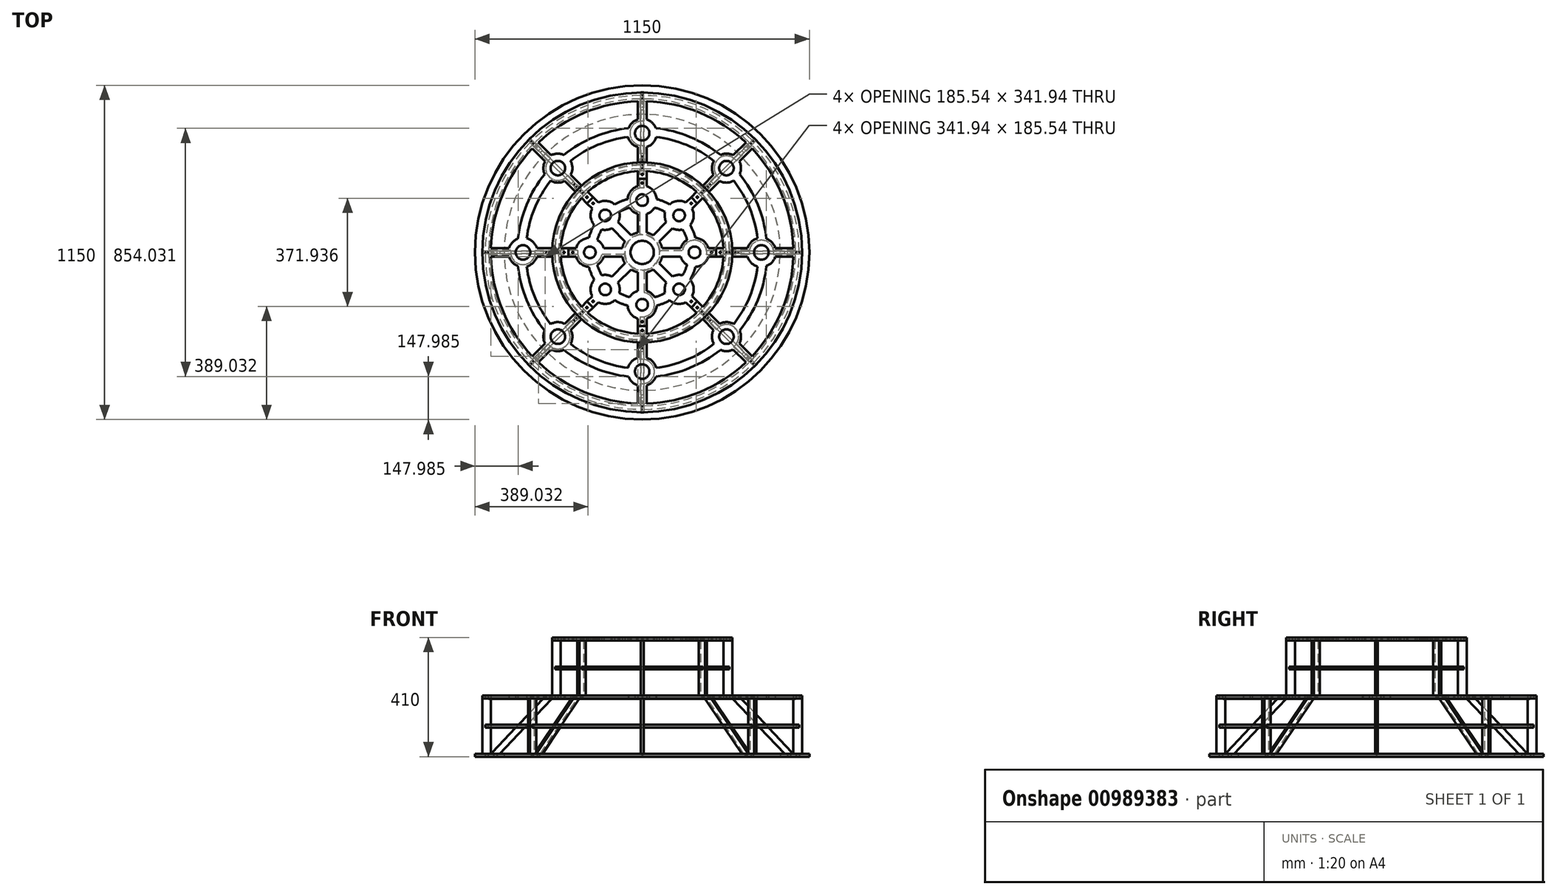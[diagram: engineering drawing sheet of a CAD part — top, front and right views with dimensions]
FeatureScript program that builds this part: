
annotation { "Feature Type Name" : "Feature", "Feature Type Description" : "" }
export const myFeature = defineFeature(function(context is Context, id is Id, definition is map)
    precondition{}
    {
        {
            var Q0;
            Q0=qCreatedBy(makeId("Top.planeOp"),FACE);
            cPlane(context, id + "F0", {"entities" : qUnion([Q0]), "cplaneType" : CPlaneType.OFFSET, "offset" : 200 * mm, "width" : 150 * mm, "height" : 150 * mm});
        }
        {
            var Q0;
            Q0=qCreatedBy(makeId("Top.planeOp"),FACE);
            cPlane(context, id + "F1", {"entities" : qUnion([Q0]), "cplaneType" : CPlaneType.OFFSET, "offset" : 200 * mm, "oppositeDirection" : true, "width" : 150 * mm, "height" : 150 * mm});
        }
        {
            var Q0;
            Q0=qCreatedBy(makeId("Top.planeOp"),FACE);
            cPlane(context, id + "F2", {"entities" : qUnion([Q0]), "cplaneType" : CPlaneType.OFFSET, "offset" : 100 * mm, "oppositeDirection" : true, "width" : 150 * mm, "height" : 150 * mm});
        }
        {
            var Q0;
            Q0=qCreatedBy(makeId("Top.planeOp"),FACE);
            cPlane(context, id + "F3", {"entities" : qUnion([Q0]), "cplaneType" : CPlaneType.OFFSET, "offset" : 100 * mm, "width" : 150 * mm, "height" : 150 * mm});
        }
        {
            var Q0;
            Q0=qCreatedBy(makeId("Top.planeOp"),FACE);
            var sketch = newSketch(context, id + "F4", { "sketchPlane" : qUnion([Q0])});
            skCircle(sketch, "E0", {"center": v(0, 0) * mm, "radius": 550 * mm});
            skArc(sketch, "E1", {"start": v(15, -519.78) * mm, "mid": v(199, -480.42) * mm, "end": v(356.94, -378.15) * mm});
            skArc(sketch, "E2", {"start": v(46.86, -427.44) * mm, "mid": v(164.55, -397.27) * mm, "end": v(269.1, -335.38) * mm});
            skArc(sketch, "E3", {"start": v(48.3, -397.07) * mm, "mid": v(153.07, -369.55) * mm, "end": v(246.62, -314.93) * mm});
            skArc(sketch, "E4", {"start": v(15, -309.64) * mm, "mid": v(118.63, -286.4) * mm, "end": v(208.34, -229.55) * mm});
            skCircle(sketch, "E5", {"center": v(0, 0) * mm, "radius": 280 * mm});
            skCircle(sketch, "E6", {"center": v(0, 0) * mm, "radius": 190 * mm, "construction": true});
            skCircle(sketch, "E7", {"center": v(0, 0) * mm, "radius": 160 * mm, "construction": true});
            skCircle(sketch, "E8", {"center": v(0, 0) * mm, "radius": 40 * mm, "construction": true});
            skCircle(sketch, "E9", {"center": v(0, 0) * mm, "radius": 70 * mm, "construction": true});
            skLineSegment(sketch, "E10", {"start": v(0, 725.48) * mm, "end": v(0, -722.46) * mm, "construction": true});
            skLineSegment(sketch, "E11", {"start": v(-695.44, 0) * mm, "end": v(901.66, 0) * mm, "construction": true});
            skArc(sketch, "E12", {"start": v(-15, -362.3) * mm, "mid": v(-36.11, -375.42) * mm, "end": v(-48.3, -397.07) * mm});
            skCircle(sketch, "E13", {"center": v(0, -410) * mm, "radius": 25 * mm});
            skLineSegment(sketch, "E14", {"start": v(15, -519.78) * mm, "end": v(15, -457.7) * mm});
            skLineSegment(sketch, "E15", {"start": v(-15, -457.7) * mm, "end": v(-15, -519.78) * mm});
            skLineSegment(sketch, "E16", {"start": v(-15, -362.3) * mm, "end": v(-15, -309.64) * mm});
            skLineSegment(sketch, "E17", {"start": v(15, -362.3) * mm, "end": v(15, -309.64) * mm});
            skArc(sketch, "E18.trimOffspring", {"start": v(-46.86, -427.44) * mm, "mid": v(-34.43, -446.26) * mm, "end": v(-15, -457.7) * mm});
            skArc(sketch, "E19.trimOffspring", {"start": v(48.3, -397.07) * mm, "mid": v(36.11, -375.42) * mm, "end": v(15, -362.3) * mm});
            skArc(sketch, "E20.trimOffspring", {"start": v(15, -457.7) * mm, "mid": v(34.43, -446.26) * mm, "end": v(46.86, -427.44) * mm});
            skArc(sketch, "E21.1.0", {"start": v(334.25, -313.03) * mm, "mid": v(339.9, -291.2) * mm, "end": v(335.38, -269.1) * mm});
            skCircle(sketch, "E21.1.1", {"center": v(289.91, -289.91) * mm, "radius": 25 * mm});
            skLineSegment(sketch, "E21.1.2", {"start": v(266.8, -245.58) * mm, "end": v(229.55, -208.34) * mm});
            skLineSegment(sketch, "E21.1.3", {"start": v(245.58, -266.8) * mm, "end": v(208.34, -229.55) * mm});
            skArc(sketch, "E21.1.4", {"start": v(245.58, -266.8) * mm, "mid": v(239.93, -291) * mm, "end": v(246.62, -314.93) * mm});
            skArc(sketch, "E21.1.5", {"start": v(269.1, -335.38) * mm, "mid": v(291.2, -339.9) * mm, "end": v(313.03, -334.25) * mm});
            skArc(sketch, "E21.1.6", {"start": v(314.93, -246.62) * mm, "mid": v(291, -239.93) * mm, "end": v(266.8, -245.58) * mm});
            skLineSegment(sketch, "E21.1.7", {"start": v(378.15, -356.94) * mm, "end": v(334.25, -313.03) * mm});
            skLineSegment(sketch, "E21.1.8", {"start": v(313.03, -334.25) * mm, "end": v(356.94, -378.15) * mm});
            skArc(sketch, "E21.2.0", {"start": v(457.7, 15) * mm, "mid": v(446.26, 34.43) * mm, "end": v(427.44, 46.86) * mm});
            skCircle(sketch, "E21.2.1", {"center": v(410, 0) * mm, "radius": 25 * mm});
            skLineSegment(sketch, "E21.2.2", {"start": v(362.3, 15) * mm, "end": v(309.64, 15) * mm});
            skLineSegment(sketch, "E21.2.3", {"start": v(362.3, -15) * mm, "end": v(309.64, -15) * mm});
            skArc(sketch, "E21.2.4", {"start": v(362.3, -15) * mm, "mid": v(375.42, -36.11) * mm, "end": v(397.07, -48.3) * mm});
            skArc(sketch, "E21.2.5", {"start": v(427.44, -46.86) * mm, "mid": v(446.26, -34.43) * mm, "end": v(457.7, -15) * mm});
            skArc(sketch, "E21.2.6", {"start": v(397.07, 48.3) * mm, "mid": v(375.42, 36.11) * mm, "end": v(362.3, 15) * mm});
            skLineSegment(sketch, "E21.2.7", {"start": v(519.78, 15) * mm, "end": v(457.7, 15) * mm});
            skLineSegment(sketch, "E21.2.8", {"start": v(457.7, -15) * mm, "end": v(519.78, -15) * mm});
            skArc(sketch, "E21.3.0", {"start": v(313.03, 334.25) * mm, "mid": v(291.2, 339.9) * mm, "end": v(269.1, 335.38) * mm});
            skCircle(sketch, "E21.3.1", {"center": v(289.91, 289.91) * mm, "radius": 25 * mm});
            skLineSegment(sketch, "E21.3.2", {"start": v(245.58, 266.8) * mm, "end": v(208.34, 229.55) * mm});
            skLineSegment(sketch, "E21.3.3", {"start": v(266.8, 245.58) * mm, "end": v(229.55, 208.34) * mm});
            skArc(sketch, "E21.3.4", {"start": v(266.8, 245.58) * mm, "mid": v(291, 239.93) * mm, "end": v(314.93, 246.62) * mm});
            skArc(sketch, "E21.3.5", {"start": v(335.38, 269.1) * mm, "mid": v(339.9, 291.2) * mm, "end": v(334.25, 313.03) * mm});
            skArc(sketch, "E21.3.6", {"start": v(246.62, 314.93) * mm, "mid": v(239.93, 291) * mm, "end": v(245.58, 266.8) * mm});
            skLineSegment(sketch, "E21.3.7", {"start": v(356.94, 378.15) * mm, "end": v(313.03, 334.25) * mm});
            skLineSegment(sketch, "E21.3.8", {"start": v(334.25, 313.03) * mm, "end": v(378.15, 356.94) * mm});
            skArc(sketch, "E21.4.0", {"start": v(-15, 457.7) * mm, "mid": v(-34.43, 446.26) * mm, "end": v(-46.86, 427.44) * mm});
            skCircle(sketch, "E21.4.1", {"center": v(0, 410) * mm, "radius": 25 * mm});
            skLineSegment(sketch, "E21.4.2", {"start": v(-15, 362.3) * mm, "end": v(-15, 309.64) * mm});
            skLineSegment(sketch, "E21.4.3", {"start": v(15, 362.3) * mm, "end": v(15, 309.64) * mm});
            skArc(sketch, "E21.4.4", {"start": v(15, 362.3) * mm, "mid": v(36.11, 375.42) * mm, "end": v(48.3, 397.07) * mm});
            skArc(sketch, "E21.4.5", {"start": v(46.86, 427.44) * mm, "mid": v(34.43, 446.26) * mm, "end": v(15, 457.7) * mm});
            skArc(sketch, "E21.4.6", {"start": v(-48.3, 397.07) * mm, "mid": v(-36.11, 375.42) * mm, "end": v(-15, 362.3) * mm});
            skLineSegment(sketch, "E21.4.7", {"start": v(-15, 519.78) * mm, "end": v(-15, 457.7) * mm});
            skLineSegment(sketch, "E21.4.8", {"start": v(15, 457.7) * mm, "end": v(15, 519.78) * mm});
            skArc(sketch, "E21.5.0", {"start": v(-334.25, 313.03) * mm, "mid": v(-339.9, 291.2) * mm, "end": v(-335.38, 269.1) * mm});
            skCircle(sketch, "E21.5.1", {"center": v(-289.91, 289.91) * mm, "radius": 25 * mm});
            skLineSegment(sketch, "E21.5.2", {"start": v(-266.8, 245.58) * mm, "end": v(-229.55, 208.34) * mm});
            skLineSegment(sketch, "E21.5.3", {"start": v(-245.58, 266.8) * mm, "end": v(-208.34, 229.55) * mm});
            skArc(sketch, "E21.5.4", {"start": v(-245.58, 266.8) * mm, "mid": v(-239.93, 291) * mm, "end": v(-246.62, 314.93) * mm});
            skArc(sketch, "E21.5.5", {"start": v(-269.1, 335.38) * mm, "mid": v(-291.2, 339.9) * mm, "end": v(-313.03, 334.25) * mm});
            skArc(sketch, "E21.5.6", {"start": v(-314.93, 246.62) * mm, "mid": v(-291, 239.93) * mm, "end": v(-266.8, 245.58) * mm});
            skLineSegment(sketch, "E21.5.7", {"start": v(-378.15, 356.94) * mm, "end": v(-334.25, 313.03) * mm});
            skLineSegment(sketch, "E21.5.8", {"start": v(-313.03, 334.25) * mm, "end": v(-356.94, 378.15) * mm});
            skArc(sketch, "E21.6.0", {"start": v(-457.7, -15) * mm, "mid": v(-446.26, -34.43) * mm, "end": v(-427.44, -46.86) * mm});
            skCircle(sketch, "E21.6.1", {"center": v(-410, 0) * mm, "radius": 25 * mm});
            skLineSegment(sketch, "E21.6.2", {"start": v(-362.3, -15) * mm, "end": v(-309.64, -15) * mm});
            skLineSegment(sketch, "E21.6.3", {"start": v(-362.3, 15) * mm, "end": v(-309.64, 15) * mm});
            skArc(sketch, "E21.6.4", {"start": v(-362.3, 15) * mm, "mid": v(-375.42, 36.11) * mm, "end": v(-397.07, 48.3) * mm});
            skArc(sketch, "E21.6.5", {"start": v(-427.44, 46.86) * mm, "mid": v(-446.26, 34.43) * mm, "end": v(-457.7, 15) * mm});
            skArc(sketch, "E21.6.6", {"start": v(-397.07, -48.3) * mm, "mid": v(-375.42, -36.11) * mm, "end": v(-362.3, -15) * mm});
            skLineSegment(sketch, "E21.6.7", {"start": v(-519.78, -15) * mm, "end": v(-457.7, -15) * mm});
            skLineSegment(sketch, "E21.6.8", {"start": v(-457.7, 15) * mm, "end": v(-519.78, 15) * mm});
            skArc(sketch, "E21.7.0", {"start": v(-313.03, -334.25) * mm, "mid": v(-291.2, -339.9) * mm, "end": v(-269.1, -335.38) * mm});
            skCircle(sketch, "E21.7.1", {"center": v(-289.91, -289.91) * mm, "radius": 25 * mm});
            skLineSegment(sketch, "E21.7.2", {"start": v(-245.58, -266.8) * mm, "end": v(-208.34, -229.55) * mm});
            skLineSegment(sketch, "E21.7.3", {"start": v(-266.8, -245.58) * mm, "end": v(-229.55, -208.34) * mm});
            skArc(sketch, "E21.7.4", {"start": v(-266.8, -245.58) * mm, "mid": v(-291, -239.93) * mm, "end": v(-314.93, -246.62) * mm});
            skArc(sketch, "E21.7.5", {"start": v(-335.38, -269.1) * mm, "mid": v(-339.9, -291.2) * mm, "end": v(-334.25, -313.03) * mm});
            skArc(sketch, "E21.7.6", {"start": v(-246.62, -314.93) * mm, "mid": v(-239.93, -291) * mm, "end": v(-245.58, -266.8) * mm});
            skLineSegment(sketch, "E21.7.7", {"start": v(-356.94, -378.15) * mm, "end": v(-313.03, -334.25) * mm});
            skLineSegment(sketch, "E21.7.8", {"start": v(-334.25, -313.03) * mm, "end": v(-378.15, -356.94) * mm});
            skArc(sketch, "E22.trimOffspring", {"start": v(-246.62, -314.93) * mm, "mid": v(-153.07, -369.55) * mm, "end": v(-48.3, -397.07) * mm});
            skArc(sketch, "E23.trimOffspring", {"start": v(-269.1, -335.38) * mm, "mid": v(-164.55, -397.27) * mm, "end": v(-46.86, -427.44) * mm});
            skArc(sketch, "E24.trimOffspring", {"start": v(-356.94, -378.15) * mm, "mid": v(-199, -480.42) * mm, "end": v(-15, -519.78) * mm});
            skArc(sketch, "E25.trimOffspring", {"start": v(-208.34, -229.55) * mm, "mid": v(-118.63, -286.4) * mm, "end": v(-15, -309.64) * mm});
            skArc(sketch, "E26.trimOffspring", {"start": v(-397.07, -48.3) * mm, "mid": v(-369.55, -153.07) * mm, "end": v(-314.93, -246.62) * mm});
            skArc(sketch, "E27.trimOffspring", {"start": v(-427.44, -46.86) * mm, "mid": v(-397.27, -164.55) * mm, "end": v(-335.38, -269.1) * mm});
            skArc(sketch, "E28.trimOffspring", {"start": v(-309.64, -15) * mm, "mid": v(-286.4, -118.63) * mm, "end": v(-229.55, -208.34) * mm});
            skArc(sketch, "E29.trimOffspring", {"start": v(-519.78, -15) * mm, "mid": v(-480.42, -199) * mm, "end": v(-378.15, -356.94) * mm});
            skArc(sketch, "E30.trimOffspring", {"start": v(-314.93, 246.62) * mm, "mid": v(-369.55, 153.07) * mm, "end": v(-397.07, 48.3) * mm});
            skArc(sketch, "E31.trimOffspring", {"start": v(-335.38, 269.1) * mm, "mid": v(-397.27, 164.55) * mm, "end": v(-427.44, 46.86) * mm});
            skArc(sketch, "E32.trimOffspring", {"start": v(-378.15, 356.94) * mm, "mid": v(-480.42, 199) * mm, "end": v(-519.78, 15) * mm});
            skArc(sketch, "E33.trimOffspring", {"start": v(-229.55, 208.34) * mm, "mid": v(-286.4, 118.63) * mm, "end": v(-309.64, 15) * mm});
            skArc(sketch, "E34.trimOffspring", {"start": v(-15, 309.64) * mm, "mid": v(-118.63, 286.4) * mm, "end": v(-208.34, 229.55) * mm});
            skArc(sketch, "E35.trimOffspring", {"start": v(-48.3, 397.07) * mm, "mid": v(-153.07, 369.55) * mm, "end": v(-246.62, 314.93) * mm});
            skArc(sketch, "E36.trimOffspring", {"start": v(-46.86, 427.44) * mm, "mid": v(-164.55, 397.27) * mm, "end": v(-269.1, 335.38) * mm});
            skArc(sketch, "E37.trimOffspring", {"start": v(-15, 519.78) * mm, "mid": v(-199, 480.42) * mm, "end": v(-356.94, 378.15) * mm});
            skArc(sketch, "E38.trimOffspring", {"start": v(269.1, 335.38) * mm, "mid": v(164.55, 397.27) * mm, "end": v(46.86, 427.44) * mm});
            skArc(sketch, "E39.trimOffspring", {"start": v(246.62, 314.93) * mm, "mid": v(153.07, 369.55) * mm, "end": v(48.3, 397.07) * mm});
            skArc(sketch, "E40.trimOffspring", {"start": v(208.34, 229.55) * mm, "mid": v(118.63, 286.4) * mm, "end": v(15, 309.64) * mm});
            skArc(sketch, "E41.trimOffspring", {"start": v(356.94, 378.15) * mm, "mid": v(199, 480.42) * mm, "end": v(15, 519.78) * mm});
            skArc(sketch, "E42.trimOffspring", {"start": v(309.64, 15) * mm, "mid": v(286.4, 118.63) * mm, "end": v(229.55, 208.34) * mm});
            skArc(sketch, "E43.trimOffspring", {"start": v(397.07, 48.3) * mm, "mid": v(369.55, 153.07) * mm, "end": v(314.93, 246.62) * mm});
            skArc(sketch, "E44.trimOffspring", {"start": v(427.44, 46.86) * mm, "mid": v(397.27, 164.55) * mm, "end": v(335.38, 269.1) * mm});
            skArc(sketch, "E45.trimOffspring", {"start": v(519.78, 15) * mm, "mid": v(480.42, 199) * mm, "end": v(378.15, 356.94) * mm});
            skArc(sketch, "E46.trimOffspring", {"start": v(335.38, -269.1) * mm, "mid": v(397.27, -164.55) * mm, "end": v(427.44, -46.86) * mm});
            skArc(sketch, "E47.trimOffspring", {"start": v(314.93, -246.62) * mm, "mid": v(369.55, -153.07) * mm, "end": v(397.07, -48.3) * mm});
            skArc(sketch, "E48.trimOffspring", {"start": v(378.15, -356.94) * mm, "mid": v(480.42, -199) * mm, "end": v(519.78, -15) * mm});
            skArc(sketch, "E49.trimOffspring", {"start": v(229.55, -208.34) * mm, "mid": v(286.4, -118.63) * mm, "end": v(309.64, -15) * mm});
            skLineSegment(sketch, "E50.bottom", {"start": v(4.9, 530) * mm, "end": v(1, 530) * mm});
            skLineSegment(sketch, "E50.top", {"start": v(4.9, 540) * mm, "end": v(1, 540) * mm});
            skLineSegment(sketch, "E50.left", {"start": v(4.9, 530) * mm, "end": v(4.9, 540) * mm});
            skLineSegment(sketch, "E50.right", {"start": v(-4.9, 530) * mm, "end": v(-4.9, 540) * mm});
            skPoint(sketch, "E50.middle", {"position": v(0, 535) * mm});
            skLineSegment(sketch, "E51", {"start": v(0, 541) * mm, "end": v(-1, 540) * mm});
            skLineSegment(sketch, "E52", {"start": v(0, 541) * mm, "end": v(1, 540) * mm});
            skLineSegment(sketch, "E53.trimOffspring", {"start": v(-1, 540) * mm, "end": v(-4.9, 540) * mm});
            skLineSegment(sketch, "E54", {"start": v(0, 529) * mm, "end": v(-1, 530) * mm});
            skLineSegment(sketch, "E55", {"start": v(0, 529) * mm, "end": v(1, 530) * mm});
            skLineSegment(sketch, "E56.trimOffspring", {"start": v(-1, 530) * mm, "end": v(-4.9, 530) * mm});
            skPoint(sketch, "E57.1.0", {"position": v(-378.3, 378.3) * mm});
            skLineSegment(sketch, "E57.1.1", {"start": v(-378.23, 371.3) * mm, "end": v(-385.3, 378.37) * mm});
            skLineSegment(sketch, "E57.1.2", {"start": v(-371.3, 378.23) * mm, "end": v(-378.37, 385.3) * mm});
            skLineSegment(sketch, "E57.1.3", {"start": v(-371.3, 378.23) * mm, "end": v(-374.06, 375.47) * mm});
            skLineSegment(sketch, "E57.1.4", {"start": v(-374.06, 374.06) * mm, "end": v(-374.06, 375.47) * mm});
            skLineSegment(sketch, "E57.1.5", {"start": v(-374.06, 374.06) * mm, "end": v(-375.47, 374.06) * mm});
            skLineSegment(sketch, "E57.1.6", {"start": v(-375.47, 374.06) * mm, "end": v(-378.23, 371.3) * mm});
            skLineSegment(sketch, "E57.1.7", {"start": v(-378.37, 385.3) * mm, "end": v(-381.13, 382.54) * mm});
            skLineSegment(sketch, "E57.1.8", {"start": v(-382.54, 381.13) * mm, "end": v(-385.3, 378.37) * mm});
            skLineSegment(sketch, "E57.1.9", {"start": v(-382.54, 382.54) * mm, "end": v(-381.13, 382.54) * mm});
            skLineSegment(sketch, "E57.1.10", {"start": v(-382.54, 382.54) * mm, "end": v(-382.54, 381.13) * mm});
            skPoint(sketch, "E57.2.0", {"position": v(-535, 0) * mm});
            skLineSegment(sketch, "E57.2.1", {"start": v(-530, -4.9) * mm, "end": v(-540, -4.9) * mm});
            skLineSegment(sketch, "E57.2.2", {"start": v(-530, 4.9) * mm, "end": v(-540, 4.9) * mm});
            skLineSegment(sketch, "E57.2.3", {"start": v(-530, 4.9) * mm, "end": v(-530, 1) * mm});
            skLineSegment(sketch, "E57.2.4", {"start": v(-529, 0) * mm, "end": v(-530, 1) * mm});
            skLineSegment(sketch, "E57.2.5", {"start": v(-529, 0) * mm, "end": v(-530, -1) * mm});
            skLineSegment(sketch, "E57.2.6", {"start": v(-530, -1) * mm, "end": v(-530, -4.9) * mm});
            skLineSegment(sketch, "E57.2.7", {"start": v(-540, 4.9) * mm, "end": v(-540, 1) * mm});
            skLineSegment(sketch, "E57.2.8", {"start": v(-540, -1) * mm, "end": v(-540, -4.9) * mm});
            skLineSegment(sketch, "E57.2.9", {"start": v(-541, 0) * mm, "end": v(-540, 1) * mm});
            skLineSegment(sketch, "E57.2.10", {"start": v(-541, 0) * mm, "end": v(-540, -1) * mm});
            skPoint(sketch, "E57.3.0", {"position": v(-378.3, -378.3) * mm});
            skLineSegment(sketch, "E57.3.1", {"start": v(-371.3, -378.23) * mm, "end": v(-378.37, -385.3) * mm});
            skLineSegment(sketch, "E57.3.2", {"start": v(-378.23, -371.3) * mm, "end": v(-385.3, -378.37) * mm});
            skLineSegment(sketch, "E57.3.3", {"start": v(-378.23, -371.3) * mm, "end": v(-375.47, -374.06) * mm});
            skLineSegment(sketch, "E57.3.4", {"start": v(-374.06, -374.06) * mm, "end": v(-375.47, -374.06) * mm});
            skLineSegment(sketch, "E57.3.5", {"start": v(-374.06, -374.06) * mm, "end": v(-374.06, -375.47) * mm});
            skLineSegment(sketch, "E57.3.6", {"start": v(-374.06, -375.47) * mm, "end": v(-371.3, -378.23) * mm});
            skLineSegment(sketch, "E57.3.7", {"start": v(-385.3, -378.37) * mm, "end": v(-382.54, -381.13) * mm});
            skLineSegment(sketch, "E57.3.8", {"start": v(-381.13, -382.54) * mm, "end": v(-378.37, -385.3) * mm});
            skLineSegment(sketch, "E57.3.9", {"start": v(-382.54, -382.54) * mm, "end": v(-382.54, -381.13) * mm});
            skLineSegment(sketch, "E57.3.10", {"start": v(-382.54, -382.54) * mm, "end": v(-381.13, -382.54) * mm});
            skPoint(sketch, "E57.4.0", {"position": v(0, -535) * mm});
            skLineSegment(sketch, "E57.4.1", {"start": v(4.9, -530) * mm, "end": v(4.9, -540) * mm});
            skLineSegment(sketch, "E57.4.2", {"start": v(-4.9, -530) * mm, "end": v(-4.9, -540) * mm});
            skLineSegment(sketch, "E57.4.3", {"start": v(-4.9, -530) * mm, "end": v(-1, -530) * mm});
            skLineSegment(sketch, "E57.4.4", {"start": v(0, -529) * mm, "end": v(-1, -530) * mm});
            skLineSegment(sketch, "E57.4.5", {"start": v(0, -529) * mm, "end": v(1, -530) * mm});
            skLineSegment(sketch, "E57.4.6", {"start": v(1, -530) * mm, "end": v(4.9, -530) * mm});
            skLineSegment(sketch, "E57.4.7", {"start": v(-4.9, -540) * mm, "end": v(-1, -540) * mm});
            skLineSegment(sketch, "E57.4.8", {"start": v(1, -540) * mm, "end": v(4.9, -540) * mm});
            skLineSegment(sketch, "E57.4.9", {"start": v(0, -541) * mm, "end": v(-1, -540) * mm});
            skLineSegment(sketch, "E57.4.10", {"start": v(0, -541) * mm, "end": v(1, -540) * mm});
            skPoint(sketch, "E57.5.0", {"position": v(378.3, -378.3) * mm});
            skLineSegment(sketch, "E57.5.1", {"start": v(378.23, -371.3) * mm, "end": v(385.3, -378.37) * mm});
            skLineSegment(sketch, "E57.5.2", {"start": v(371.3, -378.23) * mm, "end": v(378.37, -385.3) * mm});
            skLineSegment(sketch, "E57.5.3", {"start": v(371.3, -378.23) * mm, "end": v(374.06, -375.47) * mm});
            skLineSegment(sketch, "E57.5.4", {"start": v(374.06, -374.06) * mm, "end": v(374.06, -375.47) * mm});
            skLineSegment(sketch, "E57.5.5", {"start": v(374.06, -374.06) * mm, "end": v(375.47, -374.06) * mm});
            skLineSegment(sketch, "E57.5.6", {"start": v(375.47, -374.06) * mm, "end": v(378.23, -371.3) * mm});
            skLineSegment(sketch, "E57.5.7", {"start": v(378.37, -385.3) * mm, "end": v(381.13, -382.54) * mm});
            skLineSegment(sketch, "E57.5.8", {"start": v(382.54, -381.13) * mm, "end": v(385.3, -378.37) * mm});
            skLineSegment(sketch, "E57.5.9", {"start": v(382.54, -382.54) * mm, "end": v(381.13, -382.54) * mm});
            skLineSegment(sketch, "E57.5.10", {"start": v(382.54, -382.54) * mm, "end": v(382.54, -381.13) * mm});
            skPoint(sketch, "E57.6.0", {"position": v(535, 0) * mm});
            skLineSegment(sketch, "E57.6.1", {"start": v(530, 4.9) * mm, "end": v(540, 4.9) * mm});
            skLineSegment(sketch, "E57.6.2", {"start": v(530, -4.9) * mm, "end": v(540, -4.9) * mm});
            skLineSegment(sketch, "E57.6.3", {"start": v(530, -4.9) * mm, "end": v(530, -1) * mm});
            skLineSegment(sketch, "E57.6.4", {"start": v(529, 0) * mm, "end": v(530, -1) * mm});
            skLineSegment(sketch, "E57.6.5", {"start": v(529, 0) * mm, "end": v(530, 1) * mm});
            skLineSegment(sketch, "E57.6.6", {"start": v(530, 1) * mm, "end": v(530, 4.9) * mm});
            skLineSegment(sketch, "E57.6.7", {"start": v(540, -4.9) * mm, "end": v(540, -1) * mm});
            skLineSegment(sketch, "E57.6.8", {"start": v(540, 1) * mm, "end": v(540, 4.9) * mm});
            skLineSegment(sketch, "E57.6.9", {"start": v(541, 0) * mm, "end": v(540, -1) * mm});
            skLineSegment(sketch, "E57.6.10", {"start": v(541, 0) * mm, "end": v(540, 1) * mm});
            skPoint(sketch, "E57.7.0", {"position": v(378.3, 378.3) * mm});
            skLineSegment(sketch, "E57.7.1", {"start": v(371.3, 378.23) * mm, "end": v(378.37, 385.3) * mm});
            skLineSegment(sketch, "E57.7.2", {"start": v(378.23, 371.3) * mm, "end": v(385.3, 378.37) * mm});
            skLineSegment(sketch, "E57.7.3", {"start": v(378.23, 371.3) * mm, "end": v(375.47, 374.06) * mm});
            skLineSegment(sketch, "E57.7.4", {"start": v(374.06, 374.06) * mm, "end": v(375.47, 374.06) * mm});
            skLineSegment(sketch, "E57.7.5", {"start": v(374.06, 374.06) * mm, "end": v(374.06, 375.47) * mm});
            skLineSegment(sketch, "E57.7.6", {"start": v(374.06, 375.47) * mm, "end": v(371.3, 378.23) * mm});
            skLineSegment(sketch, "E57.7.7", {"start": v(385.3, 378.37) * mm, "end": v(382.54, 381.13) * mm});
            skLineSegment(sketch, "E57.7.8", {"start": v(381.13, 382.54) * mm, "end": v(378.37, 385.3) * mm});
            skLineSegment(sketch, "E57.7.9", {"start": v(382.54, 382.54) * mm, "end": v(382.54, 381.13) * mm});
            skLineSegment(sketch, "E57.7.10", {"start": v(382.54, 382.54) * mm, "end": v(381.13, 382.54) * mm});
            skLineSegment(sketch, "E58.bottom", {"start": v(4.9, 290) * mm, "end": v(1, 290) * mm});
            skLineSegment(sketch, "E58.top", {"start": v(4.9, 300) * mm, "end": v(1, 300) * mm});
            skLineSegment(sketch, "E58.left", {"start": v(4.9, 290) * mm, "end": v(4.9, 300) * mm});
            skLineSegment(sketch, "E58.right", {"start": v(-4.9, 290) * mm, "end": v(-4.9, 300) * mm});
            skPoint(sketch, "E58.middle", {"position": v(0, 295) * mm});
            skLineSegment(sketch, "E59", {"start": v(0, 301) * mm, "end": v(-1, 300) * mm});
            skLineSegment(sketch, "E60", {"start": v(0, 301) * mm, "end": v(1, 300) * mm});
            skLineSegment(sketch, "E61.trimOffspring", {"start": v(-1, 300) * mm, "end": v(-4.9, 300) * mm});
            skLineSegment(sketch, "E62", {"start": v(0, 289) * mm, "end": v(-1, 290) * mm});
            skLineSegment(sketch, "E63", {"start": v(0, 289) * mm, "end": v(1, 290) * mm});
            skLineSegment(sketch, "E64.trimOffspring", {"start": v(-1, 290) * mm, "end": v(-4.9, 290) * mm});
            skLineSegment(sketch, "E65.1.0", {"start": v(-201.6, 208.53) * mm, "end": v(-208.67, 215.6) * mm});
            skPoint(sketch, "E65.1.1", {"position": v(-208.6, 208.6) * mm});
            skLineSegment(sketch, "E65.1.2", {"start": v(-208.53, 201.6) * mm, "end": v(-215.6, 208.67) * mm});
            skLineSegment(sketch, "E65.1.3", {"start": v(-205.77, 204.35) * mm, "end": v(-208.53, 201.6) * mm});
            skLineSegment(sketch, "E65.1.4", {"start": v(-208.67, 215.6) * mm, "end": v(-211.42, 212.84) * mm});
            skLineSegment(sketch, "E65.1.5", {"start": v(-201.6, 208.53) * mm, "end": v(-204.35, 205.77) * mm});
            skLineSegment(sketch, "E65.1.6", {"start": v(-212.84, 211.42) * mm, "end": v(-215.6, 208.67) * mm});
            skLineSegment(sketch, "E65.1.7", {"start": v(-204.35, 204.35) * mm, "end": v(-205.77, 204.35) * mm});
            skLineSegment(sketch, "E65.1.8", {"start": v(-212.84, 212.84) * mm, "end": v(-211.42, 212.84) * mm});
            skLineSegment(sketch, "E65.1.9", {"start": v(-212.84, 212.84) * mm, "end": v(-212.84, 211.42) * mm});
            skLineSegment(sketch, "E65.1.10", {"start": v(-204.35, 204.35) * mm, "end": v(-204.35, 205.77) * mm});
            skLineSegment(sketch, "E65.2.0", {"start": v(-290, 4.9) * mm, "end": v(-300, 4.9) * mm});
            skPoint(sketch, "E65.2.1", {"position": v(-295, 0) * mm});
            skLineSegment(sketch, "E65.2.2", {"start": v(-290, -4.9) * mm, "end": v(-300, -4.9) * mm});
            skLineSegment(sketch, "E65.2.3", {"start": v(-290, -1) * mm, "end": v(-290, -4.9) * mm});
            skLineSegment(sketch, "E65.2.4", {"start": v(-300, 4.9) * mm, "end": v(-300, 1) * mm});
            skLineSegment(sketch, "E65.2.5", {"start": v(-290, 4.9) * mm, "end": v(-290, 1) * mm});
            skLineSegment(sketch, "E65.2.6", {"start": v(-300, -1) * mm, "end": v(-300, -4.9) * mm});
            skLineSegment(sketch, "E65.2.7", {"start": v(-289, 0) * mm, "end": v(-290, -1) * mm});
            skLineSegment(sketch, "E65.2.8", {"start": v(-301, 0) * mm, "end": v(-300, 1) * mm});
            skLineSegment(sketch, "E65.2.9", {"start": v(-301, 0) * mm, "end": v(-300, -1) * mm});
            skLineSegment(sketch, "E65.2.10", {"start": v(-289, 0) * mm, "end": v(-290, 1) * mm});
            skLineSegment(sketch, "E65.3.0", {"start": v(-208.53, -201.6) * mm, "end": v(-215.6, -208.67) * mm});
            skPoint(sketch, "E65.3.1", {"position": v(-208.6, -208.6) * mm});
            skLineSegment(sketch, "E65.3.2", {"start": v(-201.6, -208.53) * mm, "end": v(-208.67, -215.6) * mm});
            skLineSegment(sketch, "E65.3.3", {"start": v(-204.35, -205.77) * mm, "end": v(-201.6, -208.53) * mm});
            skLineSegment(sketch, "E65.3.4", {"start": v(-215.6, -208.67) * mm, "end": v(-212.84, -211.42) * mm});
            skLineSegment(sketch, "E65.3.5", {"start": v(-208.53, -201.6) * mm, "end": v(-205.77, -204.35) * mm});
            skLineSegment(sketch, "E65.3.6", {"start": v(-211.42, -212.84) * mm, "end": v(-208.67, -215.6) * mm});
            skLineSegment(sketch, "E65.3.7", {"start": v(-204.35, -204.35) * mm, "end": v(-204.35, -205.77) * mm});
            skLineSegment(sketch, "E65.3.8", {"start": v(-212.84, -212.84) * mm, "end": v(-212.84, -211.42) * mm});
            skLineSegment(sketch, "E65.3.9", {"start": v(-212.84, -212.84) * mm, "end": v(-211.42, -212.84) * mm});
            skLineSegment(sketch, "E65.3.10", {"start": v(-204.35, -204.35) * mm, "end": v(-205.77, -204.35) * mm});
            skLineSegment(sketch, "E65.4.0", {"start": v(-4.9, -290) * mm, "end": v(-4.9, -300) * mm});
            skPoint(sketch, "E65.4.1", {"position": v(0, -295) * mm});
            skLineSegment(sketch, "E65.4.2", {"start": v(4.9, -290) * mm, "end": v(4.9, -300) * mm});
            skLineSegment(sketch, "E65.4.3", {"start": v(1, -290) * mm, "end": v(4.9, -290) * mm});
            skLineSegment(sketch, "E65.4.4", {"start": v(-4.9, -300) * mm, "end": v(-1, -300) * mm});
            skLineSegment(sketch, "E65.4.5", {"start": v(-4.9, -290) * mm, "end": v(-1, -290) * mm});
            skLineSegment(sketch, "E65.4.6", {"start": v(1, -300) * mm, "end": v(4.9, -300) * mm});
            skLineSegment(sketch, "E65.4.7", {"start": v(0, -289) * mm, "end": v(1, -290) * mm});
            skLineSegment(sketch, "E65.4.8", {"start": v(0, -301) * mm, "end": v(-1, -300) * mm});
            skLineSegment(sketch, "E65.4.9", {"start": v(0, -301) * mm, "end": v(1, -300) * mm});
            skLineSegment(sketch, "E65.4.10", {"start": v(0, -289) * mm, "end": v(-1, -290) * mm});
            skLineSegment(sketch, "E65.5.0", {"start": v(201.6, -208.53) * mm, "end": v(208.67, -215.6) * mm});
            skPoint(sketch, "E65.5.1", {"position": v(208.6, -208.6) * mm});
            skLineSegment(sketch, "E65.5.2", {"start": v(208.53, -201.6) * mm, "end": v(215.6, -208.67) * mm});
            skLineSegment(sketch, "E65.5.3", {"start": v(205.77, -204.35) * mm, "end": v(208.53, -201.6) * mm});
            skLineSegment(sketch, "E65.5.4", {"start": v(208.67, -215.6) * mm, "end": v(211.42, -212.84) * mm});
            skLineSegment(sketch, "E65.5.5", {"start": v(201.6, -208.53) * mm, "end": v(204.35, -205.77) * mm});
            skLineSegment(sketch, "E65.5.6", {"start": v(212.84, -211.42) * mm, "end": v(215.6, -208.67) * mm});
            skLineSegment(sketch, "E65.5.7", {"start": v(204.35, -204.35) * mm, "end": v(205.77, -204.35) * mm});
            skLineSegment(sketch, "E65.5.8", {"start": v(212.84, -212.84) * mm, "end": v(211.42, -212.84) * mm});
            skLineSegment(sketch, "E65.5.9", {"start": v(212.84, -212.84) * mm, "end": v(212.84, -211.42) * mm});
            skLineSegment(sketch, "E65.5.10", {"start": v(204.35, -204.35) * mm, "end": v(204.35, -205.77) * mm});
            skLineSegment(sketch, "E65.6.0", {"start": v(290, -4.9) * mm, "end": v(300, -4.9) * mm});
            skPoint(sketch, "E65.6.1", {"position": v(295, 0) * mm});
            skLineSegment(sketch, "E65.6.2", {"start": v(290, 4.9) * mm, "end": v(300, 4.9) * mm});
            skLineSegment(sketch, "E65.6.3", {"start": v(290, 1) * mm, "end": v(290, 4.9) * mm});
            skLineSegment(sketch, "E65.6.4", {"start": v(300, -4.9) * mm, "end": v(300, -1) * mm});
            skLineSegment(sketch, "E65.6.5", {"start": v(290, -4.9) * mm, "end": v(290, -1) * mm});
            skLineSegment(sketch, "E65.6.6", {"start": v(300, 1) * mm, "end": v(300, 4.9) * mm});
            skLineSegment(sketch, "E65.6.7", {"start": v(289, 0) * mm, "end": v(290, 1) * mm});
            skLineSegment(sketch, "E65.6.8", {"start": v(301, 0) * mm, "end": v(300, -1) * mm});
            skLineSegment(sketch, "E65.6.9", {"start": v(301, 0) * mm, "end": v(300, 1) * mm});
            skLineSegment(sketch, "E65.6.10", {"start": v(289, 0) * mm, "end": v(290, -1) * mm});
            skLineSegment(sketch, "E65.7.0", {"start": v(208.53, 201.6) * mm, "end": v(215.6, 208.67) * mm});
            skPoint(sketch, "E65.7.1", {"position": v(208.6, 208.6) * mm});
            skLineSegment(sketch, "E65.7.2", {"start": v(201.6, 208.53) * mm, "end": v(208.67, 215.6) * mm});
            skLineSegment(sketch, "E65.7.3", {"start": v(204.35, 205.77) * mm, "end": v(201.6, 208.53) * mm});
            skLineSegment(sketch, "E65.7.4", {"start": v(215.6, 208.67) * mm, "end": v(212.84, 211.42) * mm});
            skLineSegment(sketch, "E65.7.5", {"start": v(208.53, 201.6) * mm, "end": v(205.77, 204.35) * mm});
            skLineSegment(sketch, "E65.7.6", {"start": v(211.42, 212.84) * mm, "end": v(208.67, 215.6) * mm});
            skLineSegment(sketch, "E65.7.7", {"start": v(204.35, 204.35) * mm, "end": v(204.35, 205.77) * mm});
            skLineSegment(sketch, "E65.7.8", {"start": v(212.84, 212.84) * mm, "end": v(212.84, 211.42) * mm});
            skLineSegment(sketch, "E65.7.9", {"start": v(212.84, 212.84) * mm, "end": v(211.42, 212.84) * mm});
            skLineSegment(sketch, "E65.7.10", {"start": v(204.35, 204.35) * mm, "end": v(205.77, 204.35) * mm});
            skLineSegment(sketch, "E66.bottom", {"start": v(4.9, 320) * mm, "end": v(1, 320) * mm});
            skLineSegment(sketch, "E66.top", {"start": v(4.9, 330) * mm, "end": v(1, 330) * mm});
            skLineSegment(sketch, "E66.left", {"start": v(4.9, 320) * mm, "end": v(4.9, 330) * mm});
            skLineSegment(sketch, "E66.right", {"start": v(-4.9, 320) * mm, "end": v(-4.9, 330) * mm});
            skPoint(sketch, "E66.middle", {"position": v(0, 325) * mm});
            skLineSegment(sketch, "E67", {"start": v(0, 331) * mm, "end": v(-1, 330) * mm});
            skLineSegment(sketch, "E68", {"start": v(0, 331) * mm, "end": v(1, 330) * mm});
            skLineSegment(sketch, "E69.trimOffspring", {"start": v(-1, 330) * mm, "end": v(-4.9, 330) * mm});
            skLineSegment(sketch, "E70", {"start": v(0, 319) * mm, "end": v(-1, 320) * mm});
            skLineSegment(sketch, "E71", {"start": v(0, 319) * mm, "end": v(1, 320) * mm});
            skLineSegment(sketch, "E72.trimOffspring", {"start": v(-1, 320) * mm, "end": v(-4.9, 320) * mm});
            skLineSegment(sketch, "E73.1.0", {"start": v(-222.8, 229.74) * mm, "end": v(-225.57, 226.98) * mm});
            skLineSegment(sketch, "E73.1.1", {"start": v(-229.74, 222.8) * mm, "end": v(-236.81, 229.88) * mm});
            skLineSegment(sketch, "E73.1.2", {"start": v(-222.8, 229.74) * mm, "end": v(-229.88, 236.81) * mm});
            skLineSegment(sketch, "E73.1.3", {"start": v(-229.88, 236.81) * mm, "end": v(-232.64, 234.05) * mm});
            skLineSegment(sketch, "E73.1.4", {"start": v(-234.05, 232.64) * mm, "end": v(-236.81, 229.88) * mm});
            skLineSegment(sketch, "E73.1.5", {"start": v(-226.98, 225.57) * mm, "end": v(-229.74, 222.8) * mm});
            skPoint(sketch, "E73.1.6", {"position": v(-229.8, 229.8) * mm});
            skLineSegment(sketch, "E73.1.7", {"start": v(-225.57, 225.57) * mm, "end": v(-225.57, 226.98) * mm});
            skLineSegment(sketch, "E73.1.8", {"start": v(-225.57, 225.57) * mm, "end": v(-226.98, 225.57) * mm});
            skLineSegment(sketch, "E73.1.9", {"start": v(-234.05, 234.05) * mm, "end": v(-234.05, 232.64) * mm});
            skLineSegment(sketch, "E73.1.10", {"start": v(-234.05, 234.05) * mm, "end": v(-232.64, 234.05) * mm});
            skLineSegment(sketch, "E73.2.0", {"start": v(-320, 4.9) * mm, "end": v(-320, 1) * mm});
            skLineSegment(sketch, "E73.2.1", {"start": v(-320, -4.9) * mm, "end": v(-330, -4.9) * mm});
            skLineSegment(sketch, "E73.2.2", {"start": v(-320, 4.9) * mm, "end": v(-330, 4.9) * mm});
            skLineSegment(sketch, "E73.2.3", {"start": v(-330, 4.9) * mm, "end": v(-330, 1) * mm});
            skLineSegment(sketch, "E73.2.4", {"start": v(-330, -1) * mm, "end": v(-330, -4.9) * mm});
            skLineSegment(sketch, "E73.2.5", {"start": v(-320, -1) * mm, "end": v(-320, -4.9) * mm});
            skPoint(sketch, "E73.2.6", {"position": v(-325, 0) * mm});
            skLineSegment(sketch, "E73.2.7", {"start": v(-319, 0) * mm, "end": v(-320, 1) * mm});
            skLineSegment(sketch, "E73.2.8", {"start": v(-319, 0) * mm, "end": v(-320, -1) * mm});
            skLineSegment(sketch, "E73.2.9", {"start": v(-331, 0) * mm, "end": v(-330, -1) * mm});
            skLineSegment(sketch, "E73.2.10", {"start": v(-331, 0) * mm, "end": v(-330, 1) * mm});
            skLineSegment(sketch, "E73.3.0", {"start": v(-229.74, -222.8) * mm, "end": v(-226.98, -225.57) * mm});
            skLineSegment(sketch, "E73.3.1", {"start": v(-222.8, -229.74) * mm, "end": v(-229.88, -236.81) * mm});
            skLineSegment(sketch, "E73.3.2", {"start": v(-229.74, -222.8) * mm, "end": v(-236.81, -229.88) * mm});
            skLineSegment(sketch, "E73.3.3", {"start": v(-236.81, -229.88) * mm, "end": v(-234.05, -232.64) * mm});
            skLineSegment(sketch, "E73.3.4", {"start": v(-232.64, -234.05) * mm, "end": v(-229.88, -236.81) * mm});
            skLineSegment(sketch, "E73.3.5", {"start": v(-225.57, -226.98) * mm, "end": v(-222.8, -229.74) * mm});
            skPoint(sketch, "E73.3.6", {"position": v(-229.8, -229.8) * mm});
            skLineSegment(sketch, "E73.3.7", {"start": v(-225.57, -225.57) * mm, "end": v(-226.98, -225.57) * mm});
            skLineSegment(sketch, "E73.3.8", {"start": v(-225.57, -225.57) * mm, "end": v(-225.57, -226.98) * mm});
            skLineSegment(sketch, "E73.3.9", {"start": v(-234.05, -234.05) * mm, "end": v(-232.64, -234.05) * mm});
            skLineSegment(sketch, "E73.3.10", {"start": v(-234.05, -234.05) * mm, "end": v(-234.05, -232.64) * mm});
            skLineSegment(sketch, "E73.4.0", {"start": v(-4.9, -320) * mm, "end": v(-1, -320) * mm});
            skLineSegment(sketch, "E73.4.1", {"start": v(4.9, -320) * mm, "end": v(4.9, -330) * mm});
            skLineSegment(sketch, "E73.4.2", {"start": v(-4.9, -320) * mm, "end": v(-4.9, -330) * mm});
            skLineSegment(sketch, "E73.4.3", {"start": v(-4.9, -330) * mm, "end": v(-1, -330) * mm});
            skLineSegment(sketch, "E73.4.4", {"start": v(1, -330) * mm, "end": v(4.9, -330) * mm});
            skLineSegment(sketch, "E73.4.5", {"start": v(1, -320) * mm, "end": v(4.9, -320) * mm});
            skPoint(sketch, "E73.4.6", {"position": v(0, -325) * mm});
            skLineSegment(sketch, "E73.4.7", {"start": v(0, -319) * mm, "end": v(-1, -320) * mm});
            skLineSegment(sketch, "E73.4.8", {"start": v(0, -319) * mm, "end": v(1, -320) * mm});
            skLineSegment(sketch, "E73.4.9", {"start": v(0, -331) * mm, "end": v(1, -330) * mm});
            skLineSegment(sketch, "E73.4.10", {"start": v(0, -331) * mm, "end": v(-1, -330) * mm});
            skLineSegment(sketch, "E73.5.0", {"start": v(222.8, -229.74) * mm, "end": v(225.57, -226.98) * mm});
            skLineSegment(sketch, "E73.5.1", {"start": v(229.74, -222.8) * mm, "end": v(236.81, -229.88) * mm});
            skLineSegment(sketch, "E73.5.2", {"start": v(222.8, -229.74) * mm, "end": v(229.88, -236.81) * mm});
            skLineSegment(sketch, "E73.5.3", {"start": v(229.88, -236.81) * mm, "end": v(232.64, -234.05) * mm});
            skLineSegment(sketch, "E73.5.4", {"start": v(234.05, -232.64) * mm, "end": v(236.81, -229.88) * mm});
            skLineSegment(sketch, "E73.5.5", {"start": v(226.98, -225.57) * mm, "end": v(229.74, -222.8) * mm});
            skPoint(sketch, "E73.5.6", {"position": v(229.8, -229.8) * mm});
            skLineSegment(sketch, "E73.5.7", {"start": v(225.57, -225.57) * mm, "end": v(225.57, -226.98) * mm});
            skLineSegment(sketch, "E73.5.8", {"start": v(225.57, -225.57) * mm, "end": v(226.98, -225.57) * mm});
            skLineSegment(sketch, "E73.5.9", {"start": v(234.05, -234.05) * mm, "end": v(234.05, -232.64) * mm});
            skLineSegment(sketch, "E73.5.10", {"start": v(234.05, -234.05) * mm, "end": v(232.64, -234.05) * mm});
            skLineSegment(sketch, "E73.6.0", {"start": v(320, -4.9) * mm, "end": v(320, -1) * mm});
            skLineSegment(sketch, "E73.6.1", {"start": v(320, 4.9) * mm, "end": v(330, 4.9) * mm});
            skLineSegment(sketch, "E73.6.2", {"start": v(320, -4.9) * mm, "end": v(330, -4.9) * mm});
            skLineSegment(sketch, "E73.6.3", {"start": v(330, -4.9) * mm, "end": v(330, -1) * mm});
            skLineSegment(sketch, "E73.6.4", {"start": v(330, 1) * mm, "end": v(330, 4.9) * mm});
            skLineSegment(sketch, "E73.6.5", {"start": v(320, 1) * mm, "end": v(320, 4.9) * mm});
            skPoint(sketch, "E73.6.6", {"position": v(325, 0) * mm});
            skLineSegment(sketch, "E73.6.7", {"start": v(319, 0) * mm, "end": v(320, -1) * mm});
            skLineSegment(sketch, "E73.6.8", {"start": v(319, 0) * mm, "end": v(320, 1) * mm});
            skLineSegment(sketch, "E73.6.9", {"start": v(331, 0) * mm, "end": v(330, 1) * mm});
            skLineSegment(sketch, "E73.6.10", {"start": v(331, 0) * mm, "end": v(330, -1) * mm});
            skLineSegment(sketch, "E73.7.0", {"start": v(229.74, 222.8) * mm, "end": v(226.98, 225.57) * mm});
            skLineSegment(sketch, "E73.7.1", {"start": v(222.8, 229.74) * mm, "end": v(229.88, 236.81) * mm});
            skLineSegment(sketch, "E73.7.2", {"start": v(229.74, 222.8) * mm, "end": v(236.81, 229.88) * mm});
            skLineSegment(sketch, "E73.7.3", {"start": v(236.81, 229.88) * mm, "end": v(234.05, 232.64) * mm});
            skLineSegment(sketch, "E73.7.4", {"start": v(232.64, 234.05) * mm, "end": v(229.88, 236.81) * mm});
            skLineSegment(sketch, "E73.7.5", {"start": v(225.57, 226.98) * mm, "end": v(222.8, 229.74) * mm});
            skPoint(sketch, "E73.7.6", {"position": v(229.8, 229.8) * mm});
            skLineSegment(sketch, "E73.7.7", {"start": v(225.57, 225.57) * mm, "end": v(226.98, 225.57) * mm});
            skLineSegment(sketch, "E73.7.8", {"start": v(225.57, 225.57) * mm, "end": v(225.57, 226.98) * mm});
            skLineSegment(sketch, "E73.7.9", {"start": v(234.05, 234.05) * mm, "end": v(232.64, 234.05) * mm});
            skLineSegment(sketch, "E73.7.10", {"start": v(234.05, 234.05) * mm, "end": v(234.05, 232.64) * mm});
            skSolve(sketch);
        }
        {
            var Q0;
            Q0=qSketchRegion(id+"F4",true);
            extrude(context, id + "F5", {"entities" : qUnion([Q0]), "depth" : 10 * mm, "offsetDistance" : 25 * mm});
        }
        {
            var Q0;
            Q0=qCreatedBy(id+"F0.planeOp",FACE);
            var sketch = newSketch(context, id + "F6", { "sketchPlane" : qUnion([Q0])});
            skArc(sketch, "E74.0", {"start": v(42.8, -154.17) * mm, "mid": v(61.23, -147.82) * mm, "end": v(78.74, -139.28) * mm});
            skArc(sketch, "E75.0", {"start": v(49.89, -183.33) * mm, "mid": v(72.7, -175.54) * mm, "end": v(94.36, -164.91) * mm});
            skArc(sketch, "E76.0", {"start": v(15, -279.6) * mm, "mid": v(107.15, -258.69) * mm, "end": v(187.1, -208.31) * mm});
            skArc(sketch, "E77.0", {"start": v(15, -68.37) * mm, "mid": v(26.79, -64.67) * mm, "end": v(37.74, -58.95) * mm});
            skCircle(sketch, "E78.0", {"center": v(0, 0) * mm, "radius": 40 * mm});
            skPoint(sketch, "E79.0", {"position": v(15, 309.64) * mm});
            skCircle(sketch, "E80", {"center": v(0, 0) * mm, "radius": 310 * mm});
            skArc(sketch, "E81", {"start": v(-15, -132.3) * mm, "mid": v(-30.9, -140.7) * mm, "end": v(-42.8, -154.17) * mm});
            skCircle(sketch, "E82", {"center": v(0, -180) * mm, "radius": 20 * mm});
            skLineSegment(sketch, "E83", {"start": v(-15, -68.37) * mm, "end": v(-15, -132.3) * mm});
            skLineSegment(sketch, "E84", {"start": v(15, -68.37) * mm, "end": v(15, -132.3) * mm});
            skLineSegment(sketch, "E85", {"start": v(-15, -227.7) * mm, "end": v(-15, -279.6) * mm});
            skLineSegment(sketch, "E86", {"start": v(15, -227.7) * mm, "end": v(15, -279.6) * mm});
            skArc(sketch, "E87.trimOffspring", {"start": v(42.8, -154.17) * mm, "mid": v(30.9, -140.7) * mm, "end": v(15, -132.3) * mm});
            skArc(sketch, "E88.trimOffspring", {"start": v(15, -227.7) * mm, "mid": v(39.3, -210.9) * mm, "end": v(49.89, -183.33) * mm});
            skArc(sketch, "E89.trimOffspring", {"start": v(-49.89, -183.33) * mm, "mid": v(-39.3, -210.9) * mm, "end": v(-15, -227.7) * mm});
            skLineSegment(sketch, "E90.1.0", {"start": v(58.95, -37.74) * mm, "end": v(104.16, -82.95) * mm});
            skLineSegment(sketch, "E90.1.1", {"start": v(37.74, -58.95) * mm, "end": v(82.95, -104.16) * mm});
            skArc(sketch, "E90.1.2", {"start": v(82.95, -104.16) * mm, "mid": v(77.63, -121.34) * mm, "end": v(78.74, -139.28) * mm});
            skCircle(sketch, "E90.1.3", {"center": v(127.28, -127.28) * mm, "radius": 20 * mm});
            skArc(sketch, "E90.1.4", {"start": v(94.36, -164.91) * mm, "mid": v(121.34, -176.93) * mm, "end": v(150.4, -171.61) * mm});
            skArc(sketch, "E90.1.5", {"start": v(171.61, -150.4) * mm, "mid": v(176.93, -121.34) * mm, "end": v(164.91, -94.36) * mm});
            skArc(sketch, "E90.1.6", {"start": v(139.28, -78.74) * mm, "mid": v(121.34, -77.63) * mm, "end": v(104.16, -82.95) * mm});
            skLineSegment(sketch, "E90.1.7", {"start": v(171.61, -150.4) * mm, "end": v(208.31, -187.1) * mm});
            skLineSegment(sketch, "E90.1.8", {"start": v(150.4, -171.61) * mm, "end": v(187.1, -208.31) * mm});
            skLineSegment(sketch, "E90.2.0", {"start": v(68.37, 15) * mm, "end": v(132.3, 15) * mm});
            skLineSegment(sketch, "E90.2.1", {"start": v(68.37, -15) * mm, "end": v(132.3, -15) * mm});
            skArc(sketch, "E90.2.2", {"start": v(132.3, -15) * mm, "mid": v(140.7, -30.9) * mm, "end": v(154.17, -42.8) * mm});
            skCircle(sketch, "E90.2.3", {"center": v(180, 0) * mm, "radius": 20 * mm});
            skArc(sketch, "E90.2.4", {"start": v(183.33, -49.89) * mm, "mid": v(210.9, -39.3) * mm, "end": v(227.7, -15) * mm});
            skArc(sketch, "E90.2.5", {"start": v(227.7, 15) * mm, "mid": v(210.9, 39.3) * mm, "end": v(183.33, 49.89) * mm});
            skArc(sketch, "E90.2.6", {"start": v(154.17, 42.8) * mm, "mid": v(140.7, 30.9) * mm, "end": v(132.3, 15) * mm});
            skLineSegment(sketch, "E90.2.7", {"start": v(227.7, 15) * mm, "end": v(279.6, 15) * mm});
            skLineSegment(sketch, "E90.2.8", {"start": v(227.7, -15) * mm, "end": v(279.6, -15) * mm});
            skLineSegment(sketch, "E90.3.0", {"start": v(37.74, 58.95) * mm, "end": v(82.95, 104.16) * mm});
            skLineSegment(sketch, "E90.3.1", {"start": v(58.95, 37.74) * mm, "end": v(104.16, 82.95) * mm});
            skArc(sketch, "E90.3.2", {"start": v(104.16, 82.95) * mm, "mid": v(121.34, 77.63) * mm, "end": v(139.28, 78.74) * mm});
            skCircle(sketch, "E90.3.3", {"center": v(127.28, 127.28) * mm, "radius": 20 * mm});
            skArc(sketch, "E90.3.4", {"start": v(164.91, 94.36) * mm, "mid": v(176.93, 121.34) * mm, "end": v(171.61, 150.4) * mm});
            skArc(sketch, "E90.3.5", {"start": v(150.4, 171.61) * mm, "mid": v(121.34, 176.93) * mm, "end": v(94.36, 164.91) * mm});
            skArc(sketch, "E90.3.6", {"start": v(78.74, 139.28) * mm, "mid": v(77.63, 121.34) * mm, "end": v(82.95, 104.16) * mm});
            skLineSegment(sketch, "E90.3.7", {"start": v(150.4, 171.61) * mm, "end": v(187.1, 208.31) * mm});
            skLineSegment(sketch, "E90.3.8", {"start": v(171.61, 150.4) * mm, "end": v(208.31, 187.1) * mm});
            skLineSegment(sketch, "E90.4.0", {"start": v(-15, 68.37) * mm, "end": v(-15, 132.3) * mm});
            skLineSegment(sketch, "E90.4.1", {"start": v(15, 68.37) * mm, "end": v(15, 132.3) * mm});
            skArc(sketch, "E90.4.2", {"start": v(15, 132.3) * mm, "mid": v(30.9, 140.7) * mm, "end": v(42.8, 154.17) * mm});
            skCircle(sketch, "E90.4.3", {"center": v(0, 180) * mm, "radius": 20 * mm});
            skArc(sketch, "E90.4.4", {"start": v(49.89, 183.33) * mm, "mid": v(39.3, 210.9) * mm, "end": v(15, 227.7) * mm});
            skArc(sketch, "E90.4.5", {"start": v(-15, 227.7) * mm, "mid": v(-39.3, 210.9) * mm, "end": v(-49.89, 183.33) * mm});
            skArc(sketch, "E90.4.6", {"start": v(-42.8, 154.17) * mm, "mid": v(-30.9, 140.7) * mm, "end": v(-15, 132.3) * mm});
            skLineSegment(sketch, "E90.4.7", {"start": v(-15, 227.7) * mm, "end": v(-15, 279.6) * mm});
            skLineSegment(sketch, "E90.4.8", {"start": v(15, 227.7) * mm, "end": v(15, 279.6) * mm});
            skLineSegment(sketch, "E90.5.0", {"start": v(-58.95, 37.74) * mm, "end": v(-104.16, 82.95) * mm});
            skLineSegment(sketch, "E90.5.1", {"start": v(-37.74, 58.95) * mm, "end": v(-82.95, 104.16) * mm});
            skArc(sketch, "E90.5.2", {"start": v(-82.95, 104.16) * mm, "mid": v(-77.63, 121.34) * mm, "end": v(-78.74, 139.28) * mm});
            skCircle(sketch, "E90.5.3", {"center": v(-127.28, 127.28) * mm, "radius": 20 * mm});
            skArc(sketch, "E90.5.4", {"start": v(-94.36, 164.91) * mm, "mid": v(-121.34, 176.93) * mm, "end": v(-150.4, 171.61) * mm});
            skArc(sketch, "E90.5.5", {"start": v(-171.61, 150.4) * mm, "mid": v(-176.93, 121.34) * mm, "end": v(-164.91, 94.36) * mm});
            skArc(sketch, "E90.5.6", {"start": v(-139.28, 78.74) * mm, "mid": v(-121.34, 77.63) * mm, "end": v(-104.16, 82.95) * mm});
            skLineSegment(sketch, "E90.5.7", {"start": v(-171.61, 150.4) * mm, "end": v(-208.31, 187.1) * mm});
            skLineSegment(sketch, "E90.5.8", {"start": v(-150.4, 171.61) * mm, "end": v(-187.1, 208.31) * mm});
            skLineSegment(sketch, "E90.6.0", {"start": v(-68.37, -15) * mm, "end": v(-132.3, -15) * mm});
            skLineSegment(sketch, "E90.6.1", {"start": v(-68.37, 15) * mm, "end": v(-132.3, 15) * mm});
            skArc(sketch, "E90.6.2", {"start": v(-132.3, 15) * mm, "mid": v(-140.7, 30.9) * mm, "end": v(-154.17, 42.8) * mm});
            skCircle(sketch, "E90.6.3", {"center": v(-180, 0) * mm, "radius": 20 * mm});
            skArc(sketch, "E90.6.4", {"start": v(-183.33, 49.89) * mm, "mid": v(-210.9, 39.3) * mm, "end": v(-227.7, 15) * mm});
            skArc(sketch, "E90.6.5", {"start": v(-227.7, -15) * mm, "mid": v(-210.9, -39.3) * mm, "end": v(-183.33, -49.89) * mm});
            skArc(sketch, "E90.6.6", {"start": v(-154.17, -42.8) * mm, "mid": v(-140.7, -30.9) * mm, "end": v(-132.3, -15) * mm});
            skLineSegment(sketch, "E90.6.7", {"start": v(-227.7, -15) * mm, "end": v(-279.6, -15) * mm});
            skLineSegment(sketch, "E90.6.8", {"start": v(-227.7, 15) * mm, "end": v(-279.6, 15) * mm});
            skLineSegment(sketch, "E90.7.0", {"start": v(-37.74, -58.95) * mm, "end": v(-82.95, -104.16) * mm});
            skLineSegment(sketch, "E90.7.1", {"start": v(-58.95, -37.74) * mm, "end": v(-104.16, -82.95) * mm});
            skArc(sketch, "E90.7.2", {"start": v(-104.16, -82.95) * mm, "mid": v(-121.34, -77.63) * mm, "end": v(-139.28, -78.74) * mm});
            skCircle(sketch, "E90.7.3", {"center": v(-127.28, -127.28) * mm, "radius": 20 * mm});
            skArc(sketch, "E90.7.4", {"start": v(-164.91, -94.36) * mm, "mid": v(-176.93, -121.34) * mm, "end": v(-171.61, -150.4) * mm});
            skArc(sketch, "E90.7.5", {"start": v(-150.4, -171.61) * mm, "mid": v(-121.34, -176.93) * mm, "end": v(-94.36, -164.91) * mm});
            skArc(sketch, "E90.7.6", {"start": v(-78.74, -139.28) * mm, "mid": v(-77.63, -121.34) * mm, "end": v(-82.95, -104.16) * mm});
            skLineSegment(sketch, "E90.7.7", {"start": v(-150.4, -171.61) * mm, "end": v(-187.1, -208.31) * mm});
            skLineSegment(sketch, "E90.7.8", {"start": v(-171.61, -150.4) * mm, "end": v(-208.31, -187.1) * mm});
            skArc(sketch, "E91.trimOffspring", {"start": v(-94.36, -164.91) * mm, "mid": v(-72.7, -175.54) * mm, "end": v(-49.89, -183.33) * mm});
            skArc(sketch, "E92.trimOffspring", {"start": v(-78.74, -139.28) * mm, "mid": v(-61.23, -147.82) * mm, "end": v(-42.8, -154.17) * mm});
            skArc(sketch, "E93.trimOffspring", {"start": v(-187.1, -208.31) * mm, "mid": v(-107.15, -258.69) * mm, "end": v(-15, -279.6) * mm});
            skArc(sketch, "E94.trimOffspring", {"start": v(-37.74, -58.95) * mm, "mid": v(-26.79, -64.67) * mm, "end": v(-15, -68.37) * mm});
            skArc(sketch, "E95.trimOffspring", {"start": v(-68.37, -15) * mm, "mid": v(-64.67, -26.79) * mm, "end": v(-58.95, -37.74) * mm});
            skArc(sketch, "E96.trimOffspring", {"start": v(-154.17, -42.8) * mm, "mid": v(-147.82, -61.23) * mm, "end": v(-139.28, -78.74) * mm});
            skArc(sketch, "E97.trimOffspring", {"start": v(-183.33, -49.89) * mm, "mid": v(-175.54, -72.7) * mm, "end": v(-164.91, -94.36) * mm});
            skArc(sketch, "E98.trimOffspring", {"start": v(-279.6, -15) * mm, "mid": v(-258.69, -107.15) * mm, "end": v(-208.31, -187.1) * mm});
            skArc(sketch, "E99.trimOffspring", {"start": v(-164.91, 94.36) * mm, "mid": v(-175.54, 72.7) * mm, "end": v(-183.33, 49.89) * mm});
            skArc(sketch, "E100.trimOffspring", {"start": v(-139.28, 78.74) * mm, "mid": v(-147.82, 61.23) * mm, "end": v(-154.17, 42.8) * mm});
            skArc(sketch, "E101.trimOffspring", {"start": v(-208.31, 187.1) * mm, "mid": v(-258.69, 107.15) * mm, "end": v(-279.6, 15) * mm});
            skArc(sketch, "E102.trimOffspring", {"start": v(-58.95, 37.74) * mm, "mid": v(-64.67, 26.79) * mm, "end": v(-68.37, 15) * mm});
            skArc(sketch, "E103.trimOffspring", {"start": v(-15, 68.37) * mm, "mid": v(-26.79, 64.67) * mm, "end": v(-37.74, 58.95) * mm});
            skArc(sketch, "E104.trimOffspring", {"start": v(-42.8, 154.17) * mm, "mid": v(-61.23, 147.82) * mm, "end": v(-78.74, 139.28) * mm});
            skArc(sketch, "E105.trimOffspring", {"start": v(-49.89, 183.33) * mm, "mid": v(-72.7, 175.54) * mm, "end": v(-94.36, 164.91) * mm});
            skArc(sketch, "E106.trimOffspring", {"start": v(78.74, 139.28) * mm, "mid": v(61.23, 147.82) * mm, "end": v(42.8, 154.17) * mm});
            skArc(sketch, "E107.trimOffspring", {"start": v(94.36, 164.91) * mm, "mid": v(72.7, 175.54) * mm, "end": v(49.89, 183.33) * mm});
            skArc(sketch, "E108.trimOffspring", {"start": v(183.33, 49.89) * mm, "mid": v(175.54, 72.7) * mm, "end": v(164.91, 94.36) * mm});
            skArc(sketch, "E109.trimOffspring", {"start": v(154.17, 42.8) * mm, "mid": v(147.82, 61.23) * mm, "end": v(139.28, 78.74) * mm});
            skArc(sketch, "E110.trimOffspring", {"start": v(68.37, 15) * mm, "mid": v(64.67, 26.79) * mm, "end": v(58.95, 37.74) * mm});
            skArc(sketch, "E111.trimOffspring", {"start": v(279.6, 15) * mm, "mid": v(258.69, 107.15) * mm, "end": v(208.31, 187.1) * mm});
            skArc(sketch, "E112.trimOffspring", {"start": v(58.95, -37.74) * mm, "mid": v(64.67, -26.79) * mm, "end": v(68.37, -15) * mm});
            skArc(sketch, "E113.trimOffspring", {"start": v(139.28, -78.74) * mm, "mid": v(147.82, -61.23) * mm, "end": v(154.17, -42.8) * mm});
            skArc(sketch, "E114.trimOffspring", {"start": v(164.91, -94.36) * mm, "mid": v(175.54, -72.7) * mm, "end": v(183.33, -49.89) * mm});
            skArc(sketch, "E115.trimOffspring", {"start": v(208.31, -187.1) * mm, "mid": v(258.69, -107.15) * mm, "end": v(279.6, -15) * mm});
            skArc(sketch, "E116.trimOffspring", {"start": v(37.74, 58.95) * mm, "mid": v(26.79, 64.67) * mm, "end": v(15, 68.37) * mm});
            skLineSegment(sketch, "E117.0", {"start": v(-4.9, 290) * mm, "end": v(-4.9, 300) * mm});
            skLineSegment(sketch, "E118.0", {"start": v(-1, 300) * mm, "end": v(-4.9, 300) * mm});
            skLineSegment(sketch, "E119.0", {"start": v(0, 301) * mm, "end": v(-1, 300) * mm});
            skLineSegment(sketch, "E120.0", {"start": v(0, 301) * mm, "end": v(1, 300) * mm});
            skLineSegment(sketch, "E121.0", {"start": v(4.9, 300) * mm, "end": v(1, 300) * mm});
            skLineSegment(sketch, "E122.0", {"start": v(4.9, 290) * mm, "end": v(4.9, 300) * mm});
            skLineSegment(sketch, "E123.0", {"start": v(-1, 290) * mm, "end": v(-4.9, 290) * mm});
            skLineSegment(sketch, "E124.0", {"start": v(0, 289) * mm, "end": v(-1, 290) * mm});
            skLineSegment(sketch, "E125.0", {"start": v(0, 289) * mm, "end": v(1, 290) * mm});
            skLineSegment(sketch, "E126.0", {"start": v(4.9, 290) * mm, "end": v(1, 290) * mm});
            skArc(sketch, "E127.trimOffspring", {"start": v(-15, 279.6) * mm, "mid": v(-107.15, 258.69) * mm, "end": v(-187.1, 208.31) * mm});
            skArc(sketch, "E128.trimOffspring", {"start": v(187.1, 208.31) * mm, "mid": v(107.15, 258.69) * mm, "end": v(15, 279.6) * mm});
            skLineSegment(sketch, "E129.1.0", {"start": v(-205.77, 204.35) * mm, "end": v(-208.53, 201.6) * mm});
            skLineSegment(sketch, "E129.1.1", {"start": v(-208.67, 215.6) * mm, "end": v(-211.42, 212.84) * mm});
            skLineSegment(sketch, "E129.1.2", {"start": v(-201.6, 208.53) * mm, "end": v(-204.35, 205.77) * mm});
            skLineSegment(sketch, "E129.1.3", {"start": v(-212.84, 211.42) * mm, "end": v(-215.6, 208.67) * mm});
            skLineSegment(sketch, "E129.1.4", {"start": v(-208.53, 201.6) * mm, "end": v(-215.6, 208.67) * mm});
            skLineSegment(sketch, "E129.1.5", {"start": v(-201.6, 208.53) * mm, "end": v(-208.67, 215.6) * mm});
            skLineSegment(sketch, "E129.1.6", {"start": v(-212.84, 212.84) * mm, "end": v(-211.42, 212.84) * mm});
            skLineSegment(sketch, "E129.1.7", {"start": v(-204.35, 204.35) * mm, "end": v(-204.35, 205.77) * mm});
            skLineSegment(sketch, "E129.1.8", {"start": v(-204.35, 204.35) * mm, "end": v(-205.77, 204.35) * mm});
            skLineSegment(sketch, "E129.1.9", {"start": v(-212.84, 212.84) * mm, "end": v(-212.84, 211.42) * mm});
            skLineSegment(sketch, "E129.2.0", {"start": v(-290, -1) * mm, "end": v(-290, -4.9) * mm});
            skLineSegment(sketch, "E129.2.1", {"start": v(-300, 4.9) * mm, "end": v(-300, 1) * mm});
            skLineSegment(sketch, "E129.2.2", {"start": v(-290, 4.9) * mm, "end": v(-290, 1) * mm});
            skLineSegment(sketch, "E129.2.3", {"start": v(-300, -1) * mm, "end": v(-300, -4.9) * mm});
            skLineSegment(sketch, "E129.2.4", {"start": v(-290, -4.9) * mm, "end": v(-300, -4.9) * mm});
            skLineSegment(sketch, "E129.2.5", {"start": v(-290, 4.9) * mm, "end": v(-300, 4.9) * mm});
            skLineSegment(sketch, "E129.2.6", {"start": v(-301, 0) * mm, "end": v(-300, 1) * mm});
            skLineSegment(sketch, "E129.2.7", {"start": v(-289, 0) * mm, "end": v(-290, 1) * mm});
            skLineSegment(sketch, "E129.2.8", {"start": v(-289, 0) * mm, "end": v(-290, -1) * mm});
            skLineSegment(sketch, "E129.2.9", {"start": v(-301, 0) * mm, "end": v(-300, -1) * mm});
            skLineSegment(sketch, "E129.3.0", {"start": v(-204.35, -205.77) * mm, "end": v(-201.6, -208.53) * mm});
            skLineSegment(sketch, "E129.3.1", {"start": v(-215.6, -208.67) * mm, "end": v(-212.84, -211.42) * mm});
            skLineSegment(sketch, "E129.3.2", {"start": v(-208.53, -201.6) * mm, "end": v(-205.77, -204.35) * mm});
            skLineSegment(sketch, "E129.3.3", {"start": v(-211.42, -212.84) * mm, "end": v(-208.67, -215.6) * mm});
            skLineSegment(sketch, "E129.3.4", {"start": v(-201.6, -208.53) * mm, "end": v(-208.67, -215.6) * mm});
            skLineSegment(sketch, "E129.3.5", {"start": v(-208.53, -201.6) * mm, "end": v(-215.6, -208.67) * mm});
            skLineSegment(sketch, "E129.3.6", {"start": v(-212.84, -212.84) * mm, "end": v(-212.84, -211.42) * mm});
            skLineSegment(sketch, "E129.3.7", {"start": v(-204.35, -204.35) * mm, "end": v(-205.77, -204.35) * mm});
            skLineSegment(sketch, "E129.3.8", {"start": v(-204.35, -204.35) * mm, "end": v(-204.35, -205.77) * mm});
            skLineSegment(sketch, "E129.3.9", {"start": v(-212.84, -212.84) * mm, "end": v(-211.42, -212.84) * mm});
            skLineSegment(sketch, "E129.4.0", {"start": v(1, -290) * mm, "end": v(4.9, -290) * mm});
            skLineSegment(sketch, "E129.4.1", {"start": v(-4.9, -300) * mm, "end": v(-1, -300) * mm});
            skLineSegment(sketch, "E129.4.2", {"start": v(-4.9, -290) * mm, "end": v(-1, -290) * mm});
            skLineSegment(sketch, "E129.4.3", {"start": v(1, -300) * mm, "end": v(4.9, -300) * mm});
            skLineSegment(sketch, "E129.4.4", {"start": v(4.9, -290) * mm, "end": v(4.9, -300) * mm});
            skLineSegment(sketch, "E129.4.5", {"start": v(-4.9, -290) * mm, "end": v(-4.9, -300) * mm});
            skLineSegment(sketch, "E129.4.6", {"start": v(0, -301) * mm, "end": v(-1, -300) * mm});
            skLineSegment(sketch, "E129.4.7", {"start": v(0, -289) * mm, "end": v(-1, -290) * mm});
            skLineSegment(sketch, "E129.4.8", {"start": v(0, -289) * mm, "end": v(1, -290) * mm});
            skLineSegment(sketch, "E129.4.9", {"start": v(0, -301) * mm, "end": v(1, -300) * mm});
            skLineSegment(sketch, "E129.5.0", {"start": v(205.77, -204.35) * mm, "end": v(208.53, -201.6) * mm});
            skLineSegment(sketch, "E129.5.1", {"start": v(208.67, -215.6) * mm, "end": v(211.42, -212.84) * mm});
            skLineSegment(sketch, "E129.5.2", {"start": v(201.6, -208.53) * mm, "end": v(204.35, -205.77) * mm});
            skLineSegment(sketch, "E129.5.3", {"start": v(212.84, -211.42) * mm, "end": v(215.6, -208.67) * mm});
            skLineSegment(sketch, "E129.5.4", {"start": v(208.53, -201.6) * mm, "end": v(215.6, -208.67) * mm});
            skLineSegment(sketch, "E129.5.5", {"start": v(201.6, -208.53) * mm, "end": v(208.67, -215.6) * mm});
            skLineSegment(sketch, "E129.5.6", {"start": v(212.84, -212.84) * mm, "end": v(211.42, -212.84) * mm});
            skLineSegment(sketch, "E129.5.7", {"start": v(204.35, -204.35) * mm, "end": v(204.35, -205.77) * mm});
            skLineSegment(sketch, "E129.5.8", {"start": v(204.35, -204.35) * mm, "end": v(205.77, -204.35) * mm});
            skLineSegment(sketch, "E129.5.9", {"start": v(212.84, -212.84) * mm, "end": v(212.84, -211.42) * mm});
            skLineSegment(sketch, "E129.6.0", {"start": v(290, 1) * mm, "end": v(290, 4.9) * mm});
            skLineSegment(sketch, "E129.6.1", {"start": v(300, -4.9) * mm, "end": v(300, -1) * mm});
            skLineSegment(sketch, "E129.6.2", {"start": v(290, -4.9) * mm, "end": v(290, -1) * mm});
            skLineSegment(sketch, "E129.6.3", {"start": v(300, 1) * mm, "end": v(300, 4.9) * mm});
            skLineSegment(sketch, "E129.6.4", {"start": v(290, 4.9) * mm, "end": v(300, 4.9) * mm});
            skLineSegment(sketch, "E129.6.5", {"start": v(290, -4.9) * mm, "end": v(300, -4.9) * mm});
            skLineSegment(sketch, "E129.6.6", {"start": v(301, 0) * mm, "end": v(300, -1) * mm});
            skLineSegment(sketch, "E129.6.7", {"start": v(289, 0) * mm, "end": v(290, -1) * mm});
            skLineSegment(sketch, "E129.6.8", {"start": v(289, 0) * mm, "end": v(290, 1) * mm});
            skLineSegment(sketch, "E129.6.9", {"start": v(301, 0) * mm, "end": v(300, 1) * mm});
            skLineSegment(sketch, "E129.7.0", {"start": v(204.35, 205.77) * mm, "end": v(201.6, 208.53) * mm});
            skLineSegment(sketch, "E129.7.1", {"start": v(215.6, 208.67) * mm, "end": v(212.84, 211.42) * mm});
            skLineSegment(sketch, "E129.7.2", {"start": v(208.53, 201.6) * mm, "end": v(205.77, 204.35) * mm});
            skLineSegment(sketch, "E129.7.3", {"start": v(211.42, 212.84) * mm, "end": v(208.67, 215.6) * mm});
            skLineSegment(sketch, "E129.7.4", {"start": v(201.6, 208.53) * mm, "end": v(208.67, 215.6) * mm});
            skLineSegment(sketch, "E129.7.5", {"start": v(208.53, 201.6) * mm, "end": v(215.6, 208.67) * mm});
            skLineSegment(sketch, "E129.7.6", {"start": v(212.84, 212.84) * mm, "end": v(212.84, 211.42) * mm});
            skLineSegment(sketch, "E129.7.7", {"start": v(204.35, 204.35) * mm, "end": v(205.77, 204.35) * mm});
            skLineSegment(sketch, "E129.7.8", {"start": v(204.35, 204.35) * mm, "end": v(204.35, 205.77) * mm});
            skLineSegment(sketch, "E129.7.9", {"start": v(212.84, 212.84) * mm, "end": v(211.42, 212.84) * mm});
            skLineSegment(sketch, "E130", {"start": v(-15, -253.65) * mm, "end": v(15, -253.65) * mm});
            skLineSegment(sketch, "E131", {"start": v(0, -222.27) * mm, "end": v(0, -279.65) * mm, "construction": true});
            skPoint(sketch, "E131.startSnap0", {"position": v(0, -253.65) * mm});
            skCircle(sketch, "E132", {"center": v(0, -268.65) * mm, "radius": 2.5 * mm});
            skCircle(sketch, "E133.MirrorC", {"center": v(0, -238.65) * mm, "radius": 2.5 * mm});
            skCircle(sketch, "E134.1.0", {"center": v(189.96, -189.96) * mm, "radius": 2.5 * mm});
            skLineSegment(sketch, "E134.1.1", {"start": v(168.75, -189.96) * mm, "end": v(189.96, -168.75) * mm});
            skCircle(sketch, "E134.1.2", {"center": v(168.75, -168.75) * mm, "radius": 2.5 * mm});
            skCircle(sketch, "E134.2.0", {"center": v(268.65, 0) * mm, "radius": 2.5 * mm});
            skLineSegment(sketch, "E134.2.1", {"start": v(253.65, -15) * mm, "end": v(253.65, 15) * mm});
            skCircle(sketch, "E134.2.2", {"center": v(238.65, 0) * mm, "radius": 2.5 * mm});
            skCircle(sketch, "E134.3.0", {"center": v(189.96, 189.96) * mm, "radius": 2.5 * mm});
            skLineSegment(sketch, "E134.3.1", {"start": v(189.96, 168.75) * mm, "end": v(168.75, 189.96) * mm});
            skCircle(sketch, "E134.3.2", {"center": v(168.75, 168.75) * mm, "radius": 2.5 * mm});
            skCircle(sketch, "E134.4.0", {"center": v(0, 268.65) * mm, "radius": 2.5 * mm});
            skLineSegment(sketch, "E134.4.1", {"start": v(15, 253.65) * mm, "end": v(-15, 253.65) * mm});
            skCircle(sketch, "E134.4.2", {"center": v(0, 238.65) * mm, "radius": 2.5 * mm});
            skCircle(sketch, "E134.5.0", {"center": v(-189.96, 189.96) * mm, "radius": 2.5 * mm});
            skLineSegment(sketch, "E134.5.1", {"start": v(-168.75, 189.96) * mm, "end": v(-189.96, 168.75) * mm});
            skCircle(sketch, "E134.5.2", {"center": v(-168.75, 168.75) * mm, "radius": 2.5 * mm});
            skCircle(sketch, "E134.6.0", {"center": v(-268.65, 0) * mm, "radius": 2.5 * mm});
            skLineSegment(sketch, "E134.6.1", {"start": v(-253.65, 15) * mm, "end": v(-253.65, -15) * mm});
            skCircle(sketch, "E134.6.2", {"center": v(-238.65, 0) * mm, "radius": 2.5 * mm});
            skCircle(sketch, "E134.7.0", {"center": v(-189.96, -189.96) * mm, "radius": 2.5 * mm});
            skLineSegment(sketch, "E134.7.1", {"start": v(-189.96, -168.75) * mm, "end": v(-168.75, -189.96) * mm});
            skCircle(sketch, "E134.7.2", {"center": v(-168.75, -168.75) * mm, "radius": 2.5 * mm});
            skSolve(sketch);
        }
        {
            var Q0;
            {var subQ12=sQuery(id+"F6.wireOp",EDGE,"E76.0");Q0=makeQuery(id+"F6.imprint","IMPRINT",FACE,{"disambiguationData":[TD([[makeQuery(id+"F6.imprint","IMPRINT",EDGE,{"derivedFrom":subQ12}),-1.0]])]});}
            extrude(context, id + "F7", {"entities" : qUnion([Q0]), "depth" : 10 * mm, "offsetDistance" : 25 * mm});
        }
        {
            var Q0;
            Q0=qCreatedBy(id+"F1.planeOp",FACE);
            var sketch = newSketch(context, id + "F8", { "sketchPlane" : qUnion([Q0])});
            skCircle(sketch, "E135", {"center": v(0, 0) * mm, "radius": 575 * mm});
            skLineSegment(sketch, "E136.bottom", {"start": v(4.9, 530) * mm, "end": v(1, 530) * mm});
            skLineSegment(sketch, "E136.top", {"start": v(4.9, 540) * mm, "end": v(1, 540) * mm});
            skLineSegment(sketch, "E136.left", {"start": v(4.9, 530) * mm, "end": v(4.9, 540) * mm});
            skLineSegment(sketch, "E136.right", {"start": v(-4.9, 530) * mm, "end": v(-4.9, 540) * mm});
            skPoint(sketch, "E136.middle", {"position": v(0, 535) * mm});
            skLineSegment(sketch, "E137", {"start": v(0, 541) * mm, "end": v(-1, 540) * mm});
            skLineSegment(sketch, "E138", {"start": v(0, 541) * mm, "end": v(1, 540) * mm});
            skLineSegment(sketch, "E139.trimOffspring", {"start": v(-1, 540) * mm, "end": v(-4.9, 540) * mm});
            skLineSegment(sketch, "E140", {"start": v(0, 529) * mm, "end": v(-1, 530) * mm});
            skLineSegment(sketch, "E141", {"start": v(0, 529) * mm, "end": v(1, 530) * mm});
            skLineSegment(sketch, "E142.trimOffspring", {"start": v(-1, 530) * mm, "end": v(-4.9, 530) * mm});
            skPoint(sketch, "E143.2.0", {"position": v(-378.3, 378.3) * mm});
            skLineSegment(sketch, "E143.2.1", {"start": v(-378.23, 371.3) * mm, "end": v(-385.3, 378.37) * mm});
            skLineSegment(sketch, "E143.2.2", {"start": v(-371.3, 378.23) * mm, "end": v(-378.37, 385.3) * mm});
            skLineSegment(sketch, "E143.2.3", {"start": v(-371.3, 378.23) * mm, "end": v(-374.06, 375.47) * mm});
            skLineSegment(sketch, "E143.2.4", {"start": v(-374.06, 374.06) * mm, "end": v(-374.06, 375.47) * mm});
            skLineSegment(sketch, "E143.2.5", {"start": v(-374.06, 374.06) * mm, "end": v(-375.47, 374.06) * mm});
            skLineSegment(sketch, "E143.2.6", {"start": v(-375.47, 374.06) * mm, "end": v(-378.23, 371.3) * mm});
            skLineSegment(sketch, "E143.2.7", {"start": v(-378.37, 385.3) * mm, "end": v(-381.13, 382.54) * mm});
            skLineSegment(sketch, "E143.2.8", {"start": v(-382.54, 381.13) * mm, "end": v(-385.3, 378.37) * mm});
            skLineSegment(sketch, "E143.2.9", {"start": v(-382.54, 382.54) * mm, "end": v(-381.13, 382.54) * mm});
            skLineSegment(sketch, "E143.2.10", {"start": v(-382.54, 382.54) * mm, "end": v(-382.54, 381.13) * mm});
            skPoint(sketch, "E143.4.0", {"position": v(-535, 0) * mm});
            skLineSegment(sketch, "E143.4.1", {"start": v(-530, -4.9) * mm, "end": v(-540, -4.9) * mm});
            skLineSegment(sketch, "E143.4.2", {"start": v(-530, 4.9) * mm, "end": v(-540, 4.9) * mm});
            skLineSegment(sketch, "E143.4.3", {"start": v(-530, 4.9) * mm, "end": v(-530, 1) * mm});
            skLineSegment(sketch, "E143.4.4", {"start": v(-529, 0) * mm, "end": v(-530, 1) * mm});
            skLineSegment(sketch, "E143.4.5", {"start": v(-529, 0) * mm, "end": v(-530, -1) * mm});
            skLineSegment(sketch, "E143.4.6", {"start": v(-530, -1) * mm, "end": v(-530, -4.9) * mm});
            skLineSegment(sketch, "E143.4.7", {"start": v(-540, 4.9) * mm, "end": v(-540, 1) * mm});
            skLineSegment(sketch, "E143.4.8", {"start": v(-540, -1) * mm, "end": v(-540, -4.9) * mm});
            skLineSegment(sketch, "E143.4.9", {"start": v(-541, 0) * mm, "end": v(-540, 1) * mm});
            skLineSegment(sketch, "E143.4.10", {"start": v(-541, 0) * mm, "end": v(-540, -1) * mm});
            skPoint(sketch, "E143.6.0", {"position": v(-378.3, -378.3) * mm});
            skLineSegment(sketch, "E143.6.1", {"start": v(-371.3, -378.23) * mm, "end": v(-378.37, -385.3) * mm});
            skLineSegment(sketch, "E143.6.2", {"start": v(-378.23, -371.3) * mm, "end": v(-385.3, -378.37) * mm});
            skLineSegment(sketch, "E143.6.3", {"start": v(-378.23, -371.3) * mm, "end": v(-375.47, -374.06) * mm});
            skLineSegment(sketch, "E143.6.4", {"start": v(-374.06, -374.06) * mm, "end": v(-375.47, -374.06) * mm});
            skLineSegment(sketch, "E143.6.5", {"start": v(-374.06, -374.06) * mm, "end": v(-374.06, -375.47) * mm});
            skLineSegment(sketch, "E143.6.6", {"start": v(-374.06, -375.47) * mm, "end": v(-371.3, -378.23) * mm});
            skLineSegment(sketch, "E143.6.7", {"start": v(-385.3, -378.37) * mm, "end": v(-382.54, -381.13) * mm});
            skLineSegment(sketch, "E143.6.8", {"start": v(-381.13, -382.54) * mm, "end": v(-378.37, -385.3) * mm});
            skLineSegment(sketch, "E143.6.9", {"start": v(-382.54, -382.54) * mm, "end": v(-382.54, -381.13) * mm});
            skLineSegment(sketch, "E143.6.10", {"start": v(-382.54, -382.54) * mm, "end": v(-381.13, -382.54) * mm});
            skPoint(sketch, "E143.8.0", {"position": v(0, -535) * mm});
            skLineSegment(sketch, "E143.8.1", {"start": v(4.9, -530) * mm, "end": v(4.9, -540) * mm});
            skLineSegment(sketch, "E143.8.2", {"start": v(-4.9, -530) * mm, "end": v(-4.9, -540) * mm});
            skLineSegment(sketch, "E143.8.3", {"start": v(-4.9, -530) * mm, "end": v(-1, -530) * mm});
            skLineSegment(sketch, "E143.8.4", {"start": v(0, -529) * mm, "end": v(-1, -530) * mm});
            skLineSegment(sketch, "E143.8.5", {"start": v(0, -529) * mm, "end": v(1, -530) * mm});
            skLineSegment(sketch, "E143.8.6", {"start": v(1, -530) * mm, "end": v(4.9, -530) * mm});
            skLineSegment(sketch, "E143.8.7", {"start": v(-4.9, -540) * mm, "end": v(-1, -540) * mm});
            skLineSegment(sketch, "E143.8.8", {"start": v(1, -540) * mm, "end": v(4.9, -540) * mm});
            skLineSegment(sketch, "E143.8.9", {"start": v(0, -541) * mm, "end": v(-1, -540) * mm});
            skLineSegment(sketch, "E143.8.10", {"start": v(0, -541) * mm, "end": v(1, -540) * mm});
            skPoint(sketch, "E143.10.0", {"position": v(378.3, -378.3) * mm});
            skLineSegment(sketch, "E143.10.1", {"start": v(378.23, -371.3) * mm, "end": v(385.3, -378.37) * mm});
            skLineSegment(sketch, "E143.10.2", {"start": v(371.3, -378.23) * mm, "end": v(378.37, -385.3) * mm});
            skLineSegment(sketch, "E143.10.3", {"start": v(371.3, -378.23) * mm, "end": v(374.06, -375.47) * mm});
            skLineSegment(sketch, "E143.10.4", {"start": v(374.06, -374.06) * mm, "end": v(374.06, -375.47) * mm});
            skLineSegment(sketch, "E143.10.5", {"start": v(374.06, -374.06) * mm, "end": v(375.47, -374.06) * mm});
            skLineSegment(sketch, "E143.10.6", {"start": v(375.47, -374.06) * mm, "end": v(378.23, -371.3) * mm});
            skLineSegment(sketch, "E143.10.7", {"start": v(378.37, -385.3) * mm, "end": v(381.13, -382.54) * mm});
            skLineSegment(sketch, "E143.10.8", {"start": v(382.54, -381.13) * mm, "end": v(385.3, -378.37) * mm});
            skLineSegment(sketch, "E143.10.9", {"start": v(382.54, -382.54) * mm, "end": v(381.13, -382.54) * mm});
            skLineSegment(sketch, "E143.10.10", {"start": v(382.54, -382.54) * mm, "end": v(382.54, -381.13) * mm});
            skPoint(sketch, "E143.12.0", {"position": v(535, 0) * mm});
            skLineSegment(sketch, "E143.12.1", {"start": v(530, 4.9) * mm, "end": v(540, 4.9) * mm});
            skLineSegment(sketch, "E143.12.2", {"start": v(530, -4.9) * mm, "end": v(540, -4.9) * mm});
            skLineSegment(sketch, "E143.12.3", {"start": v(530, -4.9) * mm, "end": v(530, -1) * mm});
            skLineSegment(sketch, "E143.12.4", {"start": v(529, 0) * mm, "end": v(530, -1) * mm});
            skLineSegment(sketch, "E143.12.5", {"start": v(529, 0) * mm, "end": v(530, 1) * mm});
            skLineSegment(sketch, "E143.12.6", {"start": v(530, 1) * mm, "end": v(530, 4.9) * mm});
            skLineSegment(sketch, "E143.12.7", {"start": v(540, -4.9) * mm, "end": v(540, -1) * mm});
            skLineSegment(sketch, "E143.12.8", {"start": v(540, 1) * mm, "end": v(540, 4.9) * mm});
            skLineSegment(sketch, "E143.12.9", {"start": v(541, 0) * mm, "end": v(540, -1) * mm});
            skLineSegment(sketch, "E143.12.10", {"start": v(541, 0) * mm, "end": v(540, 1) * mm});
            skPoint(sketch, "E143.14.0", {"position": v(378.3, 378.3) * mm});
            skLineSegment(sketch, "E143.14.1", {"start": v(371.3, 378.23) * mm, "end": v(378.37, 385.3) * mm});
            skLineSegment(sketch, "E143.14.2", {"start": v(378.23, 371.3) * mm, "end": v(385.3, 378.37) * mm});
            skLineSegment(sketch, "E143.14.3", {"start": v(378.23, 371.3) * mm, "end": v(375.47, 374.06) * mm});
            skLineSegment(sketch, "E143.14.4", {"start": v(374.06, 374.06) * mm, "end": v(375.47, 374.06) * mm});
            skLineSegment(sketch, "E143.14.5", {"start": v(374.06, 374.06) * mm, "end": v(374.06, 375.47) * mm});
            skLineSegment(sketch, "E143.14.6", {"start": v(374.06, 375.47) * mm, "end": v(371.3, 378.23) * mm});
            skLineSegment(sketch, "E143.14.7", {"start": v(385.3, 378.37) * mm, "end": v(382.54, 381.13) * mm});
            skLineSegment(sketch, "E143.14.8", {"start": v(381.13, 382.54) * mm, "end": v(378.37, 385.3) * mm});
            skLineSegment(sketch, "E143.14.9", {"start": v(382.54, 382.54) * mm, "end": v(382.54, 381.13) * mm});
            skLineSegment(sketch, "E143.14.10", {"start": v(382.54, 382.54) * mm, "end": v(381.13, 382.54) * mm});
            skCircle(sketch, "E144", {"center": v(0, 0) * mm, "radius": 475 * mm});
            skLineSegment(sketch, "E145.bottom", {"start": v(4.9, 500) * mm, "end": v(1, 500) * mm});
            skLineSegment(sketch, "E145.top", {"start": v(4.9, 510) * mm, "end": v(1, 510) * mm});
            skLineSegment(sketch, "E145.left", {"start": v(4.9, 500) * mm, "end": v(4.9, 510) * mm});
            skLineSegment(sketch, "E145.right", {"start": v(-4.9, 500) * mm, "end": v(-4.9, 510) * mm});
            skPoint(sketch, "E145.middle", {"position": v(0, 505) * mm});
            skLineSegment(sketch, "E146", {"start": v(0, 511) * mm, "end": v(-1, 510) * mm});
            skLineSegment(sketch, "E147", {"start": v(0, 511) * mm, "end": v(1, 510) * mm});
            skLineSegment(sketch, "E148.trimOffspring", {"start": v(-1, 510) * mm, "end": v(-4.9, 510) * mm});
            skLineSegment(sketch, "E149", {"start": v(0, 499) * mm, "end": v(-1, 500) * mm});
            skLineSegment(sketch, "E150", {"start": v(0, 499) * mm, "end": v(1, 500) * mm});
            skLineSegment(sketch, "E151.trimOffspring", {"start": v(-1, 500) * mm, "end": v(-4.9, 500) * mm});
            skLineSegment(sketch, "E152.1.0", {"start": v(-350.09, 357.02) * mm, "end": v(-357.16, 364.09) * mm});
            skPoint(sketch, "E152.1.1", {"position": v(-357.09, 357.09) * mm});
            skLineSegment(sketch, "E152.1.2", {"start": v(-357.02, 350.09) * mm, "end": v(-364.09, 357.16) * mm});
            skLineSegment(sketch, "E152.1.3", {"start": v(-357.16, 364.09) * mm, "end": v(-359.92, 361.33) * mm});
            skLineSegment(sketch, "E152.1.4", {"start": v(-350.09, 357.02) * mm, "end": v(-352.85, 354.26) * mm});
            skLineSegment(sketch, "E152.1.5", {"start": v(-361.33, 361.33) * mm, "end": v(-361.33, 359.92) * mm});
            skLineSegment(sketch, "E152.1.6", {"start": v(-361.33, 361.33) * mm, "end": v(-359.92, 361.33) * mm});
            skLineSegment(sketch, "E152.1.7", {"start": v(-354.26, 352.85) * mm, "end": v(-357.02, 350.09) * mm});
            skLineSegment(sketch, "E152.1.8", {"start": v(-361.33, 359.92) * mm, "end": v(-364.09, 357.16) * mm});
            skLineSegment(sketch, "E152.1.9", {"start": v(-352.85, 352.85) * mm, "end": v(-352.85, 354.26) * mm});
            skLineSegment(sketch, "E152.1.10", {"start": v(-352.85, 352.85) * mm, "end": v(-354.26, 352.85) * mm});
            skLineSegment(sketch, "E152.2.0", {"start": v(-500, 4.9) * mm, "end": v(-510, 4.9) * mm});
            skPoint(sketch, "E152.2.1", {"position": v(-505, 0) * mm});
            skLineSegment(sketch, "E152.2.2", {"start": v(-500, -4.9) * mm, "end": v(-510, -4.9) * mm});
            skLineSegment(sketch, "E152.2.3", {"start": v(-510, 4.9) * mm, "end": v(-510, 1) * mm});
            skLineSegment(sketch, "E152.2.4", {"start": v(-500, 4.9) * mm, "end": v(-500, 1) * mm});
            skLineSegment(sketch, "E152.2.5", {"start": v(-511, 0) * mm, "end": v(-510, -1) * mm});
            skLineSegment(sketch, "E152.2.6", {"start": v(-511, 0) * mm, "end": v(-510, 1) * mm});
            skLineSegment(sketch, "E152.2.7", {"start": v(-500, -1) * mm, "end": v(-500, -4.9) * mm});
            skLineSegment(sketch, "E152.2.8", {"start": v(-510, -1) * mm, "end": v(-510, -4.9) * mm});
            skLineSegment(sketch, "E152.2.9", {"start": v(-499, 0) * mm, "end": v(-500, 1) * mm});
            skLineSegment(sketch, "E152.2.10", {"start": v(-499, 0) * mm, "end": v(-500, -1) * mm});
            skLineSegment(sketch, "E152.3.0", {"start": v(-357.02, -350.09) * mm, "end": v(-364.09, -357.16) * mm});
            skPoint(sketch, "E152.3.1", {"position": v(-357.09, -357.09) * mm});
            skLineSegment(sketch, "E152.3.2", {"start": v(-350.09, -357.02) * mm, "end": v(-357.16, -364.09) * mm});
            skLineSegment(sketch, "E152.3.3", {"start": v(-364.09, -357.16) * mm, "end": v(-361.33, -359.92) * mm});
            skLineSegment(sketch, "E152.3.4", {"start": v(-357.02, -350.09) * mm, "end": v(-354.26, -352.85) * mm});
            skLineSegment(sketch, "E152.3.5", {"start": v(-361.33, -361.33) * mm, "end": v(-359.92, -361.33) * mm});
            skLineSegment(sketch, "E152.3.6", {"start": v(-361.33, -361.33) * mm, "end": v(-361.33, -359.92) * mm});
            skLineSegment(sketch, "E152.3.7", {"start": v(-352.85, -354.26) * mm, "end": v(-350.09, -357.02) * mm});
            skLineSegment(sketch, "E152.3.8", {"start": v(-359.92, -361.33) * mm, "end": v(-357.16, -364.09) * mm});
            skLineSegment(sketch, "E152.3.9", {"start": v(-352.85, -352.85) * mm, "end": v(-354.26, -352.85) * mm});
            skLineSegment(sketch, "E152.3.10", {"start": v(-352.85, -352.85) * mm, "end": v(-352.85, -354.26) * mm});
            skLineSegment(sketch, "E152.4.0", {"start": v(-4.9, -500) * mm, "end": v(-4.9, -510) * mm});
            skPoint(sketch, "E152.4.1", {"position": v(0, -505) * mm});
            skLineSegment(sketch, "E152.4.2", {"start": v(4.9, -500) * mm, "end": v(4.9, -510) * mm});
            skLineSegment(sketch, "E152.4.3", {"start": v(-4.9, -510) * mm, "end": v(-1, -510) * mm});
            skLineSegment(sketch, "E152.4.4", {"start": v(-4.9, -500) * mm, "end": v(-1, -500) * mm});
            skLineSegment(sketch, "E152.4.5", {"start": v(0, -511) * mm, "end": v(1, -510) * mm});
            skLineSegment(sketch, "E152.4.6", {"start": v(0, -511) * mm, "end": v(-1, -510) * mm});
            skLineSegment(sketch, "E152.4.7", {"start": v(1, -500) * mm, "end": v(4.9, -500) * mm});
            skLineSegment(sketch, "E152.4.8", {"start": v(1, -510) * mm, "end": v(4.9, -510) * mm});
            skLineSegment(sketch, "E152.4.9", {"start": v(0, -499) * mm, "end": v(-1, -500) * mm});
            skLineSegment(sketch, "E152.4.10", {"start": v(0, -499) * mm, "end": v(1, -500) * mm});
            skLineSegment(sketch, "E152.5.0", {"start": v(350.09, -357.02) * mm, "end": v(357.16, -364.09) * mm});
            skPoint(sketch, "E152.5.1", {"position": v(357.09, -357.09) * mm});
            skLineSegment(sketch, "E152.5.2", {"start": v(357.02, -350.09) * mm, "end": v(364.09, -357.16) * mm});
            skLineSegment(sketch, "E152.5.3", {"start": v(357.16, -364.09) * mm, "end": v(359.92, -361.33) * mm});
            skLineSegment(sketch, "E152.5.4", {"start": v(350.09, -357.02) * mm, "end": v(352.85, -354.26) * mm});
            skLineSegment(sketch, "E152.5.5", {"start": v(361.33, -361.33) * mm, "end": v(361.33, -359.92) * mm});
            skLineSegment(sketch, "E152.5.6", {"start": v(361.33, -361.33) * mm, "end": v(359.92, -361.33) * mm});
            skLineSegment(sketch, "E152.5.7", {"start": v(354.26, -352.85) * mm, "end": v(357.02, -350.09) * mm});
            skLineSegment(sketch, "E152.5.8", {"start": v(361.33, -359.92) * mm, "end": v(364.09, -357.16) * mm});
            skLineSegment(sketch, "E152.5.9", {"start": v(352.85, -352.85) * mm, "end": v(352.85, -354.26) * mm});
            skLineSegment(sketch, "E152.5.10", {"start": v(352.85, -352.85) * mm, "end": v(354.26, -352.85) * mm});
            skLineSegment(sketch, "E152.6.0", {"start": v(500, -4.9) * mm, "end": v(510, -4.9) * mm});
            skPoint(sketch, "E152.6.1", {"position": v(505, 0) * mm});
            skLineSegment(sketch, "E152.6.2", {"start": v(500, 4.9) * mm, "end": v(510, 4.9) * mm});
            skLineSegment(sketch, "E152.6.3", {"start": v(510, -4.9) * mm, "end": v(510, -1) * mm});
            skLineSegment(sketch, "E152.6.4", {"start": v(500, -4.9) * mm, "end": v(500, -1) * mm});
            skLineSegment(sketch, "E152.6.5", {"start": v(511, 0) * mm, "end": v(510, 1) * mm});
            skLineSegment(sketch, "E152.6.6", {"start": v(511, 0) * mm, "end": v(510, -1) * mm});
            skLineSegment(sketch, "E152.6.7", {"start": v(500, 1) * mm, "end": v(500, 4.9) * mm});
            skLineSegment(sketch, "E152.6.8", {"start": v(510, 1) * mm, "end": v(510, 4.9) * mm});
            skLineSegment(sketch, "E152.6.9", {"start": v(499, 0) * mm, "end": v(500, -1) * mm});
            skLineSegment(sketch, "E152.6.10", {"start": v(499, 0) * mm, "end": v(500, 1) * mm});
            skLineSegment(sketch, "E152.7.0", {"start": v(357.02, 350.09) * mm, "end": v(364.09, 357.16) * mm});
            skPoint(sketch, "E152.7.1", {"position": v(357.09, 357.09) * mm});
            skLineSegment(sketch, "E152.7.2", {"start": v(350.09, 357.02) * mm, "end": v(357.16, 364.09) * mm});
            skLineSegment(sketch, "E152.7.3", {"start": v(364.09, 357.16) * mm, "end": v(361.33, 359.92) * mm});
            skLineSegment(sketch, "E152.7.4", {"start": v(357.02, 350.09) * mm, "end": v(354.26, 352.85) * mm});
            skLineSegment(sketch, "E152.7.5", {"start": v(361.33, 361.33) * mm, "end": v(359.92, 361.33) * mm});
            skLineSegment(sketch, "E152.7.6", {"start": v(361.33, 361.33) * mm, "end": v(361.33, 359.92) * mm});
            skLineSegment(sketch, "E152.7.7", {"start": v(352.85, 354.26) * mm, "end": v(350.09, 357.02) * mm});
            skLineSegment(sketch, "E152.7.8", {"start": v(359.92, 361.33) * mm, "end": v(357.16, 364.09) * mm});
            skLineSegment(sketch, "E152.7.9", {"start": v(352.85, 352.85) * mm, "end": v(354.26, 352.85) * mm});
            skLineSegment(sketch, "E152.7.10", {"start": v(352.85, 352.85) * mm, "end": v(352.85, 354.26) * mm});
            skSolve(sketch);
        }
        {
            var Q0;
            Q0=qSketchRegion(id+"F8",true);
            extrude(context, id + "F9", {"entities" : qUnion([Q0]), "depth" : 10 * mm, "offsetDistance" : 25 * mm});
        }
        {
            var Q0;
            Q0=qCreatedBy(makeId("Right.planeOp"),FACE);
            var sketch = newSketch(context, id + "F10", { "sketchPlane" : qUnion([Q0])});
            skLineSegment(sketch, "E153.0.1", {"start": v(540, 0) * mm, "end": v(540, 10) * mm});
            skLineSegment(sketch, "E153.0.2", {"start": v(540, 10) * mm, "end": v(530, 10) * mm});
            skLineSegment(sketch, "E153.0.3", {"start": v(530, 10) * mm, "end": v(530, 0) * mm});
            skLineSegment(sketch, "E154.0.0", {"start": v(530, -200) * mm, "end": v(540, -200) * mm});
            skLineSegment(sketch, "E154.0.1", {"start": v(540, -200) * mm, "end": v(540, -190) * mm});
            skLineSegment(sketch, "E154.0.3", {"start": v(530, -190) * mm, "end": v(530, -200) * mm});
            skLineSegment(sketch, "E155", {"start": v(530, 0) * mm, "end": v(520, 0) * mm});
            skLineSegment(sketch, "E156", {"start": v(520, 0) * mm, "end": v(520, -90.1) * mm});
            skLineSegment(sketch, "E157", {"start": v(520, -190) * mm, "end": v(530, -190) * mm});
            skLineSegment(sketch, "E158", {"start": v(540, -190) * mm, "end": v(550, -190) * mm});
            skLineSegment(sketch, "E159", {"start": v(550, -190) * mm, "end": v(550, 0) * mm});
            skLineSegment(sketch, "E160", {"start": v(550, 0) * mm, "end": v(540, 0) * mm});
            skLineSegment(sketch, "E161.0.0", {"start": v(290, 0) * mm, "end": v(300, 0) * mm});
            skLineSegment(sketch, "E161.0.1", {"start": v(300, 0) * mm, "end": v(300, 10) * mm});
            skLineSegment(sketch, "E161.0.3", {"start": v(290, 10) * mm, "end": v(290, 0) * mm});
            skLineSegment(sketch, "E162.0.1", {"start": v(300, 200) * mm, "end": v(300, 210) * mm});
            skLineSegment(sketch, "E162.0.2", {"start": v(300, 210) * mm, "end": v(290, 210) * mm});
            skLineSegment(sketch, "E162.0.3", {"start": v(290, 210) * mm, "end": v(290, 200) * mm});
            skLineSegment(sketch, "E163", {"start": v(290, 200) * mm, "end": v(280, 200) * mm});
            skLineSegment(sketch, "E164", {"start": v(280, 200) * mm, "end": v(280, 109.9) * mm});
            skLineSegment(sketch, "E165", {"start": v(280, 10) * mm, "end": v(290, 10) * mm});
            skLineSegment(sketch, "E166", {"start": v(300, 10) * mm, "end": v(310, 10) * mm});
            skLineSegment(sketch, "E167", {"start": v(310, 10) * mm, "end": v(310, 200) * mm});
            skLineSegment(sketch, "E168", {"start": v(310, 200) * mm, "end": v(300, 200) * mm});
            skLineSegment(sketch, "E169", {"start": v(280, 109.9) * mm, "end": v(290, 109.9) * mm});
            skLineSegment(sketch, "E170", {"start": v(290, 109.9) * mm, "end": v(290, 100.1) * mm});
            skLineSegment(sketch, "E171", {"start": v(290, 100.1) * mm, "end": v(280, 100.1) * mm});
            skLineSegment(sketch, "E172.trimOffspring", {"start": v(280, 100.1) * mm, "end": v(280, 10) * mm});
            skLineSegment(sketch, "E173", {"start": v(520, -90.1) * mm, "end": v(530, -90.1) * mm});
            skLineSegment(sketch, "E174", {"start": v(530, -90.1) * mm, "end": v(530, -99.9) * mm});
            skLineSegment(sketch, "E175", {"start": v(530, -99.9) * mm, "end": v(520, -99.9) * mm});
            skLineSegment(sketch, "E176.trimOffspring", {"start": v(520, -99.9) * mm, "end": v(520, -190) * mm});
            skLineSegment(sketch, "E177.0", {"start": v(-475, -190) * mm, "end": v(475, -190) * mm, "construction": true});
            skLineSegment(sketch, "E178", {"start": v(513.03, -190) * mm, "end": v(510, -190) * mm});
            skLineSegment(sketch, "E179", {"start": v(510, -190) * mm, "end": v(510, -200) * mm});
            skLineSegment(sketch, "E180", {"start": v(510, -200) * mm, "end": v(500, -200) * mm});
            skLineSegment(sketch, "E181", {"start": v(500, -200) * mm, "end": v(500, -190) * mm});
            skLineSegment(sketch, "E182", {"start": v(500, -190) * mm, "end": v(490, -190) * mm});
            skLineSegment(sketch, "E183", {"start": v(320, 10) * mm, "end": v(320, 0) * mm});
            skLineSegment(sketch, "E184", {"start": v(330, 0) * mm, "end": v(330, 10) * mm});
            skLineSegment(sketch, "E185", {"start": v(330, 10) * mm, "end": v(320, 10) * mm});
            skLineSegment(sketch, "E186", {"start": v(320, 0) * mm, "end": v(310, 0) * mm});
            skLineSegment(sketch, "E187", {"start": v(330, 0) * mm, "end": v(340, 0) * mm});
            skLineSegment(sketch, "E188", {"start": v(340, 0) * mm, "end": v(515.2, -184.94) * mm});
            skLineSegment(sketch, "E189", {"start": v(490, -190) * mm, "end": v(310, 0) * mm});
            skPoint(sketch, "E190.visualSharp", {"position": v(520, -190) * mm});
            skArc(sketch, "E190.filletArc", {"start": v(513.03, -190) * mm, "mid": v(515.78, -188.19) * mm, "end": v(515.2, -184.94) * mm});
            skSolve(sketch);
        }
        {
            var Q0;
            Q0=qSketchRegion(id+"F10",true);
            extrude(context, id + "F11", {"entities" : qUnion([Q0]), "endBound" : BoundingType.SYMMETRIC, "depth" : 10 * mm, "offsetDistance" : 25 * mm});
        }
        {
            var Q0;
            Q0=makeQuery(id+"F11.opExtrude","SWEPT_BODY",BODY,{"disambiguationData":[OSD([sQuery(id+"F10.wireOp",EDGE,"E153.0.1"),sQuery(id+"F10.wireOp",EDGE,"E153.0.2"),sQuery(id+"F10.wireOp",EDGE,"E153.0.3"),sQuery(id+"F10.wireOp",EDGE,"E154.0.0"),sQuery(id+"F10.wireOp",EDGE,"E154.0.1"),sQuery(id+"F10.wireOp",EDGE,"E154.0.3"),sQuery(id+"F10.wireOp",EDGE,"E155"),sQuery(id+"F10.wireOp",EDGE,"E156"),sQuery(id+"F10.wireOp",EDGE,"E157"),sQuery(id+"F10.wireOp",EDGE,"E158"),sQuery(id+"F10.wireOp",EDGE,"E159"),sQuery(id+"F10.wireOp",EDGE,"E160")])]});
            var Q1;
            Q1=makeQuery(id+"F11.opExtrude","SWEPT_BODY",BODY,{"disambiguationData":[OSD([sQuery(id+"F10.wireOp",EDGE,"E161.0.0"),sQuery(id+"F10.wireOp",EDGE,"E161.0.1"),sQuery(id+"F10.wireOp",EDGE,"E161.0.3"),sQuery(id+"F10.wireOp",EDGE,"E162.0.1"),sQuery(id+"F10.wireOp",EDGE,"E162.0.2"),sQuery(id+"F10.wireOp",EDGE,"E162.0.3"),sQuery(id+"F10.wireOp",EDGE,"E163"),sQuery(id+"F10.wireOp",EDGE,"E164"),sQuery(id+"F10.wireOp",EDGE,"E165"),sQuery(id+"F10.wireOp",EDGE,"E166"),sQuery(id+"F10.wireOp",EDGE,"E167"),sQuery(id+"F10.wireOp",EDGE,"E168")])]});
            var Q2;
            Q2=makeQuery(id+"F7.opExtrude","CAP_EDGE",EDGE,{"disambiguationData":[OSD([sQuery(id+"F6.wireOp",EDGE,"E80")])],"isStart":true});
            circularPattern(context, id + "F12", {"operationType" : NewBodyOperationType.ADD, "entities" : qUnion([Q0, Q1]), "axis" : qUnion([Q2]), "angle" : 360 * degree, "instanceCount" : 8, "equalSpace" : true});
        }
        {
            var Q0;
            Q0=qCreatedBy(id+"F2.planeOp",FACE);
            var sketch = newSketch(context, id + "F13", { "sketchPlane" : qUnion([Q0])});
            skPoint(sketch, "E191.0", {"position": v(-520, 0) * mm});
            skPoint(sketch, "E192.0", {"position": v(-540, 0) * mm});
            skPoint(sketch, "E193.0", {"position": v(-530, -5) * mm});
            skPoint(sketch, "E194.0", {"position": v(-530, 5) * mm});
            skArc(sketch, "E195", {"start": v(-539.98, -5) * mm, "mid": v(-498.9, -206.65) * mm, "end": v(-385.36, -378.29) * mm});
            skCircle(sketch, "E196", {"center": v(0, 0) * mm, "radius": 520 * mm});
            skLineSegment(sketch, "E197", {"start": v(-530, 5) * mm, "end": v(-530, -5) * mm});
            skLineSegment(sketch, "E198", {"start": v(-530, 5) * mm, "end": v(-539.98, 5) * mm});
            skLineSegment(sketch, "E199", {"start": v(-530, -5) * mm, "end": v(-539.98, -5) * mm});
            skLineSegment(sketch, "E200", {"start": v(-540, 0) * mm, "end": v(-520, 0) * mm, "construction": true});
            skLineSegment(sketch, "E201.1.0", {"start": v(-378.3, -371.23) * mm, "end": v(-385.36, -378.29) * mm});
            skLineSegment(sketch, "E201.1.1", {"start": v(-378.3, -371.23) * mm, "end": v(-371.23, -378.3) * mm});
            skLineSegment(sketch, "E201.1.2", {"start": v(-381.84, -381.84) * mm, "end": v(-367.7, -367.7) * mm, "construction": true});
            skLineSegment(sketch, "E201.1.3", {"start": v(-371.23, -378.3) * mm, "end": v(-378.29, -385.36) * mm});
            skLineSegment(sketch, "E201.2.0", {"start": v(-5, -530) * mm, "end": v(-5, -539.98) * mm});
            skLineSegment(sketch, "E201.2.1", {"start": v(-5, -530) * mm, "end": v(5, -530) * mm});
            skLineSegment(sketch, "E201.2.2", {"start": v(0, -540) * mm, "end": v(0, -520) * mm, "construction": true});
            skLineSegment(sketch, "E201.2.3", {"start": v(5, -530) * mm, "end": v(5, -539.98) * mm});
            skLineSegment(sketch, "E201.3.0", {"start": v(371.23, -378.3) * mm, "end": v(378.29, -385.36) * mm});
            skLineSegment(sketch, "E201.3.1", {"start": v(371.23, -378.3) * mm, "end": v(378.3, -371.23) * mm});
            skLineSegment(sketch, "E201.3.2", {"start": v(381.84, -381.84) * mm, "end": v(367.7, -367.7) * mm, "construction": true});
            skLineSegment(sketch, "E201.3.3", {"start": v(378.3, -371.23) * mm, "end": v(385.36, -378.29) * mm});
            skLineSegment(sketch, "E201.4.0", {"start": v(530, -5) * mm, "end": v(539.98, -5) * mm});
            skLineSegment(sketch, "E201.4.1", {"start": v(530, -5) * mm, "end": v(530, 5) * mm});
            skLineSegment(sketch, "E201.4.2", {"start": v(540, 0) * mm, "end": v(520, 0) * mm, "construction": true});
            skLineSegment(sketch, "E201.4.3", {"start": v(530, 5) * mm, "end": v(539.98, 5) * mm});
            skLineSegment(sketch, "E201.5.0", {"start": v(378.3, 371.23) * mm, "end": v(385.36, 378.29) * mm});
            skLineSegment(sketch, "E201.5.1", {"start": v(378.3, 371.23) * mm, "end": v(371.23, 378.3) * mm});
            skLineSegment(sketch, "E201.5.2", {"start": v(381.84, 381.84) * mm, "end": v(367.7, 367.7) * mm, "construction": true});
            skLineSegment(sketch, "E201.5.3", {"start": v(371.23, 378.3) * mm, "end": v(378.29, 385.36) * mm});
            skLineSegment(sketch, "E201.6.0", {"start": v(5, 530) * mm, "end": v(5, 539.98) * mm});
            skLineSegment(sketch, "E201.6.1", {"start": v(5, 530) * mm, "end": v(-5, 530) * mm});
            skLineSegment(sketch, "E201.6.2", {"start": v(0, 540) * mm, "end": v(0, 520) * mm, "construction": true});
            skLineSegment(sketch, "E201.6.3", {"start": v(-5, 530) * mm, "end": v(-5, 539.98) * mm});
            skLineSegment(sketch, "E201.7.0", {"start": v(-371.23, 378.3) * mm, "end": v(-378.29, 385.36) * mm});
            skLineSegment(sketch, "E201.7.1", {"start": v(-371.23, 378.3) * mm, "end": v(-378.3, 371.23) * mm});
            skLineSegment(sketch, "E201.7.2", {"start": v(-381.84, 381.84) * mm, "end": v(-367.7, 367.7) * mm, "construction": true});
            skLineSegment(sketch, "E201.7.3", {"start": v(-378.3, 371.23) * mm, "end": v(-385.36, 378.29) * mm});
            skArc(sketch, "E202.trimOffspring", {"start": v(-385.36, 378.29) * mm, "mid": v(-498.9, 206.65) * mm, "end": v(-539.98, 5) * mm});
            skArc(sketch, "E203.trimOffspring", {"start": v(-5, 539.98) * mm, "mid": v(-206.65, 498.9) * mm, "end": v(-378.29, 385.36) * mm});
            skArc(sketch, "E204.trimOffspring", {"start": v(378.29, 385.36) * mm, "mid": v(206.65, 498.9) * mm, "end": v(5, 539.98) * mm});
            skArc(sketch, "E205.trimOffspring", {"start": v(539.98, 5) * mm, "mid": v(498.9, 206.65) * mm, "end": v(385.36, 378.29) * mm});
            skArc(sketch, "E206.trimOffspring", {"start": v(385.36, -378.29) * mm, "mid": v(498.9, -206.65) * mm, "end": v(539.98, -5) * mm});
            skArc(sketch, "E207.trimOffspring", {"start": v(5, -539.98) * mm, "mid": v(206.65, -498.9) * mm, "end": v(378.29, -385.36) * mm});
            skArc(sketch, "E208.trimOffspring", {"start": v(-378.29, -385.36) * mm, "mid": v(-206.65, -498.9) * mm, "end": v(-5, -539.98) * mm});
            skSolve(sketch);
        }
        {
            var Q0;
            Q0=qSketchRegion(id+"F13",true);
            extrude(context, id + "F14", {"entities" : qUnion([Q0]), "depth" : 10 * mm, "offsetDistance" : 25 * mm});
        }
        {
            var Q0;
            Q0=qCreatedBy(id+"F3.planeOp",FACE);
            var sketch = newSketch(context, id + "F15", { "sketchPlane" : qUnion([Q0])});
            skPoint(sketch, "E209.0", {"position": v(-280, 0) * mm});
            skPoint(sketch, "E210.0", {"position": v(-290, -5) * mm});
            skPoint(sketch, "E211.0", {"position": v(-290, 5) * mm});
            skPoint(sketch, "E212.0", {"position": v(-300, 0) * mm});
            skArc(sketch, "E213", {"start": v(-299.96, -5) * mm, "mid": v(-277.16, -114.8) * mm, "end": v(-215.64, -208.57) * mm});
            skCircle(sketch, "E214", {"center": v(0, 0) * mm, "radius": 280 * mm});
            skLineSegment(sketch, "E215", {"start": v(-290, 5) * mm, "end": v(-290, -5) * mm});
            skLineSegment(sketch, "E216", {"start": v(-290, -5) * mm, "end": v(-299.96, -5) * mm});
            skLineSegment(sketch, "E217", {"start": v(-290, 5) * mm, "end": v(-299.96, 5) * mm});
            skLineSegment(sketch, "E218.1.0", {"start": v(-208.6, -201.53) * mm, "end": v(-215.64, -208.57) * mm});
            skLineSegment(sketch, "E218.1.1", {"start": v(-208.6, -201.53) * mm, "end": v(-201.53, -208.6) * mm});
            skLineSegment(sketch, "E218.1.2", {"start": v(-201.53, -208.6) * mm, "end": v(-208.57, -215.64) * mm});
            skLineSegment(sketch, "E218.2.0", {"start": v(-5, -290) * mm, "end": v(-5, -299.96) * mm});
            skLineSegment(sketch, "E218.2.1", {"start": v(-5, -290) * mm, "end": v(5, -290) * mm});
            skLineSegment(sketch, "E218.2.2", {"start": v(5, -290) * mm, "end": v(5, -299.96) * mm});
            skLineSegment(sketch, "E218.3.0", {"start": v(201.53, -208.6) * mm, "end": v(208.57, -215.64) * mm});
            skLineSegment(sketch, "E218.3.1", {"start": v(201.53, -208.6) * mm, "end": v(208.6, -201.53) * mm});
            skLineSegment(sketch, "E218.3.2", {"start": v(208.6, -201.53) * mm, "end": v(215.64, -208.57) * mm});
            skLineSegment(sketch, "E218.4.0", {"start": v(290, -5) * mm, "end": v(299.96, -5) * mm});
            skLineSegment(sketch, "E218.4.1", {"start": v(290, -5) * mm, "end": v(290, 5) * mm});
            skLineSegment(sketch, "E218.4.2", {"start": v(290, 5) * mm, "end": v(299.96, 5) * mm});
            skLineSegment(sketch, "E218.5.0", {"start": v(208.6, 201.53) * mm, "end": v(215.64, 208.57) * mm});
            skLineSegment(sketch, "E218.5.1", {"start": v(208.6, 201.53) * mm, "end": v(201.53, 208.6) * mm});
            skLineSegment(sketch, "E218.5.2", {"start": v(201.53, 208.6) * mm, "end": v(208.57, 215.64) * mm});
            skLineSegment(sketch, "E218.6.0", {"start": v(5, 290) * mm, "end": v(5, 299.96) * mm});
            skLineSegment(sketch, "E218.6.1", {"start": v(5, 290) * mm, "end": v(-5, 290) * mm});
            skLineSegment(sketch, "E218.6.2", {"start": v(-5, 290) * mm, "end": v(-5, 299.96) * mm});
            skLineSegment(sketch, "E218.7.0", {"start": v(-201.53, 208.6) * mm, "end": v(-208.57, 215.64) * mm});
            skLineSegment(sketch, "E218.7.1", {"start": v(-201.53, 208.6) * mm, "end": v(-208.6, 201.53) * mm});
            skLineSegment(sketch, "E218.7.2", {"start": v(-208.6, 201.53) * mm, "end": v(-215.64, 208.57) * mm});
            skArc(sketch, "E219.trimOffspring", {"start": v(-215.64, 208.57) * mm, "mid": v(-277.16, 114.8) * mm, "end": v(-299.96, 5) * mm});
            skArc(sketch, "E220.trimOffspring", {"start": v(-5, 299.96) * mm, "mid": v(-114.8, 277.16) * mm, "end": v(-208.57, 215.64) * mm});
            skArc(sketch, "E221.trimOffspring", {"start": v(208.57, 215.64) * mm, "mid": v(114.8, 277.16) * mm, "end": v(5, 299.96) * mm});
            skArc(sketch, "E222.trimOffspring", {"start": v(299.96, 5) * mm, "mid": v(277.16, 114.8) * mm, "end": v(215.64, 208.57) * mm});
            skArc(sketch, "E223.trimOffspring", {"start": v(215.64, -208.57) * mm, "mid": v(277.16, -114.8) * mm, "end": v(299.96, -5) * mm});
            skArc(sketch, "E224.trimOffspring", {"start": v(5, -299.96) * mm, "mid": v(114.8, -277.16) * mm, "end": v(208.57, -215.64) * mm});
            skArc(sketch, "E225.trimOffspring", {"start": v(-208.57, -215.64) * mm, "mid": v(-114.8, -277.16) * mm, "end": v(-5, -299.96) * mm});
            skSolve(sketch);
        }
        {
            var Q0;
            Q0=qSketchRegion(id+"F15",true);
            extrude(context, id + "F16", {"entities" : qUnion([Q0]), "depth" : 10 * mm, "offsetDistance" : 25 * mm});
        }
        {
            var Q0;
            Q0=makeQuery(id+"F11.opExtrude","SWEPT_BODY",BODY,{"disambiguationData":[OSD([sQuery(id+"F10.wireOp",EDGE,"E178"),sQuery(id+"F10.wireOp",EDGE,"E179"),sQuery(id+"F10.wireOp",EDGE,"E180"),sQuery(id+"F10.wireOp",EDGE,"E181"),sQuery(id+"F10.wireOp",EDGE,"E182"),sQuery(id+"F10.wireOp",EDGE,"E183"),sQuery(id+"F10.wireOp",EDGE,"E184"),sQuery(id+"F10.wireOp",EDGE,"E185"),sQuery(id+"F10.wireOp",EDGE,"E186"),sQuery(id+"F10.wireOp",EDGE,"E187"),sQuery(id+"F10.wireOp",EDGE,"E188"),sQuery(id+"F10.wireOp",EDGE,"E189"),sQuery(id+"F10.wireOp",EDGE,"E190.filletArc")])]});
            var Q1;
            Q1=makeQuery(id+"F5.opExtrude","CAP_EDGE",EDGE,{"disambiguationData":[OSD([sQuery(id+"F4.wireOp",EDGE,"E5")])],"isStart":true});
            circularPattern(context, id + "F17", {"operationType" : NewBodyOperationType.ADD, "entities" : qUnion([Q0]), "axis" : qUnion([Q1]), "angle" : 360 * degree, "instanceCount" : 8, "equalSpace" : true});
        }
        {
            var Q0;
            Q0=makeQuery(id+"F5.opExtrude","CAP_FACE",FACE,{"disambiguationData":[OSD([sQuery(id+"F4.wireOp",EDGE,"E0"),sQuery(id+"F4.wireOp",EDGE,"E1"),sQuery(id+"F4.wireOp",EDGE,"E2"),sQuery(id+"F4.wireOp",EDGE,"E3"),sQuery(id+"F4.wireOp",EDGE,"E4"),sQuery(id+"F4.wireOp",EDGE,"E5"),sQuery(id+"F4.wireOp",EDGE,"E12"),sQuery(id+"F4.wireOp",EDGE,"E13"),sQuery(id+"F4.wireOp",EDGE,"E14"),sQuery(id+"F4.wireOp",EDGE,"E15"),sQuery(id+"F4.wireOp",EDGE,"E16"),sQuery(id+"F4.wireOp",EDGE,"E17"),sQuery(id+"F4.wireOp",EDGE,"E18.trimOffspring"),sQuery(id+"F4.wireOp",EDGE,"E19.trimOffspring"),sQuery(id+"F4.wireOp",EDGE,"E20.trimOffspring"),sQuery(id+"F4.wireOp",EDGE,"E21.1.0"),sQuery(id+"F4.wireOp",EDGE,"E21.1.1"),sQuery(id+"F4.wireOp",EDGE,"E21.1.2"),sQuery(id+"F4.wireOp",EDGE,"E21.1.3"),sQuery(id+"F4.wireOp",EDGE,"E21.1.4"),sQuery(id+"F4.wireOp",EDGE,"E21.1.5"),sQuery(id+"F4.wireOp",EDGE,"E21.1.6"),sQuery(id+"F4.wireOp",EDGE,"E21.1.7"),sQuery(id+"F4.wireOp",EDGE,"E21.1.8"),sQuery(id+"F4.wireOp",EDGE,"E21.2.0"),sQuery(id+"F4.wireOp",EDGE,"E21.2.1"),sQuery(id+"F4.wireOp",EDGE,"E21.2.2"),sQuery(id+"F4.wireOp",EDGE,"E21.2.3"),sQuery(id+"F4.wireOp",EDGE,"E21.2.4"),sQuery(id+"F4.wireOp",EDGE,"E21.2.5"),sQuery(id+"F4.wireOp",EDGE,"E21.2.6"),sQuery(id+"F4.wireOp",EDGE,"E21.2.7"),sQuery(id+"F4.wireOp",EDGE,"E21.2.8"),sQuery(id+"F4.wireOp",EDGE,"E21.3.0"),sQuery(id+"F4.wireOp",EDGE,"E21.3.1"),sQuery(id+"F4.wireOp",EDGE,"E21.3.2"),sQuery(id+"F4.wireOp",EDGE,"E21.3.3"),sQuery(id+"F4.wireOp",EDGE,"E21.3.4"),sQuery(id+"F4.wireOp",EDGE,"E21.3.5"),sQuery(id+"F4.wireOp",EDGE,"E21.3.6"),sQuery(id+"F4.wireOp",EDGE,"E21.3.7"),sQuery(id+"F4.wireOp",EDGE,"E21.3.8"),sQuery(id+"F4.wireOp",EDGE,"E21.4.0"),sQuery(id+"F4.wireOp",EDGE,"E21.4.1"),sQuery(id+"F4.wireOp",EDGE,"E21.4.2"),sQuery(id+"F4.wireOp",EDGE,"E21.4.3"),sQuery(id+"F4.wireOp",EDGE,"E21.4.4"),sQuery(id+"F4.wireOp",EDGE,"E21.4.5"),sQuery(id+"F4.wireOp",EDGE,"E21.4.6"),sQuery(id+"F4.wireOp",EDGE,"E21.4.7"),sQuery(id+"F4.wireOp",EDGE,"E21.4.8"),sQuery(id+"F4.wireOp",EDGE,"E21.5.0"),sQuery(id+"F4.wireOp",EDGE,"E21.5.1"),sQuery(id+"F4.wireOp",EDGE,"E21.5.2"),sQuery(id+"F4.wireOp",EDGE,"E21.5.3"),sQuery(id+"F4.wireOp",EDGE,"E21.5.4"),sQuery(id+"F4.wireOp",EDGE,"E21.5.5"),sQuery(id+"F4.wireOp",EDGE,"E21.5.6"),sQuery(id+"F4.wireOp",EDGE,"E21.5.7"),sQuery(id+"F4.wireOp",EDGE,"E21.5.8"),sQuery(id+"F4.wireOp",EDGE,"E21.6.0"),sQuery(id+"F4.wireOp",EDGE,"E21.6.1"),sQuery(id+"F4.wireOp",EDGE,"E21.6.2"),sQuery(id+"F4.wireOp",EDGE,"E21.6.3"),sQuery(id+"F4.wireOp",EDGE,"E21.6.4"),sQuery(id+"F4.wireOp",EDGE,"E21.6.5"),sQuery(id+"F4.wireOp",EDGE,"E21.6.6"),sQuery(id+"F4.wireOp",EDGE,"E21.6.7"),sQuery(id+"F4.wireOp",EDGE,"E21.6.8"),sQuery(id+"F4.wireOp",EDGE,"E21.7.0"),sQuery(id+"F4.wireOp",EDGE,"E21.7.1"),sQuery(id+"F4.wireOp",EDGE,"E21.7.2"),sQuery(id+"F4.wireOp",EDGE,"E21.7.3"),sQuery(id+"F4.wireOp",EDGE,"E21.7.4"),sQuery(id+"F4.wireOp",EDGE,"E21.7.5"),sQuery(id+"F4.wireOp",EDGE,"E21.7.6"),sQuery(id+"F4.wireOp",EDGE,"E21.7.7"),sQuery(id+"F4.wireOp",EDGE,"E21.7.8"),sQuery(id+"F4.wireOp",EDGE,"E22.trimOffspring"),sQuery(id+"F4.wireOp",EDGE,"E23.trimOffspring"),sQuery(id+"F4.wireOp",EDGE,"E24.trimOffspring"),sQuery(id+"F4.wireOp",EDGE,"E25.trimOffspring"),sQuery(id+"F4.wireOp",EDGE,"E26.trimOffspring"),sQuery(id+"F4.wireOp",EDGE,"E27.trimOffspring"),sQuery(id+"F4.wireOp",EDGE,"E28.trimOffspring"),sQuery(id+"F4.wireOp",EDGE,"E29.trimOffspring"),sQuery(id+"F4.wireOp",EDGE,"E30.trimOffspring"),sQuery(id+"F4.wireOp",EDGE,"E31.trimOffspring"),sQuery(id+"F4.wireOp",EDGE,"E32.trimOffspring"),sQuery(id+"F4.wireOp",EDGE,"E33.trimOffspring"),sQuery(id+"F4.wireOp",EDGE,"E34.trimOffspring"),sQuery(id+"F4.wireOp",EDGE,"E35.trimOffspring"),sQuery(id+"F4.wireOp",EDGE,"E36.trimOffspring"),sQuery(id+"F4.wireOp",EDGE,"E37.trimOffspring"),sQuery(id+"F4.wireOp",EDGE,"E38.trimOffspring"),sQuery(id+"F4.wireOp",EDGE,"E39.trimOffspring"),sQuery(id+"F4.wireOp",EDGE,"E40.trimOffspring"),sQuery(id+"F4.wireOp",EDGE,"E41.trimOffspring"),sQuery(id+"F4.wireOp",EDGE,"E42.trimOffspring"),sQuery(id+"F4.wireOp",EDGE,"E43.trimOffspring"),sQuery(id+"F4.wireOp",EDGE,"E44.trimOffspring"),sQuery(id+"F4.wireOp",EDGE,"E45.trimOffspring"),sQuery(id+"F4.wireOp",EDGE,"E46.trimOffspring"),sQuery(id+"F4.wireOp",EDGE,"E47.trimOffspring"),sQuery(id+"F4.wireOp",EDGE,"E48.trimOffspring"),sQuery(id+"F4.wireOp",EDGE,"E49.trimOffspring"),sQuery(id+"F4.wireOp",EDGE,"E50.bottom"),sQuery(id+"F4.wireOp",EDGE,"E50.top"),sQuery(id+"F4.wireOp",EDGE,"E50.left"),sQuery(id+"F4.wireOp",EDGE,"E50.right"),sQuery(id+"F4.wireOp",EDGE,"E51"),sQuery(id+"F4.wireOp",EDGE,"E52"),sQuery(id+"F4.wireOp",EDGE,"E53.trimOffspring"),sQuery(id+"F4.wireOp",EDGE,"E54"),sQuery(id+"F4.wireOp",EDGE,"E55"),sQuery(id+"F4.wireOp",EDGE,"E56.trimOffspring"),sQuery(id+"F4.wireOp",EDGE,"E57.1.1"),sQuery(id+"F4.wireOp",EDGE,"E57.1.2"),sQuery(id+"F4.wireOp",EDGE,"E57.1.3"),sQuery(id+"F4.wireOp",EDGE,"E57.1.4"),sQuery(id+"F4.wireOp",EDGE,"E57.1.5"),sQuery(id+"F4.wireOp",EDGE,"E57.1.6"),sQuery(id+"F4.wireOp",EDGE,"E57.1.7"),sQuery(id+"F4.wireOp",EDGE,"E57.1.8"),sQuery(id+"F4.wireOp",EDGE,"E57.1.9"),sQuery(id+"F4.wireOp",EDGE,"E57.1.10"),sQuery(id+"F4.wireOp",EDGE,"E57.2.1"),sQuery(id+"F4.wireOp",EDGE,"E57.2.2"),sQuery(id+"F4.wireOp",EDGE,"E57.2.3"),sQuery(id+"F4.wireOp",EDGE,"E57.2.4"),sQuery(id+"F4.wireOp",EDGE,"E57.2.5"),sQuery(id+"F4.wireOp",EDGE,"E57.2.6"),sQuery(id+"F4.wireOp",EDGE,"E57.2.7"),sQuery(id+"F4.wireOp",EDGE,"E57.2.8"),sQuery(id+"F4.wireOp",EDGE,"E57.2.9"),sQuery(id+"F4.wireOp",EDGE,"E57.2.10"),sQuery(id+"F4.wireOp",EDGE,"E57.3.1"),sQuery(id+"F4.wireOp",EDGE,"E57.3.2"),sQuery(id+"F4.wireOp",EDGE,"E57.3.3"),sQuery(id+"F4.wireOp",EDGE,"E57.3.4"),sQuery(id+"F4.wireOp",EDGE,"E57.3.5"),sQuery(id+"F4.wireOp",EDGE,"E57.3.6"),sQuery(id+"F4.wireOp",EDGE,"E57.3.7"),sQuery(id+"F4.wireOp",EDGE,"E57.3.8"),sQuery(id+"F4.wireOp",EDGE,"E57.3.9"),sQuery(id+"F4.wireOp",EDGE,"E57.3.10"),sQuery(id+"F4.wireOp",EDGE,"E57.4.1"),sQuery(id+"F4.wireOp",EDGE,"E57.4.2"),sQuery(id+"F4.wireOp",EDGE,"E57.4.3"),sQuery(id+"F4.wireOp",EDGE,"E57.4.4"),sQuery(id+"F4.wireOp",EDGE,"E57.4.5"),sQuery(id+"F4.wireOp",EDGE,"E57.4.6"),sQuery(id+"F4.wireOp",EDGE,"E57.4.7"),sQuery(id+"F4.wireOp",EDGE,"E57.4.8"),sQuery(id+"F4.wireOp",EDGE,"E57.4.9"),sQuery(id+"F4.wireOp",EDGE,"E57.4.10"),sQuery(id+"F4.wireOp",EDGE,"E57.5.1"),sQuery(id+"F4.wireOp",EDGE,"E57.5.2"),sQuery(id+"F4.wireOp",EDGE,"E57.5.3"),sQuery(id+"F4.wireOp",EDGE,"E57.5.4"),sQuery(id+"F4.wireOp",EDGE,"E57.5.5"),sQuery(id+"F4.wireOp",EDGE,"E57.5.6"),sQuery(id+"F4.wireOp",EDGE,"E57.5.7"),sQuery(id+"F4.wireOp",EDGE,"E57.5.8"),sQuery(id+"F4.wireOp",EDGE,"E57.5.9"),sQuery(id+"F4.wireOp",EDGE,"E57.5.10"),sQuery(id+"F4.wireOp",EDGE,"E57.6.1"),sQuery(id+"F4.wireOp",EDGE,"E57.6.2"),sQuery(id+"F4.wireOp",EDGE,"E57.6.3"),sQuery(id+"F4.wireOp",EDGE,"E57.6.4"),sQuery(id+"F4.wireOp",EDGE,"E57.6.5"),sQuery(id+"F4.wireOp",EDGE,"E57.6.6"),sQuery(id+"F4.wireOp",EDGE,"E57.6.7"),sQuery(id+"F4.wireOp",EDGE,"E57.6.8"),sQuery(id+"F4.wireOp",EDGE,"E57.6.9"),sQuery(id+"F4.wireOp",EDGE,"E57.6.10"),sQuery(id+"F4.wireOp",EDGE,"E57.7.1"),sQuery(id+"F4.wireOp",EDGE,"E57.7.2"),sQuery(id+"F4.wireOp",EDGE,"E57.7.3"),sQuery(id+"F4.wireOp",EDGE,"E57.7.4"),sQuery(id+"F4.wireOp",EDGE,"E57.7.5"),sQuery(id+"F4.wireOp",EDGE,"E57.7.6"),sQuery(id+"F4.wireOp",EDGE,"E57.7.7"),sQuery(id+"F4.wireOp",EDGE,"E57.7.8"),sQuery(id+"F4.wireOp",EDGE,"E57.7.9"),sQuery(id+"F4.wireOp",EDGE,"E57.7.10"),sQuery(id+"F4.wireOp",EDGE,"E58.bottom"),sQuery(id+"F4.wireOp",EDGE,"E58.top"),sQuery(id+"F4.wireOp",EDGE,"E58.left"),sQuery(id+"F4.wireOp",EDGE,"E58.right"),sQuery(id+"F4.wireOp",EDGE,"E59"),sQuery(id+"F4.wireOp",EDGE,"E60"),sQuery(id+"F4.wireOp",EDGE,"E61.trimOffspring"),sQuery(id+"F4.wireOp",EDGE,"E62"),sQuery(id+"F4.wireOp",EDGE,"E63"),sQuery(id+"F4.wireOp",EDGE,"E64.trimOffspring"),sQuery(id+"F4.wireOp",EDGE,"E65.1.0"),sQuery(id+"F4.wireOp",EDGE,"E65.1.2"),sQuery(id+"F4.wireOp",EDGE,"E65.1.3"),sQuery(id+"F4.wireOp",EDGE,"E65.1.4"),sQuery(id+"F4.wireOp",EDGE,"E65.1.5"),sQuery(id+"F4.wireOp",EDGE,"E65.1.6"),sQuery(id+"F4.wireOp",EDGE,"E65.1.7"),sQuery(id+"F4.wireOp",EDGE,"E65.1.8"),sQuery(id+"F4.wireOp",EDGE,"E65.1.9"),sQuery(id+"F4.wireOp",EDGE,"E65.1.10"),sQuery(id+"F4.wireOp",EDGE,"E65.2.0"),sQuery(id+"F4.wireOp",EDGE,"E65.2.2"),sQuery(id+"F4.wireOp",EDGE,"E65.2.3"),sQuery(id+"F4.wireOp",EDGE,"E65.2.4"),sQuery(id+"F4.wireOp",EDGE,"E65.2.5"),sQuery(id+"F4.wireOp",EDGE,"E65.2.6"),sQuery(id+"F4.wireOp",EDGE,"E65.2.7"),sQuery(id+"F4.wireOp",EDGE,"E65.2.8"),sQuery(id+"F4.wireOp",EDGE,"E65.2.9"),sQuery(id+"F4.wireOp",EDGE,"E65.2.10"),sQuery(id+"F4.wireOp",EDGE,"E65.3.0"),sQuery(id+"F4.wireOp",EDGE,"E65.3.2"),sQuery(id+"F4.wireOp",EDGE,"E65.3.3"),sQuery(id+"F4.wireOp",EDGE,"E65.3.4"),sQuery(id+"F4.wireOp",EDGE,"E65.3.5"),sQuery(id+"F4.wireOp",EDGE,"E65.3.6"),sQuery(id+"F4.wireOp",EDGE,"E65.3.7"),sQuery(id+"F4.wireOp",EDGE,"E65.3.8"),sQuery(id+"F4.wireOp",EDGE,"E65.3.9"),sQuery(id+"F4.wireOp",EDGE,"E65.3.10"),sQuery(id+"F4.wireOp",EDGE,"E65.4.0"),sQuery(id+"F4.wireOp",EDGE,"E65.4.2"),sQuery(id+"F4.wireOp",EDGE,"E65.4.3"),sQuery(id+"F4.wireOp",EDGE,"E65.4.4"),sQuery(id+"F4.wireOp",EDGE,"E65.4.5"),sQuery(id+"F4.wireOp",EDGE,"E65.4.6"),sQuery(id+"F4.wireOp",EDGE,"E65.4.7"),sQuery(id+"F4.wireOp",EDGE,"E65.4.8"),sQuery(id+"F4.wireOp",EDGE,"E65.4.9"),sQuery(id+"F4.wireOp",EDGE,"E65.4.10"),sQuery(id+"F4.wireOp",EDGE,"E65.5.0"),sQuery(id+"F4.wireOp",EDGE,"E65.5.2"),sQuery(id+"F4.wireOp",EDGE,"E65.5.3"),sQuery(id+"F4.wireOp",EDGE,"E65.5.4"),sQuery(id+"F4.wireOp",EDGE,"E65.5.5"),sQuery(id+"F4.wireOp",EDGE,"E65.5.6"),sQuery(id+"F4.wireOp",EDGE,"E65.5.7"),sQuery(id+"F4.wireOp",EDGE,"E65.5.8"),sQuery(id+"F4.wireOp",EDGE,"E65.5.9"),sQuery(id+"F4.wireOp",EDGE,"E65.5.10"),sQuery(id+"F4.wireOp",EDGE,"E65.6.0"),sQuery(id+"F4.wireOp",EDGE,"E65.6.2"),sQuery(id+"F4.wireOp",EDGE,"E65.6.3"),sQuery(id+"F4.wireOp",EDGE,"E65.6.4"),sQuery(id+"F4.wireOp",EDGE,"E65.6.5"),sQuery(id+"F4.wireOp",EDGE,"E65.6.6"),sQuery(id+"F4.wireOp",EDGE,"E65.6.7"),sQuery(id+"F4.wireOp",EDGE,"E65.6.8"),sQuery(id+"F4.wireOp",EDGE,"E65.6.9"),sQuery(id+"F4.wireOp",EDGE,"E65.6.10"),sQuery(id+"F4.wireOp",EDGE,"E65.7.0"),sQuery(id+"F4.wireOp",EDGE,"E65.7.2"),sQuery(id+"F4.wireOp",EDGE,"E65.7.3"),sQuery(id+"F4.wireOp",EDGE,"E65.7.4"),sQuery(id+"F4.wireOp",EDGE,"E65.7.5"),sQuery(id+"F4.wireOp",EDGE,"E65.7.6"),sQuery(id+"F4.wireOp",EDGE,"E65.7.7"),sQuery(id+"F4.wireOp",EDGE,"E65.7.8"),sQuery(id+"F4.wireOp",EDGE,"E65.7.9"),sQuery(id+"F4.wireOp",EDGE,"E65.7.10"),sQuery(id+"F4.wireOp",EDGE,"E66.bottom"),sQuery(id+"F4.wireOp",EDGE,"E66.top"),sQuery(id+"F4.wireOp",EDGE,"E66.left"),sQuery(id+"F4.wireOp",EDGE,"E66.right"),sQuery(id+"F4.wireOp",EDGE,"E67"),sQuery(id+"F4.wireOp",EDGE,"E68"),sQuery(id+"F4.wireOp",EDGE,"E69.trimOffspring"),sQuery(id+"F4.wireOp",EDGE,"E70"),sQuery(id+"F4.wireOp",EDGE,"E71"),sQuery(id+"F4.wireOp",EDGE,"E72.trimOffspring"),sQuery(id+"F4.wireOp",EDGE,"E73.1.0"),sQuery(id+"F4.wireOp",EDGE,"E73.1.1"),sQuery(id+"F4.wireOp",EDGE,"E73.1.2"),sQuery(id+"F4.wireOp",EDGE,"E73.1.3"),sQuery(id+"F4.wireOp",EDGE,"E73.1.4"),sQuery(id+"F4.wireOp",EDGE,"E73.1.5"),sQuery(id+"F4.wireOp",EDGE,"E73.1.7"),sQuery(id+"F4.wireOp",EDGE,"E73.1.8"),sQuery(id+"F4.wireOp",EDGE,"E73.1.9"),sQuery(id+"F4.wireOp",EDGE,"E73.1.10"),sQuery(id+"F4.wireOp",EDGE,"E73.2.0"),sQuery(id+"F4.wireOp",EDGE,"E73.2.1"),sQuery(id+"F4.wireOp",EDGE,"E73.2.2"),sQuery(id+"F4.wireOp",EDGE,"E73.2.3"),sQuery(id+"F4.wireOp",EDGE,"E73.2.4"),sQuery(id+"F4.wireOp",EDGE,"E73.2.5"),sQuery(id+"F4.wireOp",EDGE,"E73.2.7"),sQuery(id+"F4.wireOp",EDGE,"E73.2.8"),sQuery(id+"F4.wireOp",EDGE,"E73.2.9"),sQuery(id+"F4.wireOp",EDGE,"E73.2.10"),sQuery(id+"F4.wireOp",EDGE,"E73.3.0"),sQuery(id+"F4.wireOp",EDGE,"E73.3.1"),sQuery(id+"F4.wireOp",EDGE,"E73.3.2"),sQuery(id+"F4.wireOp",EDGE,"E73.3.3"),sQuery(id+"F4.wireOp",EDGE,"E73.3.4"),sQuery(id+"F4.wireOp",EDGE,"E73.3.5"),sQuery(id+"F4.wireOp",EDGE,"E73.3.7"),sQuery(id+"F4.wireOp",EDGE,"E73.3.8"),sQuery(id+"F4.wireOp",EDGE,"E73.3.9"),sQuery(id+"F4.wireOp",EDGE,"E73.3.10"),sQuery(id+"F4.wireOp",EDGE,"E73.4.0"),sQuery(id+"F4.wireOp",EDGE,"E73.4.1"),sQuery(id+"F4.wireOp",EDGE,"E73.4.2"),sQuery(id+"F4.wireOp",EDGE,"E73.4.3"),sQuery(id+"F4.wireOp",EDGE,"E73.4.4"),sQuery(id+"F4.wireOp",EDGE,"E73.4.5"),sQuery(id+"F4.wireOp",EDGE,"E73.4.7"),sQuery(id+"F4.wireOp",EDGE,"E73.4.8"),sQuery(id+"F4.wireOp",EDGE,"E73.4.9"),sQuery(id+"F4.wireOp",EDGE,"E73.4.10"),sQuery(id+"F4.wireOp",EDGE,"E73.5.0"),sQuery(id+"F4.wireOp",EDGE,"E73.5.1"),sQuery(id+"F4.wireOp",EDGE,"E73.5.2"),sQuery(id+"F4.wireOp",EDGE,"E73.5.3"),sQuery(id+"F4.wireOp",EDGE,"E73.5.4"),sQuery(id+"F4.wireOp",EDGE,"E73.5.5"),sQuery(id+"F4.wireOp",EDGE,"E73.5.7"),sQuery(id+"F4.wireOp",EDGE,"E73.5.8"),sQuery(id+"F4.wireOp",EDGE,"E73.5.9"),sQuery(id+"F4.wireOp",EDGE,"E73.5.10"),sQuery(id+"F4.wireOp",EDGE,"E73.6.0"),sQuery(id+"F4.wireOp",EDGE,"E73.6.1"),sQuery(id+"F4.wireOp",EDGE,"E73.6.2"),sQuery(id+"F4.wireOp",EDGE,"E73.6.3"),sQuery(id+"F4.wireOp",EDGE,"E73.6.4"),sQuery(id+"F4.wireOp",EDGE,"E73.6.5"),sQuery(id+"F4.wireOp",EDGE,"E73.6.7"),sQuery(id+"F4.wireOp",EDGE,"E73.6.8"),sQuery(id+"F4.wireOp",EDGE,"E73.6.9"),sQuery(id+"F4.wireOp",EDGE,"E73.6.10"),sQuery(id+"F4.wireOp",EDGE,"E73.7.0"),sQuery(id+"F4.wireOp",EDGE,"E73.7.1"),sQuery(id+"F4.wireOp",EDGE,"E73.7.2"),sQuery(id+"F4.wireOp",EDGE,"E73.7.3"),sQuery(id+"F4.wireOp",EDGE,"E73.7.4"),sQuery(id+"F4.wireOp",EDGE,"E73.7.5"),sQuery(id+"F4.wireOp",EDGE,"E73.7.7"),sQuery(id+"F4.wireOp",EDGE,"E73.7.8"),sQuery(id+"F4.wireOp",EDGE,"E73.7.9"),sQuery(id+"F4.wireOp",EDGE,"E73.7.10")])],"isStart":true});
            var sketch = newSketch(context, id + "F18", { "sketchPlane" : qUnion([Q0])});
            skArc(sketch, "E226.0", {"start": v(15, 519.78) * mm, "mid": v(199, 480.42) * mm, "end": v(356.94, 378.15) * mm, "construction": true});
            skLineSegment(sketch, "E227.0", {"start": v(15, 519.78) * mm, "end": v(15, 457.7) * mm, "construction": true});
            skLineSegment(sketch, "E228.0", {"start": v(15, 362.3) * mm, "end": v(15, 309.64) * mm, "construction": true});
            skArc(sketch, "E229.0", {"start": v(15, 309.64) * mm, "mid": v(118.63, 286.4) * mm, "end": v(208.34, 229.55) * mm, "construction": true});
            skLineSegment(sketch, "E230.0", {"start": v(245.58, 266.8) * mm, "end": v(208.34, 229.55) * mm, "construction": true});
            skArc(sketch, "E231.0", {"start": v(269.1, 335.38) * mm, "mid": v(291.2, 339.9) * mm, "end": v(313.03, 334.25) * mm, "construction": true});
            skArc(sketch, "E232.0", {"start": v(46.86, 427.44) * mm, "mid": v(164.55, 397.27) * mm, "end": v(269.1, 335.38) * mm, "construction": true});
            skArc(sketch, "E233.0", {"start": v(15, 457.7) * mm, "mid": v(34.43, 446.26) * mm, "end": v(46.86, 427.44) * mm, "construction": true});
            skArc(sketch, "E234.0", {"start": v(48.3, 397.07) * mm, "mid": v(153.07, 369.55) * mm, "end": v(246.62, 314.93) * mm, "construction": true});
            skArc(sketch, "E235.0", {"start": v(48.3, 397.07) * mm, "mid": v(36.11, 375.42) * mm, "end": v(15, 362.3) * mm, "construction": true});
            skCircle(sketch, "E236.0", {"center": v(0, 410) * mm, "radius": 25 * mm, "construction": true});
            skArc(sketch, "E237.0", {"start": v(245.58, 266.8) * mm, "mid": v(239.93, 291) * mm, "end": v(246.62, 314.93) * mm, "construction": true});
            skLineSegment(sketch, "E238.0", {"start": v(378.15, 356.94) * mm, "end": v(334.25, 313.03) * mm, "construction": true});
            skPoint(sketch, "E239.0", {"position": v(339.9, 291.2) * mm});
            skArc(sketch, "E240.0", {"start": v(314.93, 246.62) * mm, "mid": v(291, 239.93) * mm, "end": v(266.8, 245.58) * mm, "construction": true});
            skLineSegment(sketch, "E241.0", {"start": v(266.8, 245.58) * mm, "end": v(229.55, 208.34) * mm, "construction": true});
            skArc(sketch, "E242.0", {"start": v(229.55, 208.34) * mm, "mid": v(286.4, 118.63) * mm, "end": v(309.64, 15) * mm, "construction": true});
            skArc(sketch, "E243.0", {"start": v(334.25, 313.03) * mm, "mid": v(339.9, 291.2) * mm, "end": v(335.38, 269.1) * mm, "construction": true});
            skCircle(sketch, "E244.0", {"center": v(289.91, 289.91) * mm, "radius": 25 * mm, "construction": true});
            skLineSegment(sketch, "E245.0", {"start": v(313.03, 334.25) * mm, "end": v(356.94, 378.15) * mm, "construction": true});
            skLineSegment(sketch, "E246", {"start": v(382.54, 382.54) * mm, "end": v(0, 0) * mm, "construction": true});
            skLineSegment(sketch, "E247", {"start": v(0, 0) * mm, "end": v(0, 541) * mm, "construction": true});
            skArc(sketch, "E248.0", {"start": v(7, 527.95) * mm, "mid": v(202.06, 487.8) * mm, "end": v(368.37, 378.27) * mm});
            skArc(sketch, "E249.0", {"start": v(7, 301.92) * mm, "mid": v(115.57, 279.01) * mm, "end": v(208.54, 218.44) * mm});
            skLineSegment(sketch, "E250.0", {"start": v(7, 368.59) * mm, "end": v(7, 301.92) * mm});
            skArc(sketch, "E251.0", {"start": v(7, 451.41) * mm, "mid": v(42, 410) * mm, "end": v(7, 368.59) * mm});
            skLineSegment(sketch, "E252.0", {"start": v(255.68, 265.58) * mm, "end": v(208.54, 218.44) * mm});
            skArc(sketch, "E253.0", {"start": v(314.25, 324.15) * mm, "mid": v(319.61, 260.22) * mm, "end": v(255.68, 265.58) * mm});
            skLineSegment(sketch, "E254.0", {"start": v(314.25, 324.15) * mm, "end": v(368.37, 378.27) * mm});
            skLineSegment(sketch, "E255.0", {"start": v(7, 527.95) * mm, "end": v(7, 451.41) * mm});
            skSolve(sketch);
        }
        {
            var Q0;
            Q0 = qSketchRegion(id + "F18", true);
            extrude(context, id + "F19", {"entities" : qUnion([Q0]), "depth" : 1 * mm, "offsetDistance" : 25 * mm});
        }
        {
            var Q0;
            Q0=makeQuery(id+"F19.opExtrude","SWEPT_BODY",BODY,{"disambiguationData":[OSD([sQuery(id+"F18.wireOp",EDGE,"E248.0"),sQuery(id+"F18.wireOp",EDGE,"E249.0"),sQuery(id+"F18.wireOp",EDGE,"E250.0"),sQuery(id+"F18.wireOp",EDGE,"E251.0"),sQuery(id+"F18.wireOp",EDGE,"E252.0"),sQuery(id+"F18.wireOp",EDGE,"E253.0"),sQuery(id+"F18.wireOp",EDGE,"E254.0"),sQuery(id+"F18.wireOp",EDGE,"E255.0")])]});
            var Q1;
            Q1=makeQuery(id+"F5.opExtrude","CAP_EDGE",EDGE,{"disambiguationData":[OSD([sQuery(id+"F4.wireOp",EDGE,"E5")])],"isStart":true});
            circularPattern(context, id + "F20", {"entities" : qUnion([Q0]), "axis" : qUnion([Q1]), "angle" : 360 * degree, "instanceCount" : 8, "equalSpace" : true});
        }
        {
            var Q0;
            Q0=makeQuery(id+"F6.imprint","IMPRINT",FACE,{"disambiguationData":[TD([[makeQuery(id+"F6.imprint","IMPRINT",EDGE,{"derivedFrom":sQuery(id+"F6.wireOp",EDGE,"E74.0")}),-1.0]])]});
            extrude(context, id + "F21", {"entities" : qUnion([Q0]), "depth" : 10 * mm, "offsetDistance" : 25 * mm});
        }
        {
            var Q0;
            Q0=makeQuery(id+"F21.opExtrude","CAP_FACE",FACE,{"disambiguationData":[OSD([sQuery(id+"F6.wireOp",EDGE,"E74.0"),sQuery(id+"F6.wireOp",EDGE,"E75.0"),sQuery(id+"F6.wireOp",EDGE,"E77.0"),sQuery(id+"F6.wireOp",EDGE,"E78.0"),sQuery(id+"F6.wireOp",EDGE,"E81"),sQuery(id+"F6.wireOp",EDGE,"E82"),sQuery(id+"F6.wireOp",EDGE,"E83"),sQuery(id+"F6.wireOp",EDGE,"E84"),sQuery(id+"F6.wireOp",EDGE,"E85"),sQuery(id+"F6.wireOp",EDGE,"E86"),sQuery(id+"F6.wireOp",EDGE,"E87.trimOffspring"),sQuery(id+"F6.wireOp",EDGE,"E88.trimOffspring"),sQuery(id+"F6.wireOp",EDGE,"E89.trimOffspring"),sQuery(id+"F6.wireOp",EDGE,"E90.1.0"),sQuery(id+"F6.wireOp",EDGE,"E90.1.1"),sQuery(id+"F6.wireOp",EDGE,"E90.1.2"),sQuery(id+"F6.wireOp",EDGE,"E90.1.3"),sQuery(id+"F6.wireOp",EDGE,"E90.1.4"),sQuery(id+"F6.wireOp",EDGE,"E90.1.5"),sQuery(id+"F6.wireOp",EDGE,"E90.1.6"),sQuery(id+"F6.wireOp",EDGE,"E90.1.7"),sQuery(id+"F6.wireOp",EDGE,"E90.1.8"),sQuery(id+"F6.wireOp",EDGE,"E90.2.0"),sQuery(id+"F6.wireOp",EDGE,"E90.2.1"),sQuery(id+"F6.wireOp",EDGE,"E90.2.2"),sQuery(id+"F6.wireOp",EDGE,"E90.2.3"),sQuery(id+"F6.wireOp",EDGE,"E90.2.4"),sQuery(id+"F6.wireOp",EDGE,"E90.2.5"),sQuery(id+"F6.wireOp",EDGE,"E90.2.6"),sQuery(id+"F6.wireOp",EDGE,"E90.2.7"),sQuery(id+"F6.wireOp",EDGE,"E90.2.8"),sQuery(id+"F6.wireOp",EDGE,"E90.3.0"),sQuery(id+"F6.wireOp",EDGE,"E90.3.1"),sQuery(id+"F6.wireOp",EDGE,"E90.3.2"),sQuery(id+"F6.wireOp",EDGE,"E90.3.3"),sQuery(id+"F6.wireOp",EDGE,"E90.3.4"),sQuery(id+"F6.wireOp",EDGE,"E90.3.5"),sQuery(id+"F6.wireOp",EDGE,"E90.3.6"),sQuery(id+"F6.wireOp",EDGE,"E90.3.7"),sQuery(id+"F6.wireOp",EDGE,"E90.3.8"),sQuery(id+"F6.wireOp",EDGE,"E90.4.0"),sQuery(id+"F6.wireOp",EDGE,"E90.4.1"),sQuery(id+"F6.wireOp",EDGE,"E90.4.2"),sQuery(id+"F6.wireOp",EDGE,"E90.4.3"),sQuery(id+"F6.wireOp",EDGE,"E90.4.4"),sQuery(id+"F6.wireOp",EDGE,"E90.4.5"),sQuery(id+"F6.wireOp",EDGE,"E90.4.6"),sQuery(id+"F6.wireOp",EDGE,"E90.4.7"),sQuery(id+"F6.wireOp",EDGE,"E90.4.8"),sQuery(id+"F6.wireOp",EDGE,"E90.5.0"),sQuery(id+"F6.wireOp",EDGE,"E90.5.1"),sQuery(id+"F6.wireOp",EDGE,"E90.5.2"),sQuery(id+"F6.wireOp",EDGE,"E90.5.3"),sQuery(id+"F6.wireOp",EDGE,"E90.5.4"),sQuery(id+"F6.wireOp",EDGE,"E90.5.5"),sQuery(id+"F6.wireOp",EDGE,"E90.5.6"),sQuery(id+"F6.wireOp",EDGE,"E90.5.7"),sQuery(id+"F6.wireOp",EDGE,"E90.5.8"),sQuery(id+"F6.wireOp",EDGE,"E90.6.0"),sQuery(id+"F6.wireOp",EDGE,"E90.6.1"),sQuery(id+"F6.wireOp",EDGE,"E90.6.2"),sQuery(id+"F6.wireOp",EDGE,"E90.6.3"),sQuery(id+"F6.wireOp",EDGE,"E90.6.4"),sQuery(id+"F6.wireOp",EDGE,"E90.6.5"),sQuery(id+"F6.wireOp",EDGE,"E90.6.6"),sQuery(id+"F6.wireOp",EDGE,"E90.6.7"),sQuery(id+"F6.wireOp",EDGE,"E90.6.8"),sQuery(id+"F6.wireOp",EDGE,"E90.7.0"),sQuery(id+"F6.wireOp",EDGE,"E90.7.1"),sQuery(id+"F6.wireOp",EDGE,"E90.7.2"),sQuery(id+"F6.wireOp",EDGE,"E90.7.3"),sQuery(id+"F6.wireOp",EDGE,"E90.7.4"),sQuery(id+"F6.wireOp",EDGE,"E90.7.5"),sQuery(id+"F6.wireOp",EDGE,"E90.7.6"),sQuery(id+"F6.wireOp",EDGE,"E90.7.7"),sQuery(id+"F6.wireOp",EDGE,"E90.7.8"),sQuery(id+"F6.wireOp",EDGE,"E91.trimOffspring"),sQuery(id+"F6.wireOp",EDGE,"E92.trimOffspring"),sQuery(id+"F6.wireOp",EDGE,"E94.trimOffspring"),sQuery(id+"F6.wireOp",EDGE,"E95.trimOffspring"),sQuery(id+"F6.wireOp",EDGE,"E96.trimOffspring"),sQuery(id+"F6.wireOp",EDGE,"E97.trimOffspring"),sQuery(id+"F6.wireOp",EDGE,"E99.trimOffspring"),sQuery(id+"F6.wireOp",EDGE,"E100.trimOffspring"),sQuery(id+"F6.wireOp",EDGE,"E102.trimOffspring"),sQuery(id+"F6.wireOp",EDGE,"E103.trimOffspring"),sQuery(id+"F6.wireOp",EDGE,"E104.trimOffspring"),sQuery(id+"F6.wireOp",EDGE,"E105.trimOffspring"),sQuery(id+"F6.wireOp",EDGE,"E106.trimOffspring"),sQuery(id+"F6.wireOp",EDGE,"E107.trimOffspring"),sQuery(id+"F6.wireOp",EDGE,"E108.trimOffspring"),sQuery(id+"F6.wireOp",EDGE,"E109.trimOffspring"),sQuery(id+"F6.wireOp",EDGE,"E110.trimOffspring"),sQuery(id+"F6.wireOp",EDGE,"E112.trimOffspring"),sQuery(id+"F6.wireOp",EDGE,"E113.trimOffspring"),sQuery(id+"F6.wireOp",EDGE,"E114.trimOffspring"),sQuery(id+"F6.wireOp",EDGE,"E116.trimOffspring"),sQuery(id+"F6.wireOp",EDGE,"E130"),sQuery(id+"F6.wireOp",EDGE,"E133.MirrorC"),sQuery(id+"F6.wireOp",EDGE,"E134.1.1"),sQuery(id+"F6.wireOp",EDGE,"E134.1.2"),sQuery(id+"F6.wireOp",EDGE,"E134.2.1"),sQuery(id+"F6.wireOp",EDGE,"E134.2.2"),sQuery(id+"F6.wireOp",EDGE,"E134.3.1"),sQuery(id+"F6.wireOp",EDGE,"E134.3.2"),sQuery(id+"F6.wireOp",EDGE,"E134.4.1"),sQuery(id+"F6.wireOp",EDGE,"E134.4.2"),sQuery(id+"F6.wireOp",EDGE,"E134.5.1"),sQuery(id+"F6.wireOp",EDGE,"E134.5.2"),sQuery(id+"F6.wireOp",EDGE,"E134.6.1"),sQuery(id+"F6.wireOp",EDGE,"E134.6.2"),sQuery(id+"F6.wireOp",EDGE,"E134.7.1"),sQuery(id+"F6.wireOp",EDGE,"E134.7.2")])],"isStart":true});
            var sketch = newSketch(context, id + "F22", { "sketchPlane" : qUnion([Q0])});
            skArc(sketch, "E256.0", {"start": v(-187.1, 208.31) * mm, "mid": v(-107.15, 258.69) * mm, "end": v(-15, 279.6) * mm, "construction": true});
            skArc(sketch, "E257.0", {"start": v(15, 279.6) * mm, "mid": v(107.15, 258.69) * mm, "end": v(187.1, 208.31) * mm, "construction": true});
            skArc(sketch, "E258.0", {"start": v(208.31, 187.1) * mm, "mid": v(258.69, 107.15) * mm, "end": v(279.6, 15) * mm, "construction": true});
            skLineSegment(sketch, "E259.0", {"start": v(253.65, 15) * mm, "end": v(279.6, 15) * mm, "construction": true});
            skLineSegment(sketch, "E260.0", {"start": v(227.7, 15) * mm, "end": v(253.65, 15) * mm, "construction": true});
            skLineSegment(sketch, "E261.0", {"start": v(227.7, -15) * mm, "end": v(253.65, -15) * mm, "construction": true});
            skLineSegment(sketch, "E262.0", {"start": v(253.65, -15) * mm, "end": v(279.6, -15) * mm, "construction": true});
            skLineSegment(sketch, "E263.0.0", {"start": v(-189.96, 168.75) * mm, "end": v(-171.61, 150.4) * mm, "construction": true});
            skArc(sketch, "E263.0.1", {"start": v(-171.61, 150.4) * mm, "mid": v(-176.93, 121.34) * mm, "end": v(-164.91, 94.36) * mm, "construction": true});
            skArc(sketch, "E263.0.2", {"start": v(-164.91, 94.36) * mm, "mid": v(-175.54, 72.7) * mm, "end": v(-183.33, 49.89) * mm, "construction": true});
            skArc(sketch, "E263.0.3", {"start": v(-183.33, 49.89) * mm, "mid": v(-210.9, 39.3) * mm, "end": v(-227.7, 15) * mm, "construction": true});
            skLineSegment(sketch, "E263.0.4", {"start": v(-227.7, 15) * mm, "end": v(-253.65, 15) * mm, "construction": true});
            skLineSegment(sketch, "E263.0.5", {"start": v(-253.65, 15) * mm, "end": v(-253.65, -15) * mm, "construction": true});
            skLineSegment(sketch, "E263.0.6", {"start": v(-253.65, -15) * mm, "end": v(-227.7, -15) * mm, "construction": true});
            skArc(sketch, "E263.0.7", {"start": v(-227.7, -15) * mm, "mid": v(-210.9, -39.3) * mm, "end": v(-183.33, -49.89) * mm, "construction": true});
            skArc(sketch, "E263.0.8", {"start": v(-183.33, -49.89) * mm, "mid": v(-175.54, -72.7) * mm, "end": v(-164.91, -94.36) * mm, "construction": true});
            skArc(sketch, "E263.0.9", {"start": v(-164.91, -94.36) * mm, "mid": v(-176.93, -121.34) * mm, "end": v(-171.61, -150.4) * mm, "construction": true});
            skLineSegment(sketch, "E263.0.10", {"start": v(-171.61, -150.4) * mm, "end": v(-189.96, -168.75) * mm, "construction": true});
            skLineSegment(sketch, "E263.0.11", {"start": v(-189.96, -168.75) * mm, "end": v(-168.75, -189.96) * mm, "construction": true});
            skLineSegment(sketch, "E263.0.12", {"start": v(-168.75, -189.96) * mm, "end": v(-150.4, -171.61) * mm, "construction": true});
            skArc(sketch, "E263.0.13", {"start": v(-150.4, -171.61) * mm, "mid": v(-121.34, -176.93) * mm, "end": v(-94.36, -164.91) * mm, "construction": true});
            skArc(sketch, "E263.0.14", {"start": v(-94.36, -164.91) * mm, "mid": v(-72.7, -175.54) * mm, "end": v(-49.89, -183.33) * mm, "construction": true});
            skArc(sketch, "E263.0.15", {"start": v(-49.89, -183.33) * mm, "mid": v(-39.3, -210.9) * mm, "end": v(-15, -227.7) * mm, "construction": true});
            skLineSegment(sketch, "E263.0.16", {"start": v(-15, -227.7) * mm, "end": v(-15, -253.65) * mm, "construction": true});
            skLineSegment(sketch, "E263.0.17", {"start": v(-15, -253.65) * mm, "end": v(15, -253.65) * mm, "construction": true});
            skLineSegment(sketch, "E263.0.18", {"start": v(15, -253.65) * mm, "end": v(15, -227.7) * mm, "construction": true});
            skArc(sketch, "E263.0.19", {"start": v(15, -227.7) * mm, "mid": v(39.3, -210.9) * mm, "end": v(49.89, -183.33) * mm, "construction": true});
            skArc(sketch, "E263.0.20", {"start": v(49.89, -183.33) * mm, "mid": v(72.7, -175.54) * mm, "end": v(94.36, -164.91) * mm, "construction": true});
            skArc(sketch, "E263.0.21", {"start": v(94.36, -164.91) * mm, "mid": v(121.34, -176.93) * mm, "end": v(150.4, -171.61) * mm, "construction": true});
            skLineSegment(sketch, "E263.0.22", {"start": v(150.4, -171.61) * mm, "end": v(168.75, -189.96) * mm, "construction": true});
            skLineSegment(sketch, "E263.0.23", {"start": v(168.75, -189.96) * mm, "end": v(189.96, -168.75) * mm, "construction": true});
            skLineSegment(sketch, "E263.0.24", {"start": v(189.96, -168.75) * mm, "end": v(171.61, -150.4) * mm, "construction": true});
            skArc(sketch, "E263.0.25", {"start": v(171.61, -150.4) * mm, "mid": v(176.93, -121.34) * mm, "end": v(164.91, -94.36) * mm, "construction": true});
            skArc(sketch, "E263.0.26", {"start": v(164.91, -94.36) * mm, "mid": v(175.54, -72.7) * mm, "end": v(183.33, -49.89) * mm, "construction": true});
            skArc(sketch, "E263.0.27", {"start": v(183.33, -49.89) * mm, "mid": v(210.9, -39.3) * mm, "end": v(227.7, -15) * mm, "construction": true});
            skLineSegment(sketch, "E263.0.29", {"start": v(253.65, -15) * mm, "end": v(253.65, 15) * mm, "construction": true});
            skLineSegment(sketch, "E263.0.30", {"start": v(253.65, 15) * mm, "end": v(227.7, 15) * mm, "construction": true});
            skArc(sketch, "E263.0.31", {"start": v(227.7, 15) * mm, "mid": v(210.9, 39.3) * mm, "end": v(183.33, 49.89) * mm, "construction": true});
            skArc(sketch, "E263.0.32", {"start": v(183.33, 49.89) * mm, "mid": v(175.54, 72.7) * mm, "end": v(164.91, 94.36) * mm, "construction": true});
            skArc(sketch, "E263.0.33", {"start": v(164.91, 94.36) * mm, "mid": v(176.93, 121.34) * mm, "end": v(171.61, 150.4) * mm, "construction": true});
            skLineSegment(sketch, "E263.0.34", {"start": v(171.61, 150.4) * mm, "end": v(189.96, 168.75) * mm, "construction": true});
            skLineSegment(sketch, "E263.0.35", {"start": v(189.96, 168.75) * mm, "end": v(168.75, 189.96) * mm, "construction": true});
            skLineSegment(sketch, "E263.0.36", {"start": v(168.75, 189.96) * mm, "end": v(150.4, 171.61) * mm, "construction": true});
            skArc(sketch, "E263.0.37", {"start": v(150.4, 171.61) * mm, "mid": v(121.34, 176.93) * mm, "end": v(94.36, 164.91) * mm, "construction": true});
            skArc(sketch, "E263.0.38", {"start": v(94.36, 164.91) * mm, "mid": v(72.7, 175.54) * mm, "end": v(49.89, 183.33) * mm, "construction": true});
            skArc(sketch, "E263.0.39", {"start": v(49.89, 183.33) * mm, "mid": v(39.3, 210.9) * mm, "end": v(15, 227.7) * mm, "construction": true});
            skLineSegment(sketch, "E263.0.40", {"start": v(15, 227.7) * mm, "end": v(15, 253.65) * mm, "construction": true});
            skLineSegment(sketch, "E263.0.41", {"start": v(15, 253.65) * mm, "end": v(-15, 253.65) * mm, "construction": true});
            skLineSegment(sketch, "E263.0.42", {"start": v(-15, 253.65) * mm, "end": v(-15, 227.7) * mm, "construction": true});
            skArc(sketch, "E263.0.43", {"start": v(-15, 227.7) * mm, "mid": v(-39.3, 210.9) * mm, "end": v(-49.89, 183.33) * mm, "construction": true});
            skArc(sketch, "E263.0.44", {"start": v(-49.89, 183.33) * mm, "mid": v(-72.7, 175.54) * mm, "end": v(-94.36, 164.91) * mm, "construction": true});
            skArc(sketch, "E263.0.45", {"start": v(-94.36, 164.91) * mm, "mid": v(-121.34, 176.93) * mm, "end": v(-150.4, 171.61) * mm, "construction": true});
            skLineSegment(sketch, "E263.0.46", {"start": v(-150.4, 171.61) * mm, "end": v(-168.75, 189.96) * mm, "construction": true});
            skLineSegment(sketch, "E263.0.47", {"start": v(-168.75, 189.96) * mm, "end": v(-189.96, 168.75) * mm, "construction": true});
            skArc(sketch, "E264.0", {"start": v(227.7, -15) * mm, "mid": v(210.9, -39.3) * mm, "end": v(183.33, -49.89) * mm, "construction": true});
            skLineSegment(sketch, "E265.0", {"start": v(68.37, -15) * mm, "end": v(132.3, -15) * mm, "construction": true});
            skArc(sketch, "E266.0", {"start": v(154.17, -42.8) * mm, "mid": v(140.7, -30.9) * mm, "end": v(132.3, -15) * mm, "construction": true});
            skCircle(sketch, "E267.0", {"center": v(0, 0) * mm, "radius": 40 * mm, "construction": true});
            skLineSegment(sketch, "E268.0", {"start": v(15, 68.37) * mm, "end": v(15, 132.3) * mm, "construction": true});
            skArc(sketch, "E269.0", {"start": v(15, 68.37) * mm, "mid": v(26.79, 64.67) * mm, "end": v(37.74, 58.95) * mm, "construction": true});
            skArc(sketch, "E270.0", {"start": v(58.95, 37.74) * mm, "mid": v(64.67, 26.79) * mm, "end": v(68.37, 15) * mm, "construction": true});
            skLineSegment(sketch, "E271.0", {"start": v(15, 253.65) * mm, "end": v(15, 279.6) * mm, "construction": true});
            skCircle(sketch, "E272.0.0", {"center": v(0, 0) * mm, "radius": 310 * mm, "construction": true});
            skArc(sketch, "E273.0", {"start": v(7, 287.91) * mm, "mid": v(203.65, 203.65) * mm, "end": v(287.91, 7) * mm});
            skLineSegment(sketch, "E274.0", {"start": v(221.41, 7) * mm, "end": v(287.91, 7) * mm});
            skArc(sketch, "E275.0", {"start": v(138.59, -7) * mm, "mid": v(187, -41.41) * mm, "end": v(221.41, 7) * mm});
            skLineSegment(sketch, "E276.0", {"start": v(61.6, -7) * mm, "end": v(138.59, -7) * mm});
            skArc(sketch, "E277.0", {"start": v(7, 61.6) * mm, "mid": v(48.51, 38.61) * mm, "end": v(61.6, -7) * mm});
            skArc(sketch, "E278.0", {"start": v(7, 138.59) * mm, "mid": v(42, 180) * mm, "end": v(7, 221.41) * mm});
            skLineSegment(sketch, "E279.0", {"start": v(7, 61.6) * mm, "end": v(7, 138.59) * mm});
            skLineSegment(sketch, "E280.0", {"start": v(7, 221.41) * mm, "end": v(7, 287.91) * mm});
            skSolve(sketch);
        }
        {
            var Q0;
            Q0 = qSketchRegion(id + "F22", true);
            extrude(context, id + "F23", {"entities" : qUnion([Q0]), "depth" : 1 * mm, "offsetDistance" : 25 * mm});
        }
        {
            var Q0;
            Q0=makeQuery(id+"F23.opExtrude","SWEPT_BODY",BODY,{"disambiguationData":[OSD([sQuery(id+"F22.wireOp",EDGE,"E273.0"),sQuery(id+"F22.wireOp",EDGE,"E274.0"),sQuery(id+"F22.wireOp",EDGE,"E275.0"),sQuery(id+"F22.wireOp",EDGE,"E276.0"),sQuery(id+"F22.wireOp",EDGE,"E277.0"),sQuery(id+"F22.wireOp",EDGE,"E278.0"),sQuery(id+"F22.wireOp",EDGE,"E279.0"),sQuery(id+"F22.wireOp",EDGE,"E280.0")])]});
            var Q1;
            Q1=makeQuery(id+"F21.opExtrude","CAP_EDGE",EDGE,{"disambiguationData":[OSD([sQuery(id+"F6.wireOp",EDGE,"E78.0")])],"isStart":true});
            circularPattern(context, id + "F24", {"entities" : qUnion([Q0]), "axis" : qUnion([Q1]), "angle" : 360 * degree, "instanceCount" : 4, "equalSpace" : true});
        }
        {
            var Q0;
            Q0=makeQuery(id+"F21.opExtrude","CAP_FACE",FACE,{"disambiguationData":[OSD([sQuery(id+"F6.wireOp",EDGE,"E74.0"),sQuery(id+"F6.wireOp",EDGE,"E75.0"),sQuery(id+"F6.wireOp",EDGE,"E77.0"),sQuery(id+"F6.wireOp",EDGE,"E78.0"),sQuery(id+"F6.wireOp",EDGE,"E81"),sQuery(id+"F6.wireOp",EDGE,"E82"),sQuery(id+"F6.wireOp",EDGE,"E83"),sQuery(id+"F6.wireOp",EDGE,"E84"),sQuery(id+"F6.wireOp",EDGE,"E85"),sQuery(id+"F6.wireOp",EDGE,"E86"),sQuery(id+"F6.wireOp",EDGE,"E87.trimOffspring"),sQuery(id+"F6.wireOp",EDGE,"E88.trimOffspring"),sQuery(id+"F6.wireOp",EDGE,"E89.trimOffspring"),sQuery(id+"F6.wireOp",EDGE,"E90.1.0"),sQuery(id+"F6.wireOp",EDGE,"E90.1.1"),sQuery(id+"F6.wireOp",EDGE,"E90.1.2"),sQuery(id+"F6.wireOp",EDGE,"E90.1.3"),sQuery(id+"F6.wireOp",EDGE,"E90.1.4"),sQuery(id+"F6.wireOp",EDGE,"E90.1.5"),sQuery(id+"F6.wireOp",EDGE,"E90.1.6"),sQuery(id+"F6.wireOp",EDGE,"E90.1.7"),sQuery(id+"F6.wireOp",EDGE,"E90.1.8"),sQuery(id+"F6.wireOp",EDGE,"E90.2.0"),sQuery(id+"F6.wireOp",EDGE,"E90.2.1"),sQuery(id+"F6.wireOp",EDGE,"E90.2.2"),sQuery(id+"F6.wireOp",EDGE,"E90.2.3"),sQuery(id+"F6.wireOp",EDGE,"E90.2.4"),sQuery(id+"F6.wireOp",EDGE,"E90.2.5"),sQuery(id+"F6.wireOp",EDGE,"E90.2.6"),sQuery(id+"F6.wireOp",EDGE,"E90.2.7"),sQuery(id+"F6.wireOp",EDGE,"E90.2.8"),sQuery(id+"F6.wireOp",EDGE,"E90.3.0"),sQuery(id+"F6.wireOp",EDGE,"E90.3.1"),sQuery(id+"F6.wireOp",EDGE,"E90.3.2"),sQuery(id+"F6.wireOp",EDGE,"E90.3.3"),sQuery(id+"F6.wireOp",EDGE,"E90.3.4"),sQuery(id+"F6.wireOp",EDGE,"E90.3.5"),sQuery(id+"F6.wireOp",EDGE,"E90.3.6"),sQuery(id+"F6.wireOp",EDGE,"E90.3.7"),sQuery(id+"F6.wireOp",EDGE,"E90.3.8"),sQuery(id+"F6.wireOp",EDGE,"E90.4.0"),sQuery(id+"F6.wireOp",EDGE,"E90.4.1"),sQuery(id+"F6.wireOp",EDGE,"E90.4.2"),sQuery(id+"F6.wireOp",EDGE,"E90.4.3"),sQuery(id+"F6.wireOp",EDGE,"E90.4.4"),sQuery(id+"F6.wireOp",EDGE,"E90.4.5"),sQuery(id+"F6.wireOp",EDGE,"E90.4.6"),sQuery(id+"F6.wireOp",EDGE,"E90.4.7"),sQuery(id+"F6.wireOp",EDGE,"E90.4.8"),sQuery(id+"F6.wireOp",EDGE,"E90.5.0"),sQuery(id+"F6.wireOp",EDGE,"E90.5.1"),sQuery(id+"F6.wireOp",EDGE,"E90.5.2"),sQuery(id+"F6.wireOp",EDGE,"E90.5.3"),sQuery(id+"F6.wireOp",EDGE,"E90.5.4"),sQuery(id+"F6.wireOp",EDGE,"E90.5.5"),sQuery(id+"F6.wireOp",EDGE,"E90.5.6"),sQuery(id+"F6.wireOp",EDGE,"E90.5.7"),sQuery(id+"F6.wireOp",EDGE,"E90.5.8"),sQuery(id+"F6.wireOp",EDGE,"E90.6.0"),sQuery(id+"F6.wireOp",EDGE,"E90.6.1"),sQuery(id+"F6.wireOp",EDGE,"E90.6.2"),sQuery(id+"F6.wireOp",EDGE,"E90.6.3"),sQuery(id+"F6.wireOp",EDGE,"E90.6.4"),sQuery(id+"F6.wireOp",EDGE,"E90.6.5"),sQuery(id+"F6.wireOp",EDGE,"E90.6.6"),sQuery(id+"F6.wireOp",EDGE,"E90.6.7"),sQuery(id+"F6.wireOp",EDGE,"E90.6.8"),sQuery(id+"F6.wireOp",EDGE,"E90.7.0"),sQuery(id+"F6.wireOp",EDGE,"E90.7.1"),sQuery(id+"F6.wireOp",EDGE,"E90.7.2"),sQuery(id+"F6.wireOp",EDGE,"E90.7.3"),sQuery(id+"F6.wireOp",EDGE,"E90.7.4"),sQuery(id+"F6.wireOp",EDGE,"E90.7.5"),sQuery(id+"F6.wireOp",EDGE,"E90.7.6"),sQuery(id+"F6.wireOp",EDGE,"E90.7.7"),sQuery(id+"F6.wireOp",EDGE,"E90.7.8"),sQuery(id+"F6.wireOp",EDGE,"E91.trimOffspring"),sQuery(id+"F6.wireOp",EDGE,"E92.trimOffspring"),sQuery(id+"F6.wireOp",EDGE,"E94.trimOffspring"),sQuery(id+"F6.wireOp",EDGE,"E95.trimOffspring"),sQuery(id+"F6.wireOp",EDGE,"E96.trimOffspring"),sQuery(id+"F6.wireOp",EDGE,"E97.trimOffspring"),sQuery(id+"F6.wireOp",EDGE,"E99.trimOffspring"),sQuery(id+"F6.wireOp",EDGE,"E100.trimOffspring"),sQuery(id+"F6.wireOp",EDGE,"E102.trimOffspring"),sQuery(id+"F6.wireOp",EDGE,"E103.trimOffspring"),sQuery(id+"F6.wireOp",EDGE,"E104.trimOffspring"),sQuery(id+"F6.wireOp",EDGE,"E105.trimOffspring"),sQuery(id+"F6.wireOp",EDGE,"E106.trimOffspring"),sQuery(id+"F6.wireOp",EDGE,"E107.trimOffspring"),sQuery(id+"F6.wireOp",EDGE,"E108.trimOffspring"),sQuery(id+"F6.wireOp",EDGE,"E109.trimOffspring"),sQuery(id+"F6.wireOp",EDGE,"E110.trimOffspring"),sQuery(id+"F6.wireOp",EDGE,"E112.trimOffspring"),sQuery(id+"F6.wireOp",EDGE,"E113.trimOffspring"),sQuery(id+"F6.wireOp",EDGE,"E114.trimOffspring"),sQuery(id+"F6.wireOp",EDGE,"E116.trimOffspring"),sQuery(id+"F6.wireOp",EDGE,"E130"),sQuery(id+"F6.wireOp",EDGE,"E133.MirrorC"),sQuery(id+"F6.wireOp",EDGE,"E134.1.1"),sQuery(id+"F6.wireOp",EDGE,"E134.1.2"),sQuery(id+"F6.wireOp",EDGE,"E134.2.1"),sQuery(id+"F6.wireOp",EDGE,"E134.2.2"),sQuery(id+"F6.wireOp",EDGE,"E134.3.1"),sQuery(id+"F6.wireOp",EDGE,"E134.3.2"),sQuery(id+"F6.wireOp",EDGE,"E134.4.1"),sQuery(id+"F6.wireOp",EDGE,"E134.4.2"),sQuery(id+"F6.wireOp",EDGE,"E134.5.1"),sQuery(id+"F6.wireOp",EDGE,"E134.5.2"),sQuery(id+"F6.wireOp",EDGE,"E134.6.1"),sQuery(id+"F6.wireOp",EDGE,"E134.6.2"),sQuery(id+"F6.wireOp",EDGE,"E134.7.1"),sQuery(id+"F6.wireOp",EDGE,"E134.7.2")])],"isStart":true});
            var sketch = newSketch(context, id + "F25", { "sketchPlane" : qUnion([Q0])});
            skCircle(sketch, "E281", {"center": v(0, 0) * mm, "radius": 60 * mm});
            skSolve(sketch);
        }
        {
            var Q0;
            Q0 = qSketchRegion(id + "F25", true);
            extrude(context, id + "F26", {"entities" : qUnion([Q0]), "depth" : 1 * mm, "offsetDistance" : 25 * mm});
        }
        {
            var Q0;
            Q0=makeQuery(id+"F5.opExtrude","CAP_FACE",FACE,{"disambiguationData":[OSD([sQuery(id+"F4.wireOp",EDGE,"E0"),sQuery(id+"F4.wireOp",EDGE,"E1"),sQuery(id+"F4.wireOp",EDGE,"E2"),sQuery(id+"F4.wireOp",EDGE,"E3"),sQuery(id+"F4.wireOp",EDGE,"E4"),sQuery(id+"F4.wireOp",EDGE,"E5"),sQuery(id+"F4.wireOp",EDGE,"E12"),sQuery(id+"F4.wireOp",EDGE,"E13"),sQuery(id+"F4.wireOp",EDGE,"E14"),sQuery(id+"F4.wireOp",EDGE,"E15"),sQuery(id+"F4.wireOp",EDGE,"E16"),sQuery(id+"F4.wireOp",EDGE,"E17"),sQuery(id+"F4.wireOp",EDGE,"E18.trimOffspring"),sQuery(id+"F4.wireOp",EDGE,"E19.trimOffspring"),sQuery(id+"F4.wireOp",EDGE,"E20.trimOffspring"),sQuery(id+"F4.wireOp",EDGE,"E21.1.0"),sQuery(id+"F4.wireOp",EDGE,"E21.1.1"),sQuery(id+"F4.wireOp",EDGE,"E21.1.2"),sQuery(id+"F4.wireOp",EDGE,"E21.1.3"),sQuery(id+"F4.wireOp",EDGE,"E21.1.4"),sQuery(id+"F4.wireOp",EDGE,"E21.1.5"),sQuery(id+"F4.wireOp",EDGE,"E21.1.6"),sQuery(id+"F4.wireOp",EDGE,"E21.1.7"),sQuery(id+"F4.wireOp",EDGE,"E21.1.8"),sQuery(id+"F4.wireOp",EDGE,"E21.2.0"),sQuery(id+"F4.wireOp",EDGE,"E21.2.1"),sQuery(id+"F4.wireOp",EDGE,"E21.2.2"),sQuery(id+"F4.wireOp",EDGE,"E21.2.3"),sQuery(id+"F4.wireOp",EDGE,"E21.2.4"),sQuery(id+"F4.wireOp",EDGE,"E21.2.5"),sQuery(id+"F4.wireOp",EDGE,"E21.2.6"),sQuery(id+"F4.wireOp",EDGE,"E21.2.7"),sQuery(id+"F4.wireOp",EDGE,"E21.2.8"),sQuery(id+"F4.wireOp",EDGE,"E21.3.0"),sQuery(id+"F4.wireOp",EDGE,"E21.3.1"),sQuery(id+"F4.wireOp",EDGE,"E21.3.2"),sQuery(id+"F4.wireOp",EDGE,"E21.3.3"),sQuery(id+"F4.wireOp",EDGE,"E21.3.4"),sQuery(id+"F4.wireOp",EDGE,"E21.3.5"),sQuery(id+"F4.wireOp",EDGE,"E21.3.6"),sQuery(id+"F4.wireOp",EDGE,"E21.3.7"),sQuery(id+"F4.wireOp",EDGE,"E21.3.8"),sQuery(id+"F4.wireOp",EDGE,"E21.4.0"),sQuery(id+"F4.wireOp",EDGE,"E21.4.1"),sQuery(id+"F4.wireOp",EDGE,"E21.4.2"),sQuery(id+"F4.wireOp",EDGE,"E21.4.3"),sQuery(id+"F4.wireOp",EDGE,"E21.4.4"),sQuery(id+"F4.wireOp",EDGE,"E21.4.5"),sQuery(id+"F4.wireOp",EDGE,"E21.4.6"),sQuery(id+"F4.wireOp",EDGE,"E21.4.7"),sQuery(id+"F4.wireOp",EDGE,"E21.4.8"),sQuery(id+"F4.wireOp",EDGE,"E21.5.0"),sQuery(id+"F4.wireOp",EDGE,"E21.5.1"),sQuery(id+"F4.wireOp",EDGE,"E21.5.2"),sQuery(id+"F4.wireOp",EDGE,"E21.5.3"),sQuery(id+"F4.wireOp",EDGE,"E21.5.4"),sQuery(id+"F4.wireOp",EDGE,"E21.5.5"),sQuery(id+"F4.wireOp",EDGE,"E21.5.6"),sQuery(id+"F4.wireOp",EDGE,"E21.5.7"),sQuery(id+"F4.wireOp",EDGE,"E21.5.8"),sQuery(id+"F4.wireOp",EDGE,"E21.6.0"),sQuery(id+"F4.wireOp",EDGE,"E21.6.1"),sQuery(id+"F4.wireOp",EDGE,"E21.6.2"),sQuery(id+"F4.wireOp",EDGE,"E21.6.3"),sQuery(id+"F4.wireOp",EDGE,"E21.6.4"),sQuery(id+"F4.wireOp",EDGE,"E21.6.5"),sQuery(id+"F4.wireOp",EDGE,"E21.6.6"),sQuery(id+"F4.wireOp",EDGE,"E21.6.7"),sQuery(id+"F4.wireOp",EDGE,"E21.6.8"),sQuery(id+"F4.wireOp",EDGE,"E21.7.0"),sQuery(id+"F4.wireOp",EDGE,"E21.7.1"),sQuery(id+"F4.wireOp",EDGE,"E21.7.2"),sQuery(id+"F4.wireOp",EDGE,"E21.7.3"),sQuery(id+"F4.wireOp",EDGE,"E21.7.4"),sQuery(id+"F4.wireOp",EDGE,"E21.7.5"),sQuery(id+"F4.wireOp",EDGE,"E21.7.6"),sQuery(id+"F4.wireOp",EDGE,"E21.7.7"),sQuery(id+"F4.wireOp",EDGE,"E21.7.8"),sQuery(id+"F4.wireOp",EDGE,"E22.trimOffspring"),sQuery(id+"F4.wireOp",EDGE,"E23.trimOffspring"),sQuery(id+"F4.wireOp",EDGE,"E24.trimOffspring"),sQuery(id+"F4.wireOp",EDGE,"E25.trimOffspring"),sQuery(id+"F4.wireOp",EDGE,"E26.trimOffspring"),sQuery(id+"F4.wireOp",EDGE,"E27.trimOffspring"),sQuery(id+"F4.wireOp",EDGE,"E28.trimOffspring"),sQuery(id+"F4.wireOp",EDGE,"E29.trimOffspring"),sQuery(id+"F4.wireOp",EDGE,"E30.trimOffspring"),sQuery(id+"F4.wireOp",EDGE,"E31.trimOffspring"),sQuery(id+"F4.wireOp",EDGE,"E32.trimOffspring"),sQuery(id+"F4.wireOp",EDGE,"E33.trimOffspring"),sQuery(id+"F4.wireOp",EDGE,"E34.trimOffspring"),sQuery(id+"F4.wireOp",EDGE,"E35.trimOffspring"),sQuery(id+"F4.wireOp",EDGE,"E36.trimOffspring"),sQuery(id+"F4.wireOp",EDGE,"E37.trimOffspring"),sQuery(id+"F4.wireOp",EDGE,"E38.trimOffspring"),sQuery(id+"F4.wireOp",EDGE,"E39.trimOffspring"),sQuery(id+"F4.wireOp",EDGE,"E40.trimOffspring"),sQuery(id+"F4.wireOp",EDGE,"E41.trimOffspring"),sQuery(id+"F4.wireOp",EDGE,"E42.trimOffspring"),sQuery(id+"F4.wireOp",EDGE,"E43.trimOffspring"),sQuery(id+"F4.wireOp",EDGE,"E44.trimOffspring"),sQuery(id+"F4.wireOp",EDGE,"E45.trimOffspring"),sQuery(id+"F4.wireOp",EDGE,"E46.trimOffspring"),sQuery(id+"F4.wireOp",EDGE,"E47.trimOffspring"),sQuery(id+"F4.wireOp",EDGE,"E48.trimOffspring"),sQuery(id+"F4.wireOp",EDGE,"E49.trimOffspring"),sQuery(id+"F4.wireOp",EDGE,"E50.bottom"),sQuery(id+"F4.wireOp",EDGE,"E50.top"),sQuery(id+"F4.wireOp",EDGE,"E50.left"),sQuery(id+"F4.wireOp",EDGE,"E50.right"),sQuery(id+"F4.wireOp",EDGE,"E51"),sQuery(id+"F4.wireOp",EDGE,"E52"),sQuery(id+"F4.wireOp",EDGE,"E53.trimOffspring"),sQuery(id+"F4.wireOp",EDGE,"E54"),sQuery(id+"F4.wireOp",EDGE,"E55"),sQuery(id+"F4.wireOp",EDGE,"E56.trimOffspring"),sQuery(id+"F4.wireOp",EDGE,"E57.1.1"),sQuery(id+"F4.wireOp",EDGE,"E57.1.2"),sQuery(id+"F4.wireOp",EDGE,"E57.1.3"),sQuery(id+"F4.wireOp",EDGE,"E57.1.4"),sQuery(id+"F4.wireOp",EDGE,"E57.1.5"),sQuery(id+"F4.wireOp",EDGE,"E57.1.6"),sQuery(id+"F4.wireOp",EDGE,"E57.1.7"),sQuery(id+"F4.wireOp",EDGE,"E57.1.8"),sQuery(id+"F4.wireOp",EDGE,"E57.1.9"),sQuery(id+"F4.wireOp",EDGE,"E57.1.10"),sQuery(id+"F4.wireOp",EDGE,"E57.2.1"),sQuery(id+"F4.wireOp",EDGE,"E57.2.2"),sQuery(id+"F4.wireOp",EDGE,"E57.2.3"),sQuery(id+"F4.wireOp",EDGE,"E57.2.4"),sQuery(id+"F4.wireOp",EDGE,"E57.2.5"),sQuery(id+"F4.wireOp",EDGE,"E57.2.6"),sQuery(id+"F4.wireOp",EDGE,"E57.2.7"),sQuery(id+"F4.wireOp",EDGE,"E57.2.8"),sQuery(id+"F4.wireOp",EDGE,"E57.2.9"),sQuery(id+"F4.wireOp",EDGE,"E57.2.10"),sQuery(id+"F4.wireOp",EDGE,"E57.3.1"),sQuery(id+"F4.wireOp",EDGE,"E57.3.2"),sQuery(id+"F4.wireOp",EDGE,"E57.3.3"),sQuery(id+"F4.wireOp",EDGE,"E57.3.4"),sQuery(id+"F4.wireOp",EDGE,"E57.3.5"),sQuery(id+"F4.wireOp",EDGE,"E57.3.6"),sQuery(id+"F4.wireOp",EDGE,"E57.3.7"),sQuery(id+"F4.wireOp",EDGE,"E57.3.8"),sQuery(id+"F4.wireOp",EDGE,"E57.3.9"),sQuery(id+"F4.wireOp",EDGE,"E57.3.10"),sQuery(id+"F4.wireOp",EDGE,"E57.4.1"),sQuery(id+"F4.wireOp",EDGE,"E57.4.2"),sQuery(id+"F4.wireOp",EDGE,"E57.4.3"),sQuery(id+"F4.wireOp",EDGE,"E57.4.4"),sQuery(id+"F4.wireOp",EDGE,"E57.4.5"),sQuery(id+"F4.wireOp",EDGE,"E57.4.6"),sQuery(id+"F4.wireOp",EDGE,"E57.4.7"),sQuery(id+"F4.wireOp",EDGE,"E57.4.8"),sQuery(id+"F4.wireOp",EDGE,"E57.4.9"),sQuery(id+"F4.wireOp",EDGE,"E57.4.10"),sQuery(id+"F4.wireOp",EDGE,"E57.5.1"),sQuery(id+"F4.wireOp",EDGE,"E57.5.2"),sQuery(id+"F4.wireOp",EDGE,"E57.5.3"),sQuery(id+"F4.wireOp",EDGE,"E57.5.4"),sQuery(id+"F4.wireOp",EDGE,"E57.5.5"),sQuery(id+"F4.wireOp",EDGE,"E57.5.6"),sQuery(id+"F4.wireOp",EDGE,"E57.5.7"),sQuery(id+"F4.wireOp",EDGE,"E57.5.8"),sQuery(id+"F4.wireOp",EDGE,"E57.5.9"),sQuery(id+"F4.wireOp",EDGE,"E57.5.10"),sQuery(id+"F4.wireOp",EDGE,"E57.6.1"),sQuery(id+"F4.wireOp",EDGE,"E57.6.2"),sQuery(id+"F4.wireOp",EDGE,"E57.6.3"),sQuery(id+"F4.wireOp",EDGE,"E57.6.4"),sQuery(id+"F4.wireOp",EDGE,"E57.6.5"),sQuery(id+"F4.wireOp",EDGE,"E57.6.6"),sQuery(id+"F4.wireOp",EDGE,"E57.6.7"),sQuery(id+"F4.wireOp",EDGE,"E57.6.8"),sQuery(id+"F4.wireOp",EDGE,"E57.6.9"),sQuery(id+"F4.wireOp",EDGE,"E57.6.10"),sQuery(id+"F4.wireOp",EDGE,"E57.7.1"),sQuery(id+"F4.wireOp",EDGE,"E57.7.2"),sQuery(id+"F4.wireOp",EDGE,"E57.7.3"),sQuery(id+"F4.wireOp",EDGE,"E57.7.4"),sQuery(id+"F4.wireOp",EDGE,"E57.7.5"),sQuery(id+"F4.wireOp",EDGE,"E57.7.6"),sQuery(id+"F4.wireOp",EDGE,"E57.7.7"),sQuery(id+"F4.wireOp",EDGE,"E57.7.8"),sQuery(id+"F4.wireOp",EDGE,"E57.7.9"),sQuery(id+"F4.wireOp",EDGE,"E57.7.10"),sQuery(id+"F4.wireOp",EDGE,"E58.bottom"),sQuery(id+"F4.wireOp",EDGE,"E58.top"),sQuery(id+"F4.wireOp",EDGE,"E58.left"),sQuery(id+"F4.wireOp",EDGE,"E58.right"),sQuery(id+"F4.wireOp",EDGE,"E59"),sQuery(id+"F4.wireOp",EDGE,"E60"),sQuery(id+"F4.wireOp",EDGE,"E61.trimOffspring"),sQuery(id+"F4.wireOp",EDGE,"E62"),sQuery(id+"F4.wireOp",EDGE,"E63"),sQuery(id+"F4.wireOp",EDGE,"E64.trimOffspring"),sQuery(id+"F4.wireOp",EDGE,"E65.1.0"),sQuery(id+"F4.wireOp",EDGE,"E65.1.2"),sQuery(id+"F4.wireOp",EDGE,"E65.1.3"),sQuery(id+"F4.wireOp",EDGE,"E65.1.4"),sQuery(id+"F4.wireOp",EDGE,"E65.1.5"),sQuery(id+"F4.wireOp",EDGE,"E65.1.6"),sQuery(id+"F4.wireOp",EDGE,"E65.1.7"),sQuery(id+"F4.wireOp",EDGE,"E65.1.8"),sQuery(id+"F4.wireOp",EDGE,"E65.1.9"),sQuery(id+"F4.wireOp",EDGE,"E65.1.10"),sQuery(id+"F4.wireOp",EDGE,"E65.2.0"),sQuery(id+"F4.wireOp",EDGE,"E65.2.2"),sQuery(id+"F4.wireOp",EDGE,"E65.2.3"),sQuery(id+"F4.wireOp",EDGE,"E65.2.4"),sQuery(id+"F4.wireOp",EDGE,"E65.2.5"),sQuery(id+"F4.wireOp",EDGE,"E65.2.6"),sQuery(id+"F4.wireOp",EDGE,"E65.2.7"),sQuery(id+"F4.wireOp",EDGE,"E65.2.8"),sQuery(id+"F4.wireOp",EDGE,"E65.2.9"),sQuery(id+"F4.wireOp",EDGE,"E65.2.10"),sQuery(id+"F4.wireOp",EDGE,"E65.3.0"),sQuery(id+"F4.wireOp",EDGE,"E65.3.2"),sQuery(id+"F4.wireOp",EDGE,"E65.3.3"),sQuery(id+"F4.wireOp",EDGE,"E65.3.4"),sQuery(id+"F4.wireOp",EDGE,"E65.3.5"),sQuery(id+"F4.wireOp",EDGE,"E65.3.6"),sQuery(id+"F4.wireOp",EDGE,"E65.3.7"),sQuery(id+"F4.wireOp",EDGE,"E65.3.8"),sQuery(id+"F4.wireOp",EDGE,"E65.3.9"),sQuery(id+"F4.wireOp",EDGE,"E65.3.10"),sQuery(id+"F4.wireOp",EDGE,"E65.4.0"),sQuery(id+"F4.wireOp",EDGE,"E65.4.2"),sQuery(id+"F4.wireOp",EDGE,"E65.4.3"),sQuery(id+"F4.wireOp",EDGE,"E65.4.4"),sQuery(id+"F4.wireOp",EDGE,"E65.4.5"),sQuery(id+"F4.wireOp",EDGE,"E65.4.6"),sQuery(id+"F4.wireOp",EDGE,"E65.4.7"),sQuery(id+"F4.wireOp",EDGE,"E65.4.8"),sQuery(id+"F4.wireOp",EDGE,"E65.4.9"),sQuery(id+"F4.wireOp",EDGE,"E65.4.10"),sQuery(id+"F4.wireOp",EDGE,"E65.5.0"),sQuery(id+"F4.wireOp",EDGE,"E65.5.2"),sQuery(id+"F4.wireOp",EDGE,"E65.5.3"),sQuery(id+"F4.wireOp",EDGE,"E65.5.4"),sQuery(id+"F4.wireOp",EDGE,"E65.5.5"),sQuery(id+"F4.wireOp",EDGE,"E65.5.6"),sQuery(id+"F4.wireOp",EDGE,"E65.5.7"),sQuery(id+"F4.wireOp",EDGE,"E65.5.8"),sQuery(id+"F4.wireOp",EDGE,"E65.5.9"),sQuery(id+"F4.wireOp",EDGE,"E65.5.10"),sQuery(id+"F4.wireOp",EDGE,"E65.6.0"),sQuery(id+"F4.wireOp",EDGE,"E65.6.2"),sQuery(id+"F4.wireOp",EDGE,"E65.6.3"),sQuery(id+"F4.wireOp",EDGE,"E65.6.4"),sQuery(id+"F4.wireOp",EDGE,"E65.6.5"),sQuery(id+"F4.wireOp",EDGE,"E65.6.6"),sQuery(id+"F4.wireOp",EDGE,"E65.6.7"),sQuery(id+"F4.wireOp",EDGE,"E65.6.8"),sQuery(id+"F4.wireOp",EDGE,"E65.6.9"),sQuery(id+"F4.wireOp",EDGE,"E65.6.10"),sQuery(id+"F4.wireOp",EDGE,"E65.7.0"),sQuery(id+"F4.wireOp",EDGE,"E65.7.2"),sQuery(id+"F4.wireOp",EDGE,"E65.7.3"),sQuery(id+"F4.wireOp",EDGE,"E65.7.4"),sQuery(id+"F4.wireOp",EDGE,"E65.7.5"),sQuery(id+"F4.wireOp",EDGE,"E65.7.6"),sQuery(id+"F4.wireOp",EDGE,"E65.7.7"),sQuery(id+"F4.wireOp",EDGE,"E65.7.8"),sQuery(id+"F4.wireOp",EDGE,"E65.7.9"),sQuery(id+"F4.wireOp",EDGE,"E65.7.10"),sQuery(id+"F4.wireOp",EDGE,"E66.bottom"),sQuery(id+"F4.wireOp",EDGE,"E66.top"),sQuery(id+"F4.wireOp",EDGE,"E66.left"),sQuery(id+"F4.wireOp",EDGE,"E66.right"),sQuery(id+"F4.wireOp",EDGE,"E67"),sQuery(id+"F4.wireOp",EDGE,"E68"),sQuery(id+"F4.wireOp",EDGE,"E69.trimOffspring"),sQuery(id+"F4.wireOp",EDGE,"E70"),sQuery(id+"F4.wireOp",EDGE,"E71"),sQuery(id+"F4.wireOp",EDGE,"E72.trimOffspring"),sQuery(id+"F4.wireOp",EDGE,"E73.1.0"),sQuery(id+"F4.wireOp",EDGE,"E73.1.1"),sQuery(id+"F4.wireOp",EDGE,"E73.1.2"),sQuery(id+"F4.wireOp",EDGE,"E73.1.3"),sQuery(id+"F4.wireOp",EDGE,"E73.1.4"),sQuery(id+"F4.wireOp",EDGE,"E73.1.5"),sQuery(id+"F4.wireOp",EDGE,"E73.1.7"),sQuery(id+"F4.wireOp",EDGE,"E73.1.8"),sQuery(id+"F4.wireOp",EDGE,"E73.1.9"),sQuery(id+"F4.wireOp",EDGE,"E73.1.10"),sQuery(id+"F4.wireOp",EDGE,"E73.2.0"),sQuery(id+"F4.wireOp",EDGE,"E73.2.1"),sQuery(id+"F4.wireOp",EDGE,"E73.2.2"),sQuery(id+"F4.wireOp",EDGE,"E73.2.3"),sQuery(id+"F4.wireOp",EDGE,"E73.2.4"),sQuery(id+"F4.wireOp",EDGE,"E73.2.5"),sQuery(id+"F4.wireOp",EDGE,"E73.2.7"),sQuery(id+"F4.wireOp",EDGE,"E73.2.8"),sQuery(id+"F4.wireOp",EDGE,"E73.2.9"),sQuery(id+"F4.wireOp",EDGE,"E73.2.10"),sQuery(id+"F4.wireOp",EDGE,"E73.3.0"),sQuery(id+"F4.wireOp",EDGE,"E73.3.1"),sQuery(id+"F4.wireOp",EDGE,"E73.3.2"),sQuery(id+"F4.wireOp",EDGE,"E73.3.3"),sQuery(id+"F4.wireOp",EDGE,"E73.3.4"),sQuery(id+"F4.wireOp",EDGE,"E73.3.5"),sQuery(id+"F4.wireOp",EDGE,"E73.3.7"),sQuery(id+"F4.wireOp",EDGE,"E73.3.8"),sQuery(id+"F4.wireOp",EDGE,"E73.3.9"),sQuery(id+"F4.wireOp",EDGE,"E73.3.10"),sQuery(id+"F4.wireOp",EDGE,"E73.4.0"),sQuery(id+"F4.wireOp",EDGE,"E73.4.1"),sQuery(id+"F4.wireOp",EDGE,"E73.4.2"),sQuery(id+"F4.wireOp",EDGE,"E73.4.3"),sQuery(id+"F4.wireOp",EDGE,"E73.4.4"),sQuery(id+"F4.wireOp",EDGE,"E73.4.5"),sQuery(id+"F4.wireOp",EDGE,"E73.4.7"),sQuery(id+"F4.wireOp",EDGE,"E73.4.8"),sQuery(id+"F4.wireOp",EDGE,"E73.4.9"),sQuery(id+"F4.wireOp",EDGE,"E73.4.10"),sQuery(id+"F4.wireOp",EDGE,"E73.5.0"),sQuery(id+"F4.wireOp",EDGE,"E73.5.1"),sQuery(id+"F4.wireOp",EDGE,"E73.5.2"),sQuery(id+"F4.wireOp",EDGE,"E73.5.3"),sQuery(id+"F4.wireOp",EDGE,"E73.5.4"),sQuery(id+"F4.wireOp",EDGE,"E73.5.5"),sQuery(id+"F4.wireOp",EDGE,"E73.5.7"),sQuery(id+"F4.wireOp",EDGE,"E73.5.8"),sQuery(id+"F4.wireOp",EDGE,"E73.5.9"),sQuery(id+"F4.wireOp",EDGE,"E73.5.10"),sQuery(id+"F4.wireOp",EDGE,"E73.6.0"),sQuery(id+"F4.wireOp",EDGE,"E73.6.1"),sQuery(id+"F4.wireOp",EDGE,"E73.6.2"),sQuery(id+"F4.wireOp",EDGE,"E73.6.3"),sQuery(id+"F4.wireOp",EDGE,"E73.6.4"),sQuery(id+"F4.wireOp",EDGE,"E73.6.5"),sQuery(id+"F4.wireOp",EDGE,"E73.6.7"),sQuery(id+"F4.wireOp",EDGE,"E73.6.8"),sQuery(id+"F4.wireOp",EDGE,"E73.6.9"),sQuery(id+"F4.wireOp",EDGE,"E73.6.10"),sQuery(id+"F4.wireOp",EDGE,"E73.7.0"),sQuery(id+"F4.wireOp",EDGE,"E73.7.1"),sQuery(id+"F4.wireOp",EDGE,"E73.7.2"),sQuery(id+"F4.wireOp",EDGE,"E73.7.3"),sQuery(id+"F4.wireOp",EDGE,"E73.7.4"),sQuery(id+"F4.wireOp",EDGE,"E73.7.5"),sQuery(id+"F4.wireOp",EDGE,"E73.7.7"),sQuery(id+"F4.wireOp",EDGE,"E73.7.8"),sQuery(id+"F4.wireOp",EDGE,"E73.7.9"),sQuery(id+"F4.wireOp",EDGE,"E73.7.10")])],"isStart":true});
            var sketch = newSketch(context, id + "F27", { "sketchPlane" : qUnion([Q0])});
            skCircle(sketch, "E282.0", {"center": v(0, 0) * mm, "radius": 520 * mm});
            skSolve(sketch);
        }
        {
            var Q0;
            Q0=sQuery(id+"F27.wireOp",EDGE,"E282.0");
            extrude(context, id + "F28", {"bodyType" : ToolBodyType.SURFACE, "surfaceEntities" : qUnion([Q0]), "depth" : 190 * mm, "offsetDistance" : 25 * mm});
        }
        {
            var Q0;
            Q0=makeQuery(id+"F7.opExtrude","CAP_FACE",FACE,{"disambiguationData":[OSD([sQuery(id+"F6.wireOp",EDGE,"E76.0"),sQuery(id+"F6.wireOp",EDGE,"E80"),sQuery(id+"F6.wireOp",EDGE,"E85"),sQuery(id+"F6.wireOp",EDGE,"E86"),sQuery(id+"F6.wireOp",EDGE,"E90.1.7"),sQuery(id+"F6.wireOp",EDGE,"E90.1.8"),sQuery(id+"F6.wireOp",EDGE,"E90.2.7"),sQuery(id+"F6.wireOp",EDGE,"E90.2.8"),sQuery(id+"F6.wireOp",EDGE,"E90.3.7"),sQuery(id+"F6.wireOp",EDGE,"E90.3.8"),sQuery(id+"F6.wireOp",EDGE,"E90.4.7"),sQuery(id+"F6.wireOp",EDGE,"E90.4.8"),sQuery(id+"F6.wireOp",EDGE,"E90.5.7"),sQuery(id+"F6.wireOp",EDGE,"E90.5.8"),sQuery(id+"F6.wireOp",EDGE,"E90.6.7"),sQuery(id+"F6.wireOp",EDGE,"E90.6.8"),sQuery(id+"F6.wireOp",EDGE,"E90.7.7"),sQuery(id+"F6.wireOp",EDGE,"E90.7.8"),sQuery(id+"F6.wireOp",EDGE,"E93.trimOffspring"),sQuery(id+"F6.wireOp",EDGE,"E98.trimOffspring"),sQuery(id+"F6.wireOp",EDGE,"E101.trimOffspring"),sQuery(id+"F6.wireOp",EDGE,"E111.trimOffspring"),sQuery(id+"F6.wireOp",EDGE,"E115.trimOffspring"),sQuery(id+"F6.wireOp",EDGE,"E117.0"),sQuery(id+"F6.wireOp",EDGE,"E118.0"),sQuery(id+"F6.wireOp",EDGE,"E119.0"),sQuery(id+"F6.wireOp",EDGE,"E120.0"),sQuery(id+"F6.wireOp",EDGE,"E121.0"),sQuery(id+"F6.wireOp",EDGE,"E122.0"),sQuery(id+"F6.wireOp",EDGE,"E123.0"),sQuery(id+"F6.wireOp",EDGE,"E124.0"),sQuery(id+"F6.wireOp",EDGE,"E125.0"),sQuery(id+"F6.wireOp",EDGE,"E126.0"),sQuery(id+"F6.wireOp",EDGE,"E127.trimOffspring"),sQuery(id+"F6.wireOp",EDGE,"E128.trimOffspring"),sQuery(id+"F6.wireOp",EDGE,"E129.1.0"),sQuery(id+"F6.wireOp",EDGE,"E129.1.1"),sQuery(id+"F6.wireOp",EDGE,"E129.1.2"),sQuery(id+"F6.wireOp",EDGE,"E129.1.3"),sQuery(id+"F6.wireOp",EDGE,"E129.1.4"),sQuery(id+"F6.wireOp",EDGE,"E129.1.5"),sQuery(id+"F6.wireOp",EDGE,"E129.1.6"),sQuery(id+"F6.wireOp",EDGE,"E129.1.7"),sQuery(id+"F6.wireOp",EDGE,"E129.1.8"),sQuery(id+"F6.wireOp",EDGE,"E129.1.9"),sQuery(id+"F6.wireOp",EDGE,"E129.2.0"),sQuery(id+"F6.wireOp",EDGE,"E129.2.1"),sQuery(id+"F6.wireOp",EDGE,"E129.2.2"),sQuery(id+"F6.wireOp",EDGE,"E129.2.3"),sQuery(id+"F6.wireOp",EDGE,"E129.2.4"),sQuery(id+"F6.wireOp",EDGE,"E129.2.5"),sQuery(id+"F6.wireOp",EDGE,"E129.2.6"),sQuery(id+"F6.wireOp",EDGE,"E129.2.7"),sQuery(id+"F6.wireOp",EDGE,"E129.2.8"),sQuery(id+"F6.wireOp",EDGE,"E129.2.9"),sQuery(id+"F6.wireOp",EDGE,"E129.3.0"),sQuery(id+"F6.wireOp",EDGE,"E129.3.1"),sQuery(id+"F6.wireOp",EDGE,"E129.3.2"),sQuery(id+"F6.wireOp",EDGE,"E129.3.3"),sQuery(id+"F6.wireOp",EDGE,"E129.3.4"),sQuery(id+"F6.wireOp",EDGE,"E129.3.5"),sQuery(id+"F6.wireOp",EDGE,"E129.3.6"),sQuery(id+"F6.wireOp",EDGE,"E129.3.7"),sQuery(id+"F6.wireOp",EDGE,"E129.3.8"),sQuery(id+"F6.wireOp",EDGE,"E129.3.9"),sQuery(id+"F6.wireOp",EDGE,"E129.4.0"),sQuery(id+"F6.wireOp",EDGE,"E129.4.1"),sQuery(id+"F6.wireOp",EDGE,"E129.4.2"),sQuery(id+"F6.wireOp",EDGE,"E129.4.3"),sQuery(id+"F6.wireOp",EDGE,"E129.4.4"),sQuery(id+"F6.wireOp",EDGE,"E129.4.5"),sQuery(id+"F6.wireOp",EDGE,"E129.4.6"),sQuery(id+"F6.wireOp",EDGE,"E129.4.7"),sQuery(id+"F6.wireOp",EDGE,"E129.4.8"),sQuery(id+"F6.wireOp",EDGE,"E129.4.9"),sQuery(id+"F6.wireOp",EDGE,"E129.5.0"),sQuery(id+"F6.wireOp",EDGE,"E129.5.1"),sQuery(id+"F6.wireOp",EDGE,"E129.5.2"),sQuery(id+"F6.wireOp",EDGE,"E129.5.3"),sQuery(id+"F6.wireOp",EDGE,"E129.5.4"),sQuery(id+"F6.wireOp",EDGE,"E129.5.5"),sQuery(id+"F6.wireOp",EDGE,"E129.5.6"),sQuery(id+"F6.wireOp",EDGE,"E129.5.7"),sQuery(id+"F6.wireOp",EDGE,"E129.5.8"),sQuery(id+"F6.wireOp",EDGE,"E129.5.9"),sQuery(id+"F6.wireOp",EDGE,"E129.6.0"),sQuery(id+"F6.wireOp",EDGE,"E129.6.1"),sQuery(id+"F6.wireOp",EDGE,"E129.6.2"),sQuery(id+"F6.wireOp",EDGE,"E129.6.3"),sQuery(id+"F6.wireOp",EDGE,"E129.6.4"),sQuery(id+"F6.wireOp",EDGE,"E129.6.5"),sQuery(id+"F6.wireOp",EDGE,"E129.6.6"),sQuery(id+"F6.wireOp",EDGE,"E129.6.7"),sQuery(id+"F6.wireOp",EDGE,"E129.6.8"),sQuery(id+"F6.wireOp",EDGE,"E129.6.9"),sQuery(id+"F6.wireOp",EDGE,"E129.7.0"),sQuery(id+"F6.wireOp",EDGE,"E129.7.1"),sQuery(id+"F6.wireOp",EDGE,"E129.7.2"),sQuery(id+"F6.wireOp",EDGE,"E129.7.3"),sQuery(id+"F6.wireOp",EDGE,"E129.7.4"),sQuery(id+"F6.wireOp",EDGE,"E129.7.5"),sQuery(id+"F6.wireOp",EDGE,"E129.7.6"),sQuery(id+"F6.wireOp",EDGE,"E129.7.7"),sQuery(id+"F6.wireOp",EDGE,"E129.7.8"),sQuery(id+"F6.wireOp",EDGE,"E129.7.9"),sQuery(id+"F6.wireOp",EDGE,"E130"),sQuery(id+"F6.wireOp",EDGE,"E132"),sQuery(id+"F6.wireOp",EDGE,"E134.1.0"),sQuery(id+"F6.wireOp",EDGE,"E134.1.1"),sQuery(id+"F6.wireOp",EDGE,"E134.2.0"),sQuery(id+"F6.wireOp",EDGE,"E134.2.1"),sQuery(id+"F6.wireOp",EDGE,"E134.3.0"),sQuery(id+"F6.wireOp",EDGE,"E134.3.1"),sQuery(id+"F6.wireOp",EDGE,"E134.4.0"),sQuery(id+"F6.wireOp",EDGE,"E134.4.1"),sQuery(id+"F6.wireOp",EDGE,"E134.5.0"),sQuery(id+"F6.wireOp",EDGE,"E134.5.1"),sQuery(id+"F6.wireOp",EDGE,"E134.6.0"),sQuery(id+"F6.wireOp",EDGE,"E134.6.1"),sQuery(id+"F6.wireOp",EDGE,"E134.7.0"),sQuery(id+"F6.wireOp",EDGE,"E134.7.1")])],"isStart":true});
            var sketch = newSketch(context, id + "F29", { "sketchPlane" : qUnion([Q0])});
            skCircle(sketch, "E283.0", {"center": v(0, 0) * mm, "radius": 280 * mm});
            skSolve(sketch);
        }
        {
            var Q0;
            Q0 = qSketchRegion(id + "F29", true);
            var Q1;
            Q1=sQuery(id+"F29.wireOp",EDGE,"E283.0");
            extrude(context, id + "F30", {"entities" : qUnion([Q0]), "bodyType" : ToolBodyType.SURFACE, "surfaceEntities" : qUnion([Q1]), "depth" : 190 * mm, "offsetDistance" : 25 * mm});
        }
    });
